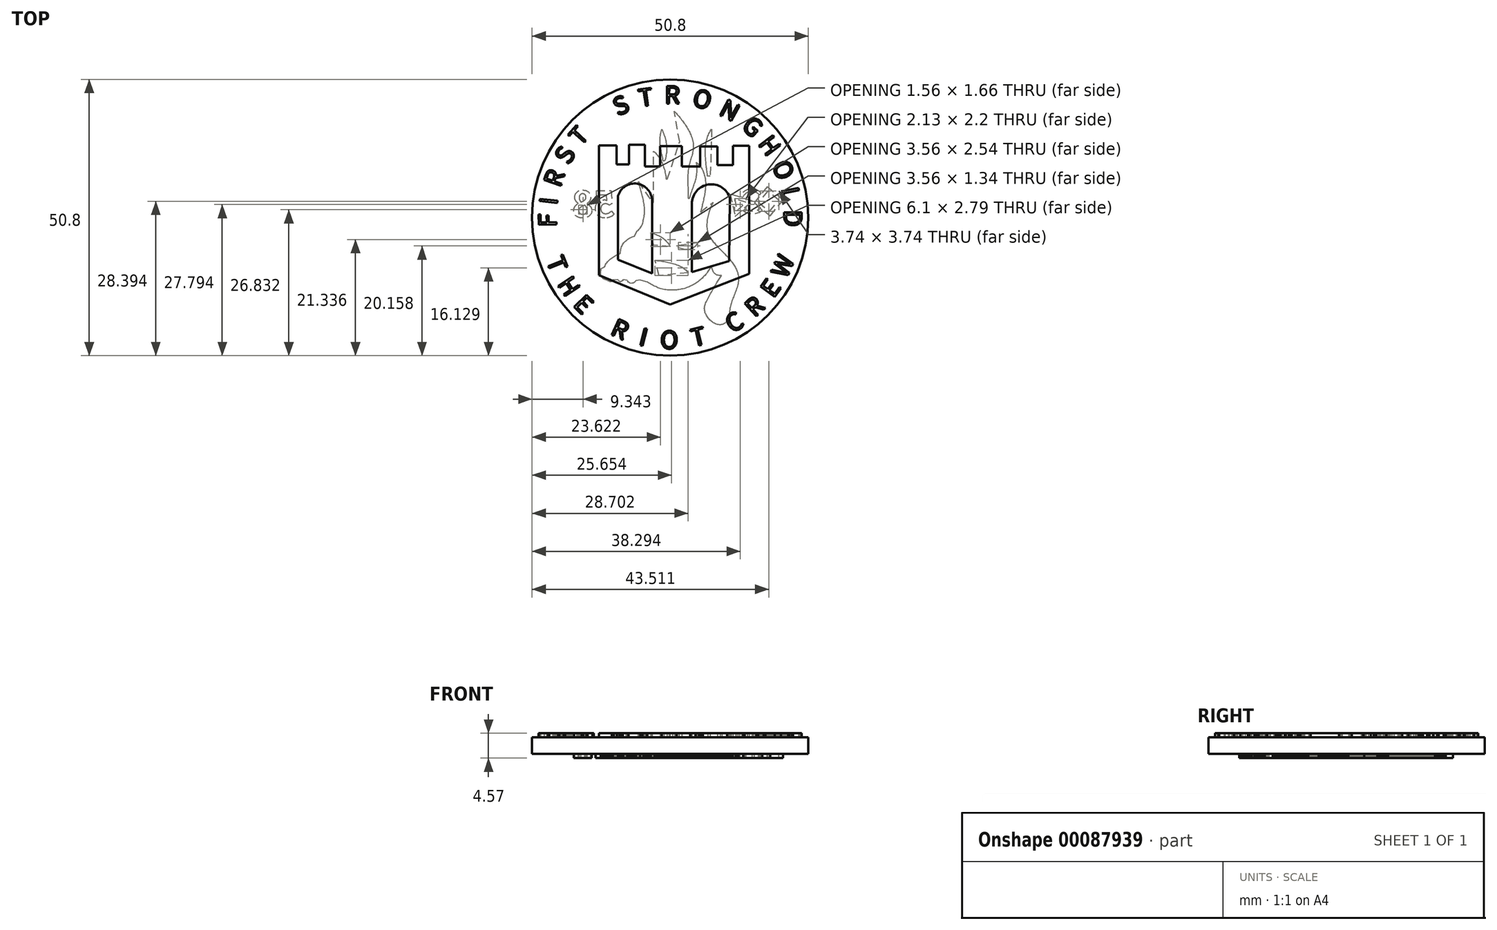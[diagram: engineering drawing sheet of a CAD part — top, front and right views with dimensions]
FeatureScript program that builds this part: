
annotation { "Feature Type Name" : "Feature", "Feature Type Description" : "" }
export const myFeature = defineFeature(function(context is Context, id is Id, definition is map)
    precondition{}
    {
        {
            var Q0;
            Q0=qCreatedBy(makeId("Top.planeOp"),FACE);
            var sketch = newSketch(context, id + "F0", { "sketchPlane" : qUnion([Q0])});
            skCircle(sketch, "E0", {"center": v(0, 0) * mm, "radius": 25.4 * mm});
            skSolve(sketch);
        }
        {
            var Q0;
            Q0 = qSketchRegion(id + "F0", true);
            extrude(context, id + "F1", {"entities" : qUnion([Q0]), "depth" : 3.05 * mm});
        }
        {
            var Q0;
            Q0=makeQuery(id+"F1.opExtrude","CAP_FACE",FACE,{"disambiguationData":[OSD([sQuery(id+"F0.wireOp",EDGE,"E0")])],"isStart":true});
            var sketch = newSketch(context, id + "F2", { "sketchPlane" : qUnion([Q0])});
            skSolve(sketch);
        }
        {
            var Q0;
            Q0=makeQuery(id+"F1.opExtrude","CAP_FACE",FACE,{"disambiguationData":[OSD([sQuery(id+"F0.wireOp",EDGE,"E0")])],"isStart":false});
            var sketch = newSketch(context, id + "F3", { "sketchPlane" : qUnion([Q0])});
            skText(sketch, "E1", { "text": "F", "fontName": "NotoSansCJKjp-Regular.otf"});
            skText(sketch, "E2", { "text": "I", "fontName": "NotoSansCJKjp-Regular.otf"});
            skText(sketch, "E3", { "text": "R", "fontName": "NotoSansCJKjp-Regular.otf"});
            skText(sketch, "E4", { "text": "S", "fontName": "NotoSansCJKjp-Regular.otf"});
            skText(sketch, "E5", { "text": "T", "fontName": "NotoSansCJKjp-Regular.otf"});
            skCircle(sketch, "E6", {"center": v(0, 0) * mm, "radius": 20.96 * mm, "construction": true});
            skText(sketch, "E7", { "text": "S", "fontName": "NotoSansCJKjp-Regular.otf"});
            skText(sketch, "E8", { "text": "T", "fontName": "NotoSansCJKjp-Regular.otf"});
            skText(sketch, "E9", { "text": "O", "fontName": "NotoSansCJKjp-Regular.otf"});
            skText(sketch, "E10", { "text": "R", "fontName": "NotoSansCJKjp-Regular.otf"});
            skText(sketch, "E11", { "text": "N", "fontName": "NotoSansCJKjp-Regular.otf"});
            skText(sketch, "E12", { "text": "G", "fontName": "NotoSansCJKjp-Regular.otf"});
            skText(sketch, "E13", { "text": "H", "fontName": "NotoSansCJKjp-Regular.otf"});
            skText(sketch, "E14", { "text": "L", "fontName": "NotoSansCJKjp-Regular.otf"});
            skText(sketch, "E15", { "text": "D", "fontName": "NotoSansCJKjp-Regular.otf"});
            skText(sketch, "E16", { "text": "O", "fontName": "NotoSansCJKjp-Regular.otf"});
            skText(sketch, "E17", { "text": "T", "fontName": "NotoSansCJKjp-Regular.otf"});
            skText(sketch, "E18", { "text": "H", "fontName": "NotoSansCJKjp-Regular.otf"});
            skText(sketch, "E19", { "text": "E", "fontName": "NotoSansCJKjp-Regular.otf"});
            skText(sketch, "E20", { "text": "R", "fontName": "NotoSansCJKjp-Regular.otf"});
            skText(sketch, "E21", { "text": "I", "fontName": "NotoSansCJKjp-Regular.otf"});
            skText(sketch, "E22", { "text": "O", "fontName": "NotoSansCJKjp-Regular.otf"});
            skText(sketch, "E23", { "text": "T", "fontName": "NotoSansCJKjp-Regular.otf"});
            skText(sketch, "E24", { "text": "C", "fontName": "NotoSansCJKjp-Regular.otf"});
            skText(sketch, "E25", { "text": "E", "fontName": "NotoSansCJKjp-Regular.otf"});
            skText(sketch, "E26", { "text": "R", "fontName": "NotoSansCJKjp-Regular.otf"});
            skText(sketch, "E27", { "text": "W", "fontName": "NotoSansCJKjp-Regular.otf"});
            skLineSegment(sketch, "E28", {"start": v(-13.1, 13.29) * mm, "end": v(-13.1, -10.62) * mm});
            skLineSegment(sketch, "E29", {"start": v(-13.1, -10.62) * mm, "end": v(0, -15.98) * mm});
            skLineSegment(sketch, "E30", {"start": v(0, -15.98) * mm, "end": v(14.5, -10.34) * mm});
            skLineSegment(sketch, "E31", {"start": v(14.5, -10.34) * mm, "end": v(14.5, 13.2) * mm});
            skLineSegment(sketch, "E32", {"start": v(-13.1, 13.29) * mm, "end": v(-9.9, 13.29) * mm});
            skLineSegment(sketch, "E33", {"start": v(-9.9, 13.29) * mm, "end": v(-9.9, 9.78) * mm});
            skLineSegment(sketch, "E34", {"start": v(-9.9, 9.78) * mm, "end": v(-7.61, 9.78) * mm});
            skLineSegment(sketch, "E35", {"start": v(-7.61, 9.78) * mm, "end": v(-7.61, 13.36) * mm});
            skLineSegment(sketch, "E36", {"start": v(-7.61, 13.36) * mm, "end": v(-4.64, 13.36) * mm});
            skLineSegment(sketch, "E37", {"start": v(-4.64, 13.36) * mm, "end": v(-4.64, 9.4) * mm});
            skLineSegment(sketch, "E38", {"start": v(-4.64, 9.4) * mm, "end": v(-1.9, 9.4) * mm});
            skLineSegment(sketch, "E39", {"start": v(-1.9, 9.4) * mm, "end": v(-1.9, 13.1) * mm});
            skLineSegment(sketch, "E40", {"start": v(-1.9, 13.1) * mm, "end": v(2.15, 13.1) * mm});
            skLineSegment(sketch, "E41", {"start": v(2.15, 13.1) * mm, "end": v(2.15, 9.4) * mm});
            skLineSegment(sketch, "E42", {"start": v(2.15, 9.4) * mm, "end": v(5.5, 9.4) * mm});
            skLineSegment(sketch, "E43", {"start": v(5.5, 9.4) * mm, "end": v(5.5, 13.05) * mm});
            skLineSegment(sketch, "E44", {"start": v(5.5, 13.05) * mm, "end": v(8.7, 13.05) * mm});
            skLineSegment(sketch, "E45", {"start": v(8.7, 13.05) * mm, "end": v(8.7, 9.63) * mm});
            skLineSegment(sketch, "E46", {"start": v(8.7, 9.63) * mm, "end": v(11.52, 9.63) * mm});
            skLineSegment(sketch, "E47", {"start": v(11.52, 9.63) * mm, "end": v(11.52, 13.2) * mm});
            skLineSegment(sketch, "E48", {"start": v(11.52, 13.2) * mm, "end": v(14.5, 13.2) * mm});
            skLineSegment(sketch, "E49", {"start": v(-9.6, 3.99) * mm, "end": v(-9.6, -7.77) * mm});
            skLineSegment(sketch, "E50", {"start": v(-9.6, -7.77) * mm, "end": v(-3.34, -10.31) * mm});
            skLineSegment(sketch, "E51", {"start": v(-3.34, -10.31) * mm, "end": v(-3.34, 3.07) * mm});
            skArc(sketch, "E52", {"start": v(-3.34, 3.07) * mm, "mid": v(-6.07, 6.23) * mm, "end": v(-9.6, 3.99) * mm});
            skLineSegment(sketch, "E53", {"start": v(3.97, 2.54) * mm, "end": v(3.97, -10.04) * mm});
            skLineSegment(sketch, "E54", {"start": v(3.97, -10.04) * mm, "end": v(10.83, -7.98) * mm});
            skLineSegment(sketch, "E55", {"start": v(10.83, -7.98) * mm, "end": v(10.99, 3.53) * mm});
            skArc(sketch, "E56", {"start": v(10.99, 3.53) * mm, "mid": v(7.05, 6.08) * mm, "end": v(3.97, 2.54) * mm});
            skCircle(sketch, "E57", {"center": v(0, 0) * mm, "radius": 24.13 * mm, "construction": true});
            const initialGuessF3  = {"E1": [-0.02089, -0.0017, -0.02572, 0.99967, 0.0032], "E2": [-0.02083, 0.00224, 0.1071, 0.99425, 0.00318], "E3": [-0.02024, 0.00542, 0.32053, 0.94724, 0.00322], "E4": [-0.01865, 0.00955, 0.50735, 0.86174, 0.00321], "E5": [-0.0165, 0.01298, 0.66413, 0.74762, 0.00317], "E7": [-0.00964, 0.01865, 0.91348, 0.40689, 0.00317], "E8": [-0.00558, 0.02032, 0.98899, 0.14799, 0.00318], "E9": [0.00392, 0.02064, 0.96647, -0.25677, 0.00317], "E10": [-0.00106, 0.02097, 0.99991, -0.01329, 0.00318], "E11": [0.0088, 0.01906, 0.87845, -0.47783, 0.00318], "E12": [0.01296, 0.01652, 0.74534, -0.66669, 0.00317], "E13": [0.01602, 0.01358, 0.59523, -0.80356, 0.00317], "E14": [0.02032, 0.00523, 0.19664, -0.98048, 0.00317], "E15": [0.02096, 0.00136, -0.00136, -1, 0.00317], "E16": [0.01867, 0.00964, 0.39392, -0.91914, 0.00318], "E17": [-0.02283, -0.00792, 0.3764, -0.92645, 0.00318], "E18": [-0.02086, -0.01221, 0.55387, -0.8326, 0.00317], "E19": [-0.01796, -0.01616, 0.70445, -0.70976, 0.00317], "E20": [-0.01115, -0.02144, 0.9114, -0.41154, 0.00318], "E21": [-0.00592, -0.02339, 0.96943, -0.24538, 0.00318], "E22": [-0.00184, -0.0241, 0.9999, -0.01387, 0.00318], "E23": [0.00424, -0.02379, 0.97409, 0.22617, 0.00317], "E24": [0.0114, -0.0213, 0.85453, 0.5194, 0.00317], "E25": [0.01898, -0.01495, 0.57975, 0.8148, 0.00317], "E26": [0.01556, -0.01849, 0.7281, 0.68548, 0.00318], "E27": [0.02138, -0.01135, 0.399, 0.91695, 0.00317]};
            skSetInitialGuess(sketch, initialGuessF3);
            skSolve(sketch);
        }
        {
            var Q0;
            Q0 = qSketchRegion(id + "F3", true);
            extrude(context, id + "F4", {"entities" : qUnion([Q0]), "operationType" : NewBodyOperationType.ADD, "depth" : 0.76 * mm});
        }
        {
            var Q0;
            Q0=makeQuery(id+"F2.imprint","IMPRINT",FACE,{"disambiguationData":[TD([[makeQuery(id+"F2.imprint","IMPRINT",EDGE,{"derivedFrom":makeQuery(id+"F1.opExtrude","CAP_EDGE",EDGE,{"disambiguationData":[OSD([sQuery(id+"F0.wireOp",EDGE,"E0")])],"isStart":true})}),-1.0]])]});
            var sketch = newSketch(context, id + "F5", { "sketchPlane" : qUnion([Q0])});
            skLineSegment(sketch, "E58", {"start": v(-0.76, 19.56) * mm, "end": v(-0.93, 19.36) * mm});
            skLineSegment(sketch, "E59", {"start": v(-0.93, 19.36) * mm, "end": v(-1.1, 19.17) * mm});
            skLineSegment(sketch, "E60", {"start": v(-1.1, 19.17) * mm, "end": v(-1.27, 18.97) * mm});
            skLineSegment(sketch, "E61", {"start": v(-1.27, 18.97) * mm, "end": v(-1.44, 18.78) * mm});
            skLineSegment(sketch, "E62", {"start": v(-1.44, 18.78) * mm, "end": v(-1.6, 18.58) * mm});
            skLineSegment(sketch, "E63", {"start": v(-1.6, 18.58) * mm, "end": v(-1.77, 18.39) * mm});
            skLineSegment(sketch, "E64", {"start": v(-1.77, 18.39) * mm, "end": v(-1.93, 18.2) * mm});
            skLineSegment(sketch, "E65", {"start": v(-1.93, 18.2) * mm, "end": v(-2.09, 18) * mm});
            skLineSegment(sketch, "E66", {"start": v(-2.09, 18) * mm, "end": v(-2.24, 17.8) * mm});
            skLineSegment(sketch, "E67", {"start": v(-2.24, 17.8) * mm, "end": v(-2.4, 17.59) * mm});
            skLineSegment(sketch, "E68", {"start": v(-2.4, 17.59) * mm, "end": v(-2.55, 17.39) * mm});
            skLineSegment(sketch, "E69", {"start": v(-2.55, 17.39) * mm, "end": v(-2.7, 17.18) * mm});
            skLineSegment(sketch, "E70", {"start": v(-2.7, 17.18) * mm, "end": v(-2.84, 16.97) * mm});
            skLineSegment(sketch, "E71", {"start": v(-2.84, 16.97) * mm, "end": v(-2.97, 16.76) * mm});
            skLineSegment(sketch, "E72", {"start": v(-2.97, 16.76) * mm, "end": v(-3.1, 16.55) * mm});
            skLineSegment(sketch, "E73", {"start": v(-3.1, 16.55) * mm, "end": v(-3.23, 16.33) * mm});
            skLineSegment(sketch, "E74", {"start": v(-3.23, 16.33) * mm, "end": v(-3.35, 16.12) * mm});
            skLineSegment(sketch, "E75", {"start": v(-3.35, 16.12) * mm, "end": v(-3.47, 15.9) * mm});
            skLineSegment(sketch, "E76", {"start": v(-3.47, 15.9) * mm, "end": v(-3.58, 15.67) * mm});
            skLineSegment(sketch, "E77", {"start": v(-3.58, 15.67) * mm, "end": v(-3.68, 15.44) * mm});
            skLineSegment(sketch, "E78", {"start": v(-3.68, 15.44) * mm, "end": v(-3.78, 15.2) * mm});
            skLineSegment(sketch, "E79", {"start": v(-3.78, 15.2) * mm, "end": v(-3.87, 14.97) * mm});
            skLineSegment(sketch, "E80", {"start": v(-3.87, 14.97) * mm, "end": v(-3.95, 14.73) * mm});
            skLineSegment(sketch, "E81", {"start": v(-3.95, 14.73) * mm, "end": v(-4.03, 14.48) * mm});
            skLineSegment(sketch, "E82", {"start": v(-4.03, 14.48) * mm, "end": v(-4.1, 14.23) * mm});
            skLineSegment(sketch, "E83", {"start": v(-4.1, 14.23) * mm, "end": v(-4.15, 13.98) * mm});
            skLineSegment(sketch, "E84", {"start": v(-4.15, 13.98) * mm, "end": v(-4.2, 13.72) * mm});
            skLineSegment(sketch, "E85", {"start": v(-4.2, 13.72) * mm, "end": v(-4.23, 13.47) * mm});
            skLineSegment(sketch, "E86", {"start": v(-4.23, 13.47) * mm, "end": v(-4.25, 13.22) * mm});
            skLineSegment(sketch, "E87", {"start": v(-4.25, 13.22) * mm, "end": v(-4.25, 12.97) * mm});
            skLineSegment(sketch, "E88", {"start": v(-4.25, 12.97) * mm, "end": v(-4.24, 12.73) * mm});
            skLineSegment(sketch, "E89", {"start": v(-4.24, 12.73) * mm, "end": v(-4.21, 12.49) * mm});
            skLineSegment(sketch, "E90", {"start": v(-4.21, 12.49) * mm, "end": v(-4.17, 12.25) * mm});
            skLineSegment(sketch, "E91", {"start": v(-4.17, 12.25) * mm, "end": v(-4.13, 12) * mm});
            skLineSegment(sketch, "E92", {"start": v(-4.13, 12) * mm, "end": v(-4.07, 11.77) * mm});
            skLineSegment(sketch, "E93", {"start": v(-4.07, 11.77) * mm, "end": v(-4.01, 11.53) * mm});
            skLineSegment(sketch, "E94", {"start": v(-4.01, 11.53) * mm, "end": v(-3.95, 11.3) * mm});
            skLineSegment(sketch, "E95", {"start": v(-3.95, 11.3) * mm, "end": v(-3.88, 11.06) * mm});
            skLineSegment(sketch, "E96", {"start": v(-3.88, 11.06) * mm, "end": v(-3.8, 10.82) * mm});
            skLineSegment(sketch, "E97", {"start": v(-3.8, 10.82) * mm, "end": v(-3.74, 10.58) * mm});
            skLineSegment(sketch, "E98", {"start": v(-3.74, 10.58) * mm, "end": v(-3.66, 10.34) * mm});
            skLineSegment(sketch, "E99", {"start": v(-3.66, 10.34) * mm, "end": v(-3.6, 10.1) * mm});
            skLineSegment(sketch, "E100", {"start": v(-3.6, 10.1) * mm, "end": v(-3.53, 9.87) * mm});
            skLineSegment(sketch, "E101", {"start": v(-3.53, 9.87) * mm, "end": v(-3.47, 9.63) * mm});
            skLineSegment(sketch, "E102", {"start": v(-3.47, 9.63) * mm, "end": v(-3.42, 9.39) * mm});
            skLineSegment(sketch, "E103", {"start": v(-3.42, 9.39) * mm, "end": v(-3.37, 9.14) * mm});
            skLineSegment(sketch, "E104", {"start": v(-3.37, 9.14) * mm, "end": v(-3.34, 8.9) * mm});
            skLineSegment(sketch, "E105", {"start": v(-3.34, 8.9) * mm, "end": v(-3.3, 8.64) * mm});
            skLineSegment(sketch, "E106", {"start": v(-3.3, 8.64) * mm, "end": v(-3.28, 8.4) * mm});
            skLineSegment(sketch, "E107", {"start": v(-3.28, 8.4) * mm, "end": v(-3.26, 8.14) * mm});
            skLineSegment(sketch, "E108", {"start": v(-3.26, 8.14) * mm, "end": v(-3.24, 7.89) * mm});
            skLineSegment(sketch, "E109", {"start": v(-3.24, 7.89) * mm, "end": v(-3.23, 7.63) * mm});
            skLineSegment(sketch, "E110", {"start": v(-3.23, 7.63) * mm, "end": v(-3.22, 7.38) * mm});
            skLineSegment(sketch, "E111", {"start": v(-3.22, 7.38) * mm, "end": v(-3.22, 7.12) * mm});
            skLineSegment(sketch, "E112", {"start": v(-3.22, 7.12) * mm, "end": v(-3.22, 6.87) * mm});
            skLineSegment(sketch, "E113", {"start": v(-3.22, 6.87) * mm, "end": v(-3.22, 6.61) * mm});
            skLineSegment(sketch, "E114", {"start": v(-3.22, 6.61) * mm, "end": v(-3.23, 6.36) * mm});
            skLineSegment(sketch, "E115", {"start": v(-3.23, 6.36) * mm, "end": v(-3.23, 6.1) * mm});
            skLineSegment(sketch, "E116", {"start": v(-3.23, 6.1) * mm, "end": v(-3.24, 5.85) * mm});
            skLineSegment(sketch, "E117", {"start": v(-3.24, 5.85) * mm, "end": v(-3.25, 5.59) * mm});
            skLineSegment(sketch, "E118", {"start": v(-3.25, 5.59) * mm, "end": v(-3.26, 5.33) * mm});
            skLineSegment(sketch, "E119", {"start": v(-3.26, 5.33) * mm, "end": v(-3.27, 5.08) * mm});
            skLineSegment(sketch, "E120", {"start": v(-3.27, 5.08) * mm, "end": v(-3.28, 4.82) * mm});
            skLineSegment(sketch, "E121", {"start": v(-3.28, 4.82) * mm, "end": v(-3.28, 4.57) * mm});
            skLineSegment(sketch, "E122", {"start": v(-3.28, 4.57) * mm, "end": v(-3.3, 4.31) * mm});
            skLineSegment(sketch, "E123", {"start": v(-3.3, 4.31) * mm, "end": v(-3.3, 4.06) * mm});
            skLineSegment(sketch, "E124", {"start": v(-3.3, 4.06) * mm, "end": v(-3.3, 3.8) * mm});
            skLineSegment(sketch, "E125", {"start": v(-3.3, 3.8) * mm, "end": v(-3.3, 3.56) * mm});
            skLineSegment(sketch, "E126", {"start": v(-3.3, 3.56) * mm, "end": v(-3.56, 3.56) * mm});
            skLineSegment(sketch, "E127", {"start": v(-3.56, 3.56) * mm, "end": v(-3.63, 3.82) * mm});
            skLineSegment(sketch, "E128", {"start": v(-3.63, 3.82) * mm, "end": v(-3.71, 4.07) * mm});
            skLineSegment(sketch, "E129", {"start": v(-3.71, 4.07) * mm, "end": v(-3.8, 4.32) * mm});
            skLineSegment(sketch, "E130", {"start": v(-3.8, 4.32) * mm, "end": v(-3.88, 4.57) * mm});
            skLineSegment(sketch, "E131", {"start": v(-3.88, 4.57) * mm, "end": v(-3.96, 4.81) * mm});
            skLineSegment(sketch, "E132", {"start": v(-3.96, 4.81) * mm, "end": v(-4.05, 5.05) * mm});
            skLineSegment(sketch, "E133", {"start": v(-4.05, 5.05) * mm, "end": v(-4.13, 5.29) * mm});
            skLineSegment(sketch, "E134", {"start": v(-4.13, 5.29) * mm, "end": v(-4.21, 5.52) * mm});
            skLineSegment(sketch, "E135", {"start": v(-4.21, 5.52) * mm, "end": v(-4.3, 5.75) * mm});
            skLineSegment(sketch, "E136", {"start": v(-4.3, 5.75) * mm, "end": v(-4.37, 5.98) * mm});
            skLineSegment(sketch, "E137", {"start": v(-4.37, 5.98) * mm, "end": v(-4.45, 6.21) * mm});
            skLineSegment(sketch, "E138", {"start": v(-4.45, 6.21) * mm, "end": v(-4.52, 6.44) * mm});
            skLineSegment(sketch, "E139", {"start": v(-4.52, 6.44) * mm, "end": v(-4.6, 6.67) * mm});
            skLineSegment(sketch, "E140", {"start": v(-4.6, 6.67) * mm, "end": v(-4.66, 6.9) * mm});
            skLineSegment(sketch, "E141", {"start": v(-4.66, 6.9) * mm, "end": v(-4.72, 7.13) * mm});
            skLineSegment(sketch, "E142", {"start": v(-4.72, 7.13) * mm, "end": v(-4.77, 7.37) * mm});
            skLineSegment(sketch, "E143", {"start": v(-4.77, 7.37) * mm, "end": v(-4.82, 7.6) * mm});
            skLineSegment(sketch, "E144", {"start": v(-4.82, 7.6) * mm, "end": v(-4.86, 7.84) * mm});
            skLineSegment(sketch, "E145", {"start": v(-4.86, 7.84) * mm, "end": v(-4.9, 8.08) * mm});
            skLineSegment(sketch, "E146", {"start": v(-4.9, 8.08) * mm, "end": v(-4.92, 8.32) * mm});
            skLineSegment(sketch, "E147", {"start": v(-4.92, 8.32) * mm, "end": v(-4.94, 8.57) * mm});
            skLineSegment(sketch, "E148", {"start": v(-4.94, 8.57) * mm, "end": v(-4.94, 8.82) * mm});
            skLineSegment(sketch, "E149", {"start": v(-4.94, 8.82) * mm, "end": v(-4.94, 9.07) * mm});
            skLineSegment(sketch, "E150", {"start": v(-4.94, 9.07) * mm, "end": v(-4.93, 9.34) * mm});
            skLineSegment(sketch, "E151", {"start": v(-4.93, 9.34) * mm, "end": v(-4.9, 9.6) * mm});
            skLineSegment(sketch, "E152", {"start": v(-4.9, 9.6) * mm, "end": v(-4.87, 9.88) * mm});
            skLineSegment(sketch, "E153", {"start": v(-4.87, 9.88) * mm, "end": v(-4.83, 10.16) * mm});
            skLineSegment(sketch, "E154", {"start": v(-4.83, 10.16) * mm, "end": v(-5.01, 9.99) * mm});
            skLineSegment(sketch, "E155", {"start": v(-5.01, 9.99) * mm, "end": v(-5.19, 9.8) * mm});
            skLineSegment(sketch, "E156", {"start": v(-5.19, 9.8) * mm, "end": v(-5.35, 9.63) * mm});
            skLineSegment(sketch, "E157", {"start": v(-5.35, 9.63) * mm, "end": v(-5.5, 9.44) * mm});
            skLineSegment(sketch, "E158", {"start": v(-5.5, 9.44) * mm, "end": v(-5.64, 9.25) * mm});
            skLineSegment(sketch, "E159", {"start": v(-5.64, 9.25) * mm, "end": v(-5.77, 9.06) * mm});
            skLineSegment(sketch, "E160", {"start": v(-5.77, 9.06) * mm, "end": v(-5.88, 8.86) * mm});
            skLineSegment(sketch, "E161", {"start": v(-5.88, 8.86) * mm, "end": v(-5.98, 8.66) * mm});
            skLineSegment(sketch, "E162", {"start": v(-5.98, 8.66) * mm, "end": v(-6.08, 8.45) * mm});
            skLineSegment(sketch, "E163", {"start": v(-6.08, 8.45) * mm, "end": v(-6.16, 8.24) * mm});
            skLineSegment(sketch, "E164", {"start": v(-6.16, 8.24) * mm, "end": v(-6.23, 8.03) * mm});
            skLineSegment(sketch, "E165", {"start": v(-6.23, 8.03) * mm, "end": v(-6.3, 7.82) * mm});
            skLineSegment(sketch, "E166", {"start": v(-6.3, 7.82) * mm, "end": v(-6.35, 7.6) * mm});
            skLineSegment(sketch, "E167", {"start": v(-6.35, 7.6) * mm, "end": v(-6.4, 7.38) * mm});
            skLineSegment(sketch, "E168", {"start": v(-6.4, 7.38) * mm, "end": v(-6.43, 7.16) * mm});
            skLineSegment(sketch, "E169", {"start": v(-6.43, 7.16) * mm, "end": v(-6.46, 6.94) * mm});
            skLineSegment(sketch, "E170", {"start": v(-6.46, 6.94) * mm, "end": v(-6.48, 6.71) * mm});
            skLineSegment(sketch, "E171", {"start": v(-6.48, 6.71) * mm, "end": v(-6.49, 6.49) * mm});
            skLineSegment(sketch, "E172", {"start": v(-6.49, 6.49) * mm, "end": v(-6.5, 6.26) * mm});
            skLineSegment(sketch, "E173", {"start": v(-6.5, 6.26) * mm, "end": v(-6.5, 6.03) * mm});
            skLineSegment(sketch, "E174", {"start": v(-6.5, 6.03) * mm, "end": v(-6.49, 5.8) * mm});
            skLineSegment(sketch, "E175", {"start": v(-6.49, 5.8) * mm, "end": v(-6.48, 5.57) * mm});
            skLineSegment(sketch, "E176", {"start": v(-6.48, 5.57) * mm, "end": v(-6.46, 5.34) * mm});
            skLineSegment(sketch, "E177", {"start": v(-6.46, 5.34) * mm, "end": v(-6.44, 5.1) * mm});
            skLineSegment(sketch, "E178", {"start": v(-6.44, 5.1) * mm, "end": v(-6.4, 4.87) * mm});
            skLineSegment(sketch, "E179", {"start": v(-6.4, 4.87) * mm, "end": v(-6.38, 4.64) * mm});
            skLineSegment(sketch, "E180", {"start": v(-6.38, 4.64) * mm, "end": v(-6.34, 4.4) * mm});
            skLineSegment(sketch, "E181", {"start": v(-6.34, 4.4) * mm, "end": v(-6.3, 4.17) * mm});
            skLineSegment(sketch, "E182", {"start": v(-6.3, 4.17) * mm, "end": v(-6.26, 3.94) * mm});
            skLineSegment(sketch, "E183", {"start": v(-6.26, 3.94) * mm, "end": v(-6.21, 3.7) * mm});
            skLineSegment(sketch, "E184", {"start": v(-6.21, 3.7) * mm, "end": v(-6.17, 3.47) * mm});
            skLineSegment(sketch, "E185", {"start": v(-6.17, 3.47) * mm, "end": v(-6.12, 3.24) * mm});
            skLineSegment(sketch, "E186", {"start": v(-6.12, 3.24) * mm, "end": v(-6.07, 3) * mm});
            skLineSegment(sketch, "E187", {"start": v(-6.07, 3) * mm, "end": v(-6.01, 2.78) * mm});
            skLineSegment(sketch, "E188", {"start": v(-6.01, 2.78) * mm, "end": v(-5.96, 2.55) * mm});
            skLineSegment(sketch, "E189", {"start": v(-5.96, 2.55) * mm, "end": v(-5.9, 2.33) * mm});
            skLineSegment(sketch, "E190", {"start": v(-5.9, 2.33) * mm, "end": v(-5.85, 2.1) * mm});
            skLineSegment(sketch, "E191", {"start": v(-5.85, 2.1) * mm, "end": v(-5.8, 1.88) * mm});
            skLineSegment(sketch, "E192", {"start": v(-5.8, 1.88) * mm, "end": v(-5.74, 1.66) * mm});
            skLineSegment(sketch, "E193", {"start": v(-5.74, 1.66) * mm, "end": v(-5.69, 1.44) * mm});
            skLineSegment(sketch, "E194", {"start": v(-5.69, 1.44) * mm, "end": v(-5.64, 1.23) * mm});
            skLineSegment(sketch, "E195", {"start": v(-5.64, 1.23) * mm, "end": v(-5.59, 1.02) * mm});
            skLineSegment(sketch, "E196", {"start": v(-5.59, 1.02) * mm, "end": v(-7.87, 2.8) * mm});
            skLineSegment(sketch, "E197", {"start": v(-7.87, 2.8) * mm, "end": v(-7.78, 2.6) * mm});
            skLineSegment(sketch, "E198", {"start": v(-7.78, 2.6) * mm, "end": v(-7.68, 2.4) * mm});
            skLineSegment(sketch, "E199", {"start": v(-7.68, 2.4) * mm, "end": v(-7.59, 2.19) * mm});
            skLineSegment(sketch, "E200", {"start": v(-7.59, 2.19) * mm, "end": v(-7.5, 1.97) * mm});
            skLineSegment(sketch, "E201", {"start": v(-7.5, 1.97) * mm, "end": v(-7.4, 1.75) * mm});
            skLineSegment(sketch, "E202", {"start": v(-7.4, 1.75) * mm, "end": v(-7.32, 1.52) * mm});
            skLineSegment(sketch, "E203", {"start": v(-7.32, 1.52) * mm, "end": v(-7.24, 1.28) * mm});
            skLineSegment(sketch, "E204", {"start": v(-7.24, 1.28) * mm, "end": v(-7.16, 1.04) * mm});
            skLineSegment(sketch, "E205", {"start": v(-7.16, 1.04) * mm, "end": v(-7.08, 0.8) * mm});
            skLineSegment(sketch, "E206", {"start": v(-7.08, 0.8) * mm, "end": v(-7.01, 0.55) * mm});
            skLineSegment(sketch, "E207", {"start": v(-7.01, 0.55) * mm, "end": v(-6.95, 0.3) * mm});
            skLineSegment(sketch, "E208", {"start": v(-6.95, 0.3) * mm, "end": v(-6.9, 0.06) * mm});
            skLineSegment(sketch, "E209", {"start": v(-6.9, 0.06) * mm, "end": v(-6.84, -0.2) * mm});
            skLineSegment(sketch, "E210", {"start": v(-6.84, -0.2) * mm, "end": v(-6.8, -0.45) * mm});
            skLineSegment(sketch, "E211", {"start": v(-6.8, -0.45) * mm, "end": v(-6.77, -0.7) * mm});
            skLineSegment(sketch, "E212", {"start": v(-6.77, -0.7) * mm, "end": v(-6.74, -0.95) * mm});
            skLineSegment(sketch, "E213", {"start": v(-6.74, -0.95) * mm, "end": v(-6.73, -1.2) * mm});
            skLineSegment(sketch, "E214", {"start": v(-6.73, -1.2) * mm, "end": v(-6.72, -1.45) * mm});
            skLineSegment(sketch, "E215", {"start": v(-6.72, -1.45) * mm, "end": v(-6.73, -1.7) * mm});
            skLineSegment(sketch, "E216", {"start": v(-6.73, -1.7) * mm, "end": v(-6.75, -1.94) * mm});
            skLineSegment(sketch, "E217", {"start": v(-6.75, -1.94) * mm, "end": v(-6.78, -2.18) * mm});
            skLineSegment(sketch, "E218", {"start": v(-6.78, -2.18) * mm, "end": v(-6.82, -2.42) * mm});
            skLineSegment(sketch, "E219", {"start": v(-6.82, -2.42) * mm, "end": v(-6.87, -2.65) * mm});
            skLineSegment(sketch, "E220", {"start": v(-6.87, -2.65) * mm, "end": v(-6.94, -2.87) * mm});
            skLineSegment(sketch, "E221", {"start": v(-6.94, -2.87) * mm, "end": v(-7.02, -3.1) * mm});
            skLineSegment(sketch, "E222", {"start": v(-7.02, -3.1) * mm, "end": v(-7.12, -3.3) * mm});
            skLineSegment(sketch, "E223", {"start": v(-7.12, -3.3) * mm, "end": v(-7.21, -3.47) * mm});
            skLineSegment(sketch, "E224", {"start": v(-7.21, -3.47) * mm, "end": v(-7.31, -3.65) * mm});
            skLineSegment(sketch, "E225", {"start": v(-7.31, -3.65) * mm, "end": v(-7.42, -3.82) * mm});
            skLineSegment(sketch, "E226", {"start": v(-7.42, -3.82) * mm, "end": v(-7.54, -4) * mm});
            skLineSegment(sketch, "E227", {"start": v(-7.54, -4) * mm, "end": v(-7.67, -4.16) * mm});
            skLineSegment(sketch, "E228", {"start": v(-7.67, -4.16) * mm, "end": v(-7.8, -4.33) * mm});
            skLineSegment(sketch, "E229", {"start": v(-7.8, -4.33) * mm, "end": v(-7.93, -4.5) * mm});
            skLineSegment(sketch, "E230", {"start": v(-7.93, -4.5) * mm, "end": v(-8.08, -4.67) * mm});
            skLineSegment(sketch, "E231", {"start": v(-8.08, -4.67) * mm, "end": v(-8.23, -4.84) * mm});
            skLineSegment(sketch, "E232", {"start": v(-8.23, -4.84) * mm, "end": v(-8.38, -5.01) * mm});
            skLineSegment(sketch, "E233", {"start": v(-8.38, -5.01) * mm, "end": v(-8.54, -5.18) * mm});
            skLineSegment(sketch, "E234", {"start": v(-8.54, -5.18) * mm, "end": v(-8.7, -5.35) * mm});
            skLineSegment(sketch, "E235", {"start": v(-8.7, -5.35) * mm, "end": v(-8.86, -5.52) * mm});
            skLineSegment(sketch, "E236", {"start": v(-8.86, -5.52) * mm, "end": v(-9.03, -5.7) * mm});
            skLineSegment(sketch, "E237", {"start": v(-9.03, -5.7) * mm, "end": v(-9.2, -5.86) * mm});
            skLineSegment(sketch, "E238", {"start": v(-9.2, -5.86) * mm, "end": v(-9.37, -6.03) * mm});
            skLineSegment(sketch, "E239", {"start": v(-9.37, -6.03) * mm, "end": v(-9.54, -6.2) * mm});
            skLineSegment(sketch, "E240", {"start": v(-9.54, -6.2) * mm, "end": v(-9.7, -6.38) * mm});
            skLineSegment(sketch, "E241", {"start": v(-9.7, -6.38) * mm, "end": v(-9.88, -6.55) * mm});
            skLineSegment(sketch, "E242", {"start": v(-9.88, -6.55) * mm, "end": v(-10.05, -6.73) * mm});
            skLineSegment(sketch, "E243", {"start": v(-10.05, -6.73) * mm, "end": v(-10.22, -6.9) * mm});
            skLineSegment(sketch, "E244", {"start": v(-10.22, -6.9) * mm, "end": v(-10.39, -7.08) * mm});
            skLineSegment(sketch, "E245", {"start": v(-10.39, -7.08) * mm, "end": v(-10.55, -7.26) * mm});
            skLineSegment(sketch, "E246", {"start": v(-10.55, -7.26) * mm, "end": v(-10.71, -7.44) * mm});
            skLineSegment(sketch, "E247", {"start": v(-10.71, -7.44) * mm, "end": v(-10.87, -7.62) * mm});
            skLineSegment(sketch, "E248", {"start": v(-10.87, -7.62) * mm, "end": v(-11.03, -7.8) * mm});
            skLineSegment(sketch, "E249", {"start": v(-11.03, -7.8) * mm, "end": v(-11.18, -7.99) * mm});
            skLineSegment(sketch, "E250", {"start": v(-11.18, -7.99) * mm, "end": v(-11.32, -8.17) * mm});
            skLineSegment(sketch, "E251", {"start": v(-11.32, -8.17) * mm, "end": v(-11.46, -8.36) * mm});
            skLineSegment(sketch, "E252", {"start": v(-11.46, -8.36) * mm, "end": v(-11.6, -8.55) * mm});
            skLineSegment(sketch, "E253", {"start": v(-11.6, -8.55) * mm, "end": v(-11.73, -8.74) * mm});
            skLineSegment(sketch, "E254", {"start": v(-11.73, -8.74) * mm, "end": v(-11.85, -8.93) * mm});
            skLineSegment(sketch, "E255", {"start": v(-11.85, -8.93) * mm, "end": v(-11.96, -9.13) * mm});
            skLineSegment(sketch, "E256", {"start": v(-11.96, -9.13) * mm, "end": v(-12.06, -9.33) * mm});
            skLineSegment(sketch, "E257", {"start": v(-12.06, -9.33) * mm, "end": v(-12.16, -9.53) * mm});
            skLineSegment(sketch, "E258", {"start": v(-12.16, -9.53) * mm, "end": v(-12.25, -9.73) * mm});
            skLineSegment(sketch, "E259", {"start": v(-12.25, -9.73) * mm, "end": v(-12.33, -9.94) * mm});
            skLineSegment(sketch, "E260", {"start": v(-12.33, -9.94) * mm, "end": v(-12.4, -10.15) * mm});
            skLineSegment(sketch, "E261", {"start": v(-12.4, -10.15) * mm, "end": v(-12.45, -10.36) * mm});
            skLineSegment(sketch, "E262", {"start": v(-12.45, -10.36) * mm, "end": v(-12.5, -10.57) * mm});
            skLineSegment(sketch, "E263", {"start": v(-12.5, -10.57) * mm, "end": v(-12.53, -10.79) * mm});
            skLineSegment(sketch, "E264", {"start": v(-12.53, -10.79) * mm, "end": v(-12.55, -11) * mm});
            skLineSegment(sketch, "E265", {"start": v(-12.55, -11) * mm, "end": v(-12.56, -11.23) * mm});
            skLineSegment(sketch, "E266", {"start": v(-12.56, -11.23) * mm, "end": v(-12.55, -11.45) * mm});
            skLineSegment(sketch, "E267", {"start": v(-12.55, -11.45) * mm, "end": v(-12.53, -11.68) * mm});
            skLineSegment(sketch, "E268", {"start": v(-12.53, -11.68) * mm, "end": v(-12.5, -11.93) * mm});
            skLineSegment(sketch, "E269", {"start": v(-12.5, -11.93) * mm, "end": v(-12.46, -12.17) * mm});
            skLineSegment(sketch, "E270", {"start": v(-12.46, -12.17) * mm, "end": v(-12.4, -12.42) * mm});
            skLineSegment(sketch, "E271", {"start": v(-12.4, -12.42) * mm, "end": v(-12.34, -12.66) * mm});
            skLineSegment(sketch, "E272", {"start": v(-12.34, -12.66) * mm, "end": v(-12.27, -12.9) * mm});
            skLineSegment(sketch, "E273", {"start": v(-12.27, -12.9) * mm, "end": v(-12.19, -13.14) * mm});
            skLineSegment(sketch, "E274", {"start": v(-12.19, -13.14) * mm, "end": v(-12.1, -13.39) * mm});
            skLineSegment(sketch, "E275", {"start": v(-12.1, -13.39) * mm, "end": v(-12.02, -13.63) * mm});
            skLineSegment(sketch, "E276", {"start": v(-12.02, -13.63) * mm, "end": v(-11.93, -13.87) * mm});
            skLineSegment(sketch, "E277", {"start": v(-11.93, -13.87) * mm, "end": v(-11.83, -14.1) * mm});
            skLineSegment(sketch, "E278", {"start": v(-11.83, -14.1) * mm, "end": v(-11.74, -14.35) * mm});
            skLineSegment(sketch, "E279", {"start": v(-11.74, -14.35) * mm, "end": v(-11.64, -14.59) * mm});
            skLineSegment(sketch, "E280", {"start": v(-11.64, -14.59) * mm, "end": v(-11.55, -14.83) * mm});
            skLineSegment(sketch, "E281", {"start": v(-11.55, -14.83) * mm, "end": v(-11.46, -15.06) * mm});
            skLineSegment(sketch, "E282", {"start": v(-11.46, -15.06) * mm, "end": v(-11.37, -15.3) * mm});
            skLineSegment(sketch, "E283", {"start": v(-11.37, -15.3) * mm, "end": v(-11.29, -15.54) * mm});
            skLineSegment(sketch, "E284", {"start": v(-11.29, -15.54) * mm, "end": v(-11.2, -15.79) * mm});
            skLineSegment(sketch, "E285", {"start": v(-11.2, -15.79) * mm, "end": v(-11.14, -16.03) * mm});
            skLineSegment(sketch, "E286", {"start": v(-11.14, -16.03) * mm, "end": v(-11.07, -16.27) * mm});
            skLineSegment(sketch, "E287", {"start": v(-11.07, -16.27) * mm, "end": v(-11.02, -16.51) * mm});
            skLineSegment(sketch, "E288", {"start": v(-11.02, -16.51) * mm, "end": v(-10.98, -16.73) * mm});
            skLineSegment(sketch, "E289", {"start": v(-10.98, -16.73) * mm, "end": v(-10.95, -16.97) * mm});
            skLineSegment(sketch, "E290", {"start": v(-10.95, -16.97) * mm, "end": v(-10.93, -17.22) * mm});
            skLineSegment(sketch, "E291", {"start": v(-10.93, -17.22) * mm, "end": v(-10.9, -17.48) * mm});
            skLineSegment(sketch, "E292", {"start": v(-10.9, -17.48) * mm, "end": v(-10.88, -17.73) * mm});
            skLineSegment(sketch, "E293", {"start": v(-10.88, -17.73) * mm, "end": v(-10.85, -17.99) * mm});
            skLineSegment(sketch, "E294", {"start": v(-10.85, -17.99) * mm, "end": v(-10.8, -18.24) * mm});
            skLineSegment(sketch, "E295", {"start": v(-10.8, -18.24) * mm, "end": v(-10.75, -18.48) * mm});
            skLineSegment(sketch, "E296", {"start": v(-10.75, -18.48) * mm, "end": v(-10.67, -18.7) * mm});
            skLineSegment(sketch, "E297", {"start": v(-10.67, -18.7) * mm, "end": v(-10.56, -18.92) * mm});
            skLineSegment(sketch, "E298", {"start": v(-10.56, -18.92) * mm, "end": v(-10.42, -19.1) * mm});
            skLineSegment(sketch, "E299", {"start": v(-10.42, -19.1) * mm, "end": v(-10.26, -19.27) * mm});
            skLineSegment(sketch, "E300", {"start": v(-10.26, -19.27) * mm, "end": v(-10.1, -19.4) * mm});
            skLineSegment(sketch, "E301", {"start": v(-10.1, -19.4) * mm, "end": v(-9.93, -19.52) * mm});
            skLineSegment(sketch, "E302", {"start": v(-9.93, -19.52) * mm, "end": v(-9.76, -19.6) * mm});
            skLineSegment(sketch, "E303", {"start": v(-9.76, -19.6) * mm, "end": v(-9.58, -19.67) * mm});
            skLineSegment(sketch, "E304", {"start": v(-9.58, -19.67) * mm, "end": v(-9.4, -19.71) * mm});
            skLineSegment(sketch, "E305", {"start": v(-9.4, -19.71) * mm, "end": v(-9.22, -19.73) * mm});
            skLineSegment(sketch, "E306", {"start": v(-9.22, -19.73) * mm, "end": v(-9.03, -19.73) * mm});
            skLineSegment(sketch, "E307", {"start": v(-9.03, -19.73) * mm, "end": v(-8.85, -19.71) * mm});
            skLineSegment(sketch, "E308", {"start": v(-8.85, -19.71) * mm, "end": v(-8.66, -19.67) * mm});
            skLineSegment(sketch, "E309", {"start": v(-8.66, -19.67) * mm, "end": v(-8.48, -19.62) * mm});
            skLineSegment(sketch, "E310", {"start": v(-8.48, -19.62) * mm, "end": v(-8.3, -19.55) * mm});
            skLineSegment(sketch, "E311", {"start": v(-8.3, -19.55) * mm, "end": v(-8.12, -19.46) * mm});
            skLineSegment(sketch, "E312", {"start": v(-8.12, -19.46) * mm, "end": v(-7.94, -19.36) * mm});
            skLineSegment(sketch, "E313", {"start": v(-7.94, -19.36) * mm, "end": v(-7.77, -19.25) * mm});
            skLineSegment(sketch, "E314", {"start": v(-7.77, -19.25) * mm, "end": v(-7.6, -19.12) * mm});
            skLineSegment(sketch, "E315", {"start": v(-7.6, -19.12) * mm, "end": v(-7.44, -18.99) * mm});
            skLineSegment(sketch, "E316", {"start": v(-7.44, -18.99) * mm, "end": v(-7.3, -18.84) * mm});
            skLineSegment(sketch, "E317", {"start": v(-7.3, -18.84) * mm, "end": v(-7.14, -18.69) * mm});
            skLineSegment(sketch, "E318", {"start": v(-7.14, -18.69) * mm, "end": v(-7, -18.52) * mm});
            skLineSegment(sketch, "E319", {"start": v(-7, -18.52) * mm, "end": v(-6.88, -18.35) * mm});
            skLineSegment(sketch, "E320", {"start": v(-6.88, -18.35) * mm, "end": v(-6.76, -18.18) * mm});
            skLineSegment(sketch, "E321", {"start": v(-6.76, -18.18) * mm, "end": v(-6.66, -18) * mm});
            skLineSegment(sketch, "E322", {"start": v(-6.66, -18) * mm, "end": v(-6.56, -17.81) * mm});
            skLineSegment(sketch, "E323", {"start": v(-6.56, -17.81) * mm, "end": v(-6.48, -17.63) * mm});
            skLineSegment(sketch, "E324", {"start": v(-6.48, -17.63) * mm, "end": v(-6.41, -17.44) * mm});
            skLineSegment(sketch, "E325", {"start": v(-6.41, -17.44) * mm, "end": v(-6.36, -17.25) * mm});
            skLineSegment(sketch, "E326", {"start": v(-6.36, -17.25) * mm, "end": v(-6.32, -17.06) * mm});
            skLineSegment(sketch, "E327", {"start": v(-6.32, -17.06) * mm, "end": v(-6.3, -16.88) * mm});
            skLineSegment(sketch, "E328", {"start": v(-6.3, -16.88) * mm, "end": v(-6.3, -16.7) * mm});
            skLineSegment(sketch, "E329", {"start": v(-6.3, -16.7) * mm, "end": v(-6.3, -16.51) * mm});
            skLineSegment(sketch, "E330", {"start": v(-6.3, -16.51) * mm, "end": v(-6.34, -16.33) * mm});
            skLineSegment(sketch, "E331", {"start": v(-6.34, -16.33) * mm, "end": v(-6.39, -16.13) * mm});
            skLineSegment(sketch, "E332", {"start": v(-6.39, -16.13) * mm, "end": v(-6.46, -15.92) * mm});
            skLineSegment(sketch, "E333", {"start": v(-6.46, -15.92) * mm, "end": v(-6.54, -15.7) * mm});
            skLineSegment(sketch, "E334", {"start": v(-6.54, -15.7) * mm, "end": v(-6.64, -15.47) * mm});
            skLineSegment(sketch, "E335", {"start": v(-6.64, -15.47) * mm, "end": v(-6.75, -15.24) * mm});
            skLineSegment(sketch, "E336", {"start": v(-6.75, -15.24) * mm, "end": v(-6.87, -15) * mm});
            skLineSegment(sketch, "E337", {"start": v(-6.87, -15) * mm, "end": v(-7, -14.75) * mm});
            skLineSegment(sketch, "E338", {"start": v(-7, -14.75) * mm, "end": v(-7.13, -14.5) * mm});
            skLineSegment(sketch, "E339", {"start": v(-7.13, -14.5) * mm, "end": v(-7.28, -14.24) * mm});
            skLineSegment(sketch, "E340", {"start": v(-7.28, -14.24) * mm, "end": v(-7.42, -13.99) * mm});
            skLineSegment(sketch, "E341", {"start": v(-7.42, -13.99) * mm, "end": v(-7.57, -13.73) * mm});
            skLineSegment(sketch, "E342", {"start": v(-7.57, -13.73) * mm, "end": v(-7.72, -13.48) * mm});
            skLineSegment(sketch, "E343", {"start": v(-7.72, -13.48) * mm, "end": v(-7.88, -13.23) * mm});
            skLineSegment(sketch, "E344", {"start": v(-7.88, -13.23) * mm, "end": v(-8.03, -12.98) * mm});
            skLineSegment(sketch, "E345", {"start": v(-8.03, -12.98) * mm, "end": v(-8.17, -12.73) * mm});
            skLineSegment(sketch, "E346", {"start": v(-8.17, -12.73) * mm, "end": v(-8.31, -12.5) * mm});
            skLineSegment(sketch, "E347", {"start": v(-8.31, -12.5) * mm, "end": v(-8.45, -12.26) * mm});
            skLineSegment(sketch, "E348", {"start": v(-8.45, -12.26) * mm, "end": v(-8.57, -12.04) * mm});
            skLineSegment(sketch, "E349", {"start": v(-8.57, -12.04) * mm, "end": v(-8.7, -11.82) * mm});
            skLineSegment(sketch, "E350", {"start": v(-8.7, -11.82) * mm, "end": v(-8.8, -11.62) * mm});
            skLineSegment(sketch, "E351", {"start": v(-8.8, -11.62) * mm, "end": v(-9.41, -10.7) * mm});
            skLineSegment(sketch, "E352", {"start": v(-7.57, -8.91) * mm, "end": v(-6.97, -9.86) * mm});
            skLineSegment(sketch, "E353", {"start": v(-6.97, -9.86) * mm, "end": v(-6.83, -10.07) * mm});
            skLineSegment(sketch, "E354", {"start": v(-6.83, -10.07) * mm, "end": v(-6.68, -10.26) * mm});
            skLineSegment(sketch, "E355", {"start": v(-6.68, -10.26) * mm, "end": v(-6.53, -10.46) * mm});
            skLineSegment(sketch, "E356", {"start": v(-6.53, -10.46) * mm, "end": v(-6.37, -10.65) * mm});
            skLineSegment(sketch, "E357", {"start": v(-6.37, -10.65) * mm, "end": v(-6.2, -10.83) * mm});
            skLineSegment(sketch, "E358", {"start": v(-6.2, -10.83) * mm, "end": v(-6.03, -11) * mm});
            skLineSegment(sketch, "E359", {"start": v(-6.03, -11) * mm, "end": v(-5.86, -11.17) * mm});
            skLineSegment(sketch, "E360", {"start": v(-5.86, -11.17) * mm, "end": v(-5.68, -11.34) * mm});
            skLineSegment(sketch, "E361", {"start": v(-5.68, -11.34) * mm, "end": v(-5.5, -11.5) * mm});
            skLineSegment(sketch, "E362", {"start": v(-5.5, -11.5) * mm, "end": v(-5.31, -11.65) * mm});
            skLineSegment(sketch, "E363", {"start": v(-5.31, -11.65) * mm, "end": v(-5.12, -11.8) * mm});
            skLineSegment(sketch, "E364", {"start": v(-5.12, -11.8) * mm, "end": v(-4.93, -11.94) * mm});
            skLineSegment(sketch, "E365", {"start": v(-4.93, -11.94) * mm, "end": v(-4.73, -12.07) * mm});
            skLineSegment(sketch, "E366", {"start": v(-4.73, -12.07) * mm, "end": v(-4.52, -12.2) * mm});
            skLineSegment(sketch, "E367", {"start": v(-4.52, -12.2) * mm, "end": v(-4.32, -12.32) * mm});
            skLineSegment(sketch, "E368", {"start": v(-4.32, -12.32) * mm, "end": v(-4.1, -12.44) * mm});
            skLineSegment(sketch, "E369", {"start": v(-4.1, -12.44) * mm, "end": v(-3.9, -12.55) * mm});
            skLineSegment(sketch, "E370", {"start": v(-3.9, -12.55) * mm, "end": v(-3.68, -12.65) * mm});
            skLineSegment(sketch, "E371", {"start": v(-3.68, -12.65) * mm, "end": v(-3.46, -12.75) * mm});
            skLineSegment(sketch, "E372", {"start": v(-3.46, -12.75) * mm, "end": v(-3.24, -12.83) * mm});
            skLineSegment(sketch, "E373", {"start": v(-3.24, -12.83) * mm, "end": v(-3.02, -12.92) * mm});
            skLineSegment(sketch, "E374", {"start": v(-3.02, -12.92) * mm, "end": v(-2.8, -13) * mm});
            skLineSegment(sketch, "E375", {"start": v(-2.8, -13) * mm, "end": v(-2.56, -13.06) * mm});
            skLineSegment(sketch, "E376", {"start": v(-2.56, -13.06) * mm, "end": v(-2.33, -13.13) * mm});
            skLineSegment(sketch, "E377", {"start": v(-2.33, -13.13) * mm, "end": v(-2.1, -13.18) * mm});
            skLineSegment(sketch, "E378", {"start": v(-2.1, -13.18) * mm, "end": v(-1.87, -13.23) * mm});
            skLineSegment(sketch, "E379", {"start": v(-1.87, -13.23) * mm, "end": v(-1.63, -13.27) * mm});
            skLineSegment(sketch, "E380", {"start": v(-1.63, -13.27) * mm, "end": v(-1.4, -13.3) * mm});
            skLineSegment(sketch, "E381", {"start": v(-1.4, -13.3) * mm, "end": v(-1.15, -13.33) * mm});
            skLineSegment(sketch, "E382", {"start": v(-1.15, -13.33) * mm, "end": v(-0.91, -13.35) * mm});
            skLineSegment(sketch, "E383", {"start": v(-0.91, -13.35) * mm, "end": v(-0.67, -13.37) * mm});
            skLineSegment(sketch, "E384", {"start": v(-0.67, -13.37) * mm, "end": v(-0.43, -13.37) * mm});
            skLineSegment(sketch, "E385", {"start": v(-0.43, -13.37) * mm, "end": v(-0.18, -13.37) * mm});
            skLineSegment(sketch, "E386", {"start": v(-0.18, -13.37) * mm, "end": v(0.06, -13.36) * mm});
            skLineSegment(sketch, "E387", {"start": v(0.06, -13.36) * mm, "end": v(0.3, -13.34) * mm});
            skLineSegment(sketch, "E388", {"start": v(0.3, -13.34) * mm, "end": v(0.55, -13.32) * mm});
            skLineSegment(sketch, "E389", {"start": v(0.55, -13.32) * mm, "end": v(0.8, -13.29) * mm});
            skLineSegment(sketch, "E390", {"start": v(0.8, -13.29) * mm, "end": v(1.04, -13.25) * mm});
            skLineSegment(sketch, "E391", {"start": v(1.04, -13.25) * mm, "end": v(1.29, -13.2) * mm});
            skLineSegment(sketch, "E392", {"start": v(1.29, -13.2) * mm, "end": v(1.53, -13.15) * mm});
            skLineSegment(sketch, "E393", {"start": v(1.53, -13.15) * mm, "end": v(1.78, -13.08) * mm});
            skLineSegment(sketch, "E394", {"start": v(1.78, -13.08) * mm, "end": v(2, -13.02) * mm});
            skLineSegment(sketch, "E395", {"start": v(2, -13.02) * mm, "end": v(2.22, -12.93) * mm});
            skLineSegment(sketch, "E396", {"start": v(2.22, -12.93) * mm, "end": v(2.44, -12.83) * mm});
            skLineSegment(sketch, "E397", {"start": v(2.44, -12.83) * mm, "end": v(2.66, -12.73) * mm});
            skLineSegment(sketch, "E398", {"start": v(2.66, -12.73) * mm, "end": v(2.88, -12.61) * mm});
            skLineSegment(sketch, "E399", {"start": v(2.88, -12.61) * mm, "end": v(3.1, -12.49) * mm});
            skLineSegment(sketch, "E400", {"start": v(3.1, -12.49) * mm, "end": v(3.33, -12.37) * mm});
            skLineSegment(sketch, "E401", {"start": v(3.33, -12.37) * mm, "end": v(3.55, -12.24) * mm});
            skLineSegment(sketch, "E402", {"start": v(3.55, -12.24) * mm, "end": v(3.78, -12.12) * mm});
            skLineSegment(sketch, "E403", {"start": v(3.78, -12.12) * mm, "end": v(4, -12.01) * mm});
            skLineSegment(sketch, "E404", {"start": v(4, -12.01) * mm, "end": v(4.23, -11.9) * mm});
            skLineSegment(sketch, "E405", {"start": v(4.23, -11.9) * mm, "end": v(4.46, -11.81) * mm});
            skLineSegment(sketch, "E406", {"start": v(4.46, -11.81) * mm, "end": v(4.68, -11.73) * mm});
            skLineSegment(sketch, "E407", {"start": v(4.68, -11.73) * mm, "end": v(4.9, -11.67) * mm});
            skLineSegment(sketch, "E408", {"start": v(4.9, -11.67) * mm, "end": v(5.53, -11.5) * mm});
            skLineSegment(sketch, "E409", {"start": v(12.27, -11.3) * mm, "end": v(12.4, -11.18) * mm});
            skLineSegment(sketch, "E410", {"start": v(12.4, -11.18) * mm, "end": v(12.52, -11.05) * mm});
            skLineSegment(sketch, "E411", {"start": v(12.52, -11.05) * mm, "end": v(12.62, -10.91) * mm});
            skLineSegment(sketch, "E412", {"start": v(12.62, -10.91) * mm, "end": v(12.7, -10.76) * mm});
            skLineSegment(sketch, "E413", {"start": v(12.7, -10.76) * mm, "end": v(12.75, -10.6) * mm});
            skLineSegment(sketch, "E414", {"start": v(12.75, -10.6) * mm, "end": v(12.79, -10.4) * mm});
            skLineSegment(sketch, "E415", {"start": v(12.79, -10.4) * mm, "end": v(12.8, -10.22) * mm});
            skLineSegment(sketch, "E416", {"start": v(12.8, -10.22) * mm, "end": v(12.8, -10.03) * mm});
            skLineSegment(sketch, "E417", {"start": v(12.8, -10.03) * mm, "end": v(12.78, -9.83) * mm});
            skLineSegment(sketch, "E418", {"start": v(12.78, -9.83) * mm, "end": v(12.75, -9.63) * mm});
            skLineSegment(sketch, "E419", {"start": v(12.75, -9.63) * mm, "end": v(12.7, -9.42) * mm});
            skLineSegment(sketch, "E420", {"start": v(12.7, -9.42) * mm, "end": v(12.64, -9.21) * mm});
            skLineSegment(sketch, "E421", {"start": v(6.57, -3.42) * mm, "end": v(6.1, -2.5) * mm});
            skLineSegment(sketch, "E422", {"start": v(6.1, -2.5) * mm, "end": v(5.9, -2.34) * mm});
            skLineSegment(sketch, "E423", {"start": v(5.9, -2.34) * mm, "end": v(5.71, -2.17) * mm});
            skLineSegment(sketch, "E424", {"start": v(5.71, -2.17) * mm, "end": v(5.55, -1.97) * mm});
            skLineSegment(sketch, "E425", {"start": v(5.55, -1.97) * mm, "end": v(5.42, -1.78) * mm});
            skLineSegment(sketch, "E426", {"start": v(5.42, -1.78) * mm, "end": v(5.3, -1.57) * mm});
            skLineSegment(sketch, "E427", {"start": v(5.3, -1.57) * mm, "end": v(5.18, -1.37) * mm});
            skLineSegment(sketch, "E428", {"start": v(5.18, -1.37) * mm, "end": v(5.09, -1.15) * mm});
            skLineSegment(sketch, "E429", {"start": v(5.09, -1.15) * mm, "end": v(5, -0.94) * mm});
            skLineSegment(sketch, "E430", {"start": v(5, -0.94) * mm, "end": v(4.93, -0.72) * mm});
            skLineSegment(sketch, "E431", {"start": v(4.93, -0.72) * mm, "end": v(4.86, -0.49) * mm});
            skLineSegment(sketch, "E432", {"start": v(4.86, -0.49) * mm, "end": v(4.81, -0.26) * mm});
            skLineSegment(sketch, "E433", {"start": v(4.81, -0.26) * mm, "end": v(4.77, -0.03) * mm});
            skLineSegment(sketch, "E434", {"start": v(4.77, -0.03) * mm, "end": v(4.74, 0.2) * mm});
            skLineSegment(sketch, "E435", {"start": v(4.74, 0.2) * mm, "end": v(4.71, 0.44) * mm});
            skLineSegment(sketch, "E436", {"start": v(4.71, 0.44) * mm, "end": v(4.7, 0.68) * mm});
            skLineSegment(sketch, "E437", {"start": v(4.7, 0.68) * mm, "end": v(4.7, 0.93) * mm});
            skLineSegment(sketch, "E438", {"start": v(4.7, 0.93) * mm, "end": v(4.7, 1.17) * mm});
            skLineSegment(sketch, "E439", {"start": v(4.7, 1.17) * mm, "end": v(4.7, 1.42) * mm});
            skLineSegment(sketch, "E440", {"start": v(4.7, 1.42) * mm, "end": v(4.72, 1.66) * mm});
            skLineSegment(sketch, "E441", {"start": v(4.72, 1.66) * mm, "end": v(4.74, 1.91) * mm});
            skLineSegment(sketch, "E442", {"start": v(4.74, 1.91) * mm, "end": v(4.77, 2.16) * mm});
            skLineSegment(sketch, "E443", {"start": v(4.77, 2.16) * mm, "end": v(4.8, 2.4) * mm});
            skLineSegment(sketch, "E444", {"start": v(4.8, 2.4) * mm, "end": v(4.84, 2.66) * mm});
            skLineSegment(sketch, "E445", {"start": v(4.84, 2.66) * mm, "end": v(4.88, 2.9) * mm});
            skLineSegment(sketch, "E446", {"start": v(4.88, 2.9) * mm, "end": v(4.93, 3.15) * mm});
            skLineSegment(sketch, "E447", {"start": v(4.93, 3.15) * mm, "end": v(4.98, 3.4) * mm});
            skLineSegment(sketch, "E448", {"start": v(4.98, 3.4) * mm, "end": v(5.04, 3.65) * mm});
            skLineSegment(sketch, "E449", {"start": v(5.04, 3.65) * mm, "end": v(5.1, 3.9) * mm});
            skLineSegment(sketch, "E450", {"start": v(5.1, 3.9) * mm, "end": v(5.15, 4.13) * mm});
            skLineSegment(sketch, "E451", {"start": v(5.15, 4.13) * mm, "end": v(5.22, 4.37) * mm});
            skLineSegment(sketch, "E452", {"start": v(5.22, 4.37) * mm, "end": v(5.28, 4.61) * mm});
            skLineSegment(sketch, "E453", {"start": v(5.28, 4.61) * mm, "end": v(5.34, 4.85) * mm});
            skLineSegment(sketch, "E454", {"start": v(5.34, 4.85) * mm, "end": v(5.4, 5.08) * mm});
            skLineSegment(sketch, "E455", {"start": v(5.4, 5.08) * mm, "end": v(5.47, 5.31) * mm});
            skLineSegment(sketch, "E456", {"start": v(5.47, 5.31) * mm, "end": v(5.54, 5.54) * mm});
            skLineSegment(sketch, "E457", {"start": v(5.54, 5.54) * mm, "end": v(5.6, 5.76) * mm});
            skLineSegment(sketch, "E458", {"start": v(5.6, 5.76) * mm, "end": v(5.67, 5.98) * mm});
            skLineSegment(sketch, "E459", {"start": v(5.67, 5.98) * mm, "end": v(5.73, 6.2) * mm});
            skLineSegment(sketch, "E460", {"start": v(5.73, 6.2) * mm, "end": v(5.79, 6.4) * mm});
            skLineSegment(sketch, "E461", {"start": v(5.79, 6.4) * mm, "end": v(5.84, 6.6) * mm});
            skLineSegment(sketch, "E462", {"start": v(5.84, 6.6) * mm, "end": v(3.3, 2.8) * mm});
            skLineSegment(sketch, "E463", {"start": v(3.3, 2.8) * mm, "end": v(3.05, 2.8) * mm});
            skLineSegment(sketch, "E464", {"start": v(3.05, 2.8) * mm, "end": v(3.05, 12.2) * mm});
            skLineSegment(sketch, "E465", {"start": v(3.05, 12.2) * mm, "end": v(2.87, 12.03) * mm});
            skLineSegment(sketch, "E466", {"start": v(2.87, 12.03) * mm, "end": v(2.7, 11.86) * mm});
            skLineSegment(sketch, "E467", {"start": v(2.7, 11.86) * mm, "end": v(2.53, 11.68) * mm});
            skLineSegment(sketch, "E468", {"start": v(2.53, 11.68) * mm, "end": v(2.38, 11.5) * mm});
            skLineSegment(sketch, "E469", {"start": v(2.38, 11.5) * mm, "end": v(2.23, 11.3) * mm});
            skLineSegment(sketch, "E470", {"start": v(2.23, 11.3) * mm, "end": v(2.09, 11.1) * mm});
            skLineSegment(sketch, "E471", {"start": v(2.09, 11.1) * mm, "end": v(1.95, 10.89) * mm});
            skLineSegment(sketch, "E472", {"start": v(1.95, 10.89) * mm, "end": v(1.82, 10.67) * mm});
            skLineSegment(sketch, "E473", {"start": v(1.82, 10.67) * mm, "end": v(1.7, 10.45) * mm});
            skLineSegment(sketch, "E474", {"start": v(1.7, 10.45) * mm, "end": v(1.6, 10.23) * mm});
            skLineSegment(sketch, "E475", {"start": v(1.6, 10.23) * mm, "end": v(1.49, 10) * mm});
            skLineSegment(sketch, "E476", {"start": v(1.49, 10) * mm, "end": v(1.39, 9.76) * mm});
            skLineSegment(sketch, "E477", {"start": v(1.39, 9.76) * mm, "end": v(1.3, 9.53) * mm});
            skLineSegment(sketch, "E478", {"start": v(1.3, 9.53) * mm, "end": v(1.21, 9.3) * mm});
            skLineSegment(sketch, "E479", {"start": v(1.21, 9.3) * mm, "end": v(1.14, 9.05) * mm});
            skLineSegment(sketch, "E480", {"start": v(1.14, 9.05) * mm, "end": v(1.07, 8.8) * mm});
            skLineSegment(sketch, "E481", {"start": v(1.07, 8.8) * mm, "end": v(1, 8.56) * mm});
            skLineSegment(sketch, "E482", {"start": v(1, 8.56) * mm, "end": v(0.95, 8.32) * mm});
            skLineSegment(sketch, "E483", {"start": v(0.95, 8.32) * mm, "end": v(0.9, 8.08) * mm});
            skLineSegment(sketch, "E484", {"start": v(0.9, 8.08) * mm, "end": v(0.85, 7.83) * mm});
            skLineSegment(sketch, "E485", {"start": v(0.85, 7.83) * mm, "end": v(0.82, 7.6) * mm});
            skLineSegment(sketch, "E486", {"start": v(0.82, 7.6) * mm, "end": v(0.79, 7.35) * mm});
            skLineSegment(sketch, "E487", {"start": v(0.79, 7.35) * mm, "end": v(0.76, 7.11) * mm});
            skLineSegment(sketch, "E488", {"start": v(0.76, 7.11) * mm, "end": v(0.5, 7.11) * mm});
            skLineSegment(sketch, "E489", {"start": v(0.5, 7.11) * mm, "end": v(-1.72, 13.97) * mm});
            skLineSegment(sketch, "E490", {"start": v(-1.72, 13.97) * mm, "end": v(-0.76, 19.56) * mm});
            skLineSegment(sketch, "E491", {"start": v(-2.03, 17.27) * mm, "end": v(-2.2, 17.02) * mm});
            skLineSegment(sketch, "E492", {"start": v(-2.2, 17.02) * mm, "end": v(-2.37, 16.78) * mm});
            skLineSegment(sketch, "E493", {"start": v(-2.37, 16.78) * mm, "end": v(-2.52, 16.53) * mm});
            skLineSegment(sketch, "E494", {"start": v(-2.52, 16.53) * mm, "end": v(-2.65, 16.3) * mm});
            skLineSegment(sketch, "E495", {"start": v(-2.65, 16.3) * mm, "end": v(-2.78, 16.06) * mm});
            skLineSegment(sketch, "E496", {"start": v(-2.78, 16.06) * mm, "end": v(-2.89, 15.83) * mm});
            skLineSegment(sketch, "E497", {"start": v(-2.89, 15.83) * mm, "end": v(-2.99, 15.6) * mm});
            skLineSegment(sketch, "E498", {"start": v(-2.99, 15.6) * mm, "end": v(-3.07, 15.39) * mm});
            skLineSegment(sketch, "E499", {"start": v(-3.07, 15.39) * mm, "end": v(-3.15, 15.16) * mm});
            skLineSegment(sketch, "E500", {"start": v(-3.15, 15.16) * mm, "end": v(-3.22, 14.95) * mm});
            skLineSegment(sketch, "E501", {"start": v(-3.22, 14.95) * mm, "end": v(-3.27, 14.73) * mm});
            skLineSegment(sketch, "E502", {"start": v(-3.27, 14.73) * mm, "end": v(-3.32, 14.52) * mm});
            skLineSegment(sketch, "E503", {"start": v(-3.32, 14.52) * mm, "end": v(-3.36, 14.3) * mm});
            skLineSegment(sketch, "E504", {"start": v(-3.36, 14.3) * mm, "end": v(-3.39, 14.1) * mm});
            skLineSegment(sketch, "E505", {"start": v(-3.39, 14.1) * mm, "end": v(-3.41, 13.88) * mm});
            skLineSegment(sketch, "E506", {"start": v(-3.41, 13.88) * mm, "end": v(-3.43, 13.67) * mm});
            skLineSegment(sketch, "E507", {"start": v(-3.43, 13.67) * mm, "end": v(-3.43, 13.46) * mm});
            skLineSegment(sketch, "E508", {"start": v(-3.43, 13.46) * mm, "end": v(-3.43, 13.25) * mm});
            skLineSegment(sketch, "E509", {"start": v(-3.43, 13.25) * mm, "end": v(-3.43, 13.04) * mm});
            skLineSegment(sketch, "E510", {"start": v(-3.43, 13.04) * mm, "end": v(-3.42, 12.83) * mm});
            skLineSegment(sketch, "E511", {"start": v(-3.42, 12.83) * mm, "end": v(-3.4, 12.62) * mm});
            skLineSegment(sketch, "E512", {"start": v(-3.4, 12.62) * mm, "end": v(-3.38, 12.41) * mm});
            skLineSegment(sketch, "E513", {"start": v(-3.38, 12.41) * mm, "end": v(-3.36, 12.2) * mm});
            skLineSegment(sketch, "E514", {"start": v(-3.36, 12.2) * mm, "end": v(-3.33, 11.99) * mm});
            skLineSegment(sketch, "E515", {"start": v(-3.33, 11.99) * mm, "end": v(-3.3, 11.77) * mm});
            skLineSegment(sketch, "E516", {"start": v(-3.3, 11.77) * mm, "end": v(-3.26, 11.55) * mm});
            skLineSegment(sketch, "E517", {"start": v(-3.26, 11.55) * mm, "end": v(-3.23, 11.33) * mm});
            skLineSegment(sketch, "E518", {"start": v(-3.23, 11.33) * mm, "end": v(-3.19, 11.1) * mm});
            skLineSegment(sketch, "E519", {"start": v(-3.19, 11.1) * mm, "end": v(-3.15, 10.88) * mm});
            skLineSegment(sketch, "E520", {"start": v(-3.15, 10.88) * mm, "end": v(-3.1, 10.65) * mm});
            skLineSegment(sketch, "E521", {"start": v(-3.1, 10.65) * mm, "end": v(-3.06, 10.42) * mm});
            skLineSegment(sketch, "E522", {"start": v(-3.06, 10.42) * mm, "end": v(-3.02, 10.18) * mm});
            skLineSegment(sketch, "E523", {"start": v(-3.02, 10.18) * mm, "end": v(-2.98, 9.94) * mm});
            skLineSegment(sketch, "E524", {"start": v(-2.98, 9.94) * mm, "end": v(-2.94, 9.7) * mm});
            skLineSegment(sketch, "E525", {"start": v(-2.94, 9.7) * mm, "end": v(-2.9, 9.44) * mm});
            skLineSegment(sketch, "E526", {"start": v(-2.9, 9.44) * mm, "end": v(-2.87, 9.18) * mm});
            skLineSegment(sketch, "E527", {"start": v(-2.87, 9.18) * mm, "end": v(-2.83, 8.92) * mm});
            skLineSegment(sketch, "E528", {"start": v(-2.83, 8.92) * mm, "end": v(-2.8, 8.65) * mm});
            skLineSegment(sketch, "E529", {"start": v(-2.8, 8.65) * mm, "end": v(-2.77, 8.38) * mm});
            skLineSegment(sketch, "E530", {"start": v(-2.77, 8.38) * mm, "end": v(-2.75, 8.11) * mm});
            skLineSegment(sketch, "E531", {"start": v(-2.75, 8.11) * mm, "end": v(-2.73, 7.85) * mm});
            skLineSegment(sketch, "E532", {"start": v(-2.73, 7.85) * mm, "end": v(-2.7, 7.59) * mm});
            skLineSegment(sketch, "E533", {"start": v(-2.7, 7.59) * mm, "end": v(-2.7, 7.33) * mm});
            skLineSegment(sketch, "E534", {"start": v(-2.7, 7.33) * mm, "end": v(-2.68, 7.07) * mm});
            skLineSegment(sketch, "E535", {"start": v(-2.68, 7.07) * mm, "end": v(-2.66, 6.81) * mm});
            skLineSegment(sketch, "E536", {"start": v(-2.66, 6.81) * mm, "end": v(-2.65, 6.56) * mm});
            skLineSegment(sketch, "E537", {"start": v(-2.65, 6.56) * mm, "end": v(-2.64, 6.3) * mm});
            skLineSegment(sketch, "E538", {"start": v(-2.64, 6.3) * mm, "end": v(-2.63, 6.05) * mm});
            skLineSegment(sketch, "E539", {"start": v(-2.63, 6.05) * mm, "end": v(-2.62, 5.8) * mm});
            skLineSegment(sketch, "E540", {"start": v(-2.62, 5.8) * mm, "end": v(-2.62, 5.55) * mm});
            skLineSegment(sketch, "E541", {"start": v(-2.62, 5.55) * mm, "end": v(-2.6, 5.3) * mm});
            skLineSegment(sketch, "E542", {"start": v(-2.6, 5.3) * mm, "end": v(-2.6, 5.05) * mm});
            skLineSegment(sketch, "E543", {"start": v(-2.6, 5.05) * mm, "end": v(-2.59, 4.8) * mm});
            skLineSegment(sketch, "E544", {"start": v(-2.59, 4.8) * mm, "end": v(-2.58, 4.56) * mm});
            skLineSegment(sketch, "E545", {"start": v(-2.58, 4.56) * mm, "end": v(-2.56, 4.31) * mm});
            skLineSegment(sketch, "E546", {"start": v(-2.56, 4.31) * mm, "end": v(-2.55, 4.06) * mm});
            skLineSegment(sketch, "E547", {"start": v(-2.55, 4.06) * mm, "end": v(-2.53, 3.82) * mm});
            skLineSegment(sketch, "E548", {"start": v(-2.53, 3.82) * mm, "end": v(-2.51, 3.57) * mm});
            skLineSegment(sketch, "E549", {"start": v(-2.51, 3.57) * mm, "end": v(-2.49, 3.32) * mm});
            skLineSegment(sketch, "E550", {"start": v(-2.49, 3.32) * mm, "end": v(-2.46, 3.07) * mm});
            skLineSegment(sketch, "E551", {"start": v(-2.46, 3.07) * mm, "end": v(-2.43, 2.82) * mm});
            skLineSegment(sketch, "E552", {"start": v(-2.43, 2.82) * mm, "end": v(-2.4, 2.57) * mm});
            skLineSegment(sketch, "E553", {"start": v(-2.4, 2.57) * mm, "end": v(-2.36, 2.32) * mm});
            skLineSegment(sketch, "E554", {"start": v(-2.36, 2.32) * mm, "end": v(-2.32, 2.06) * mm});
            skLineSegment(sketch, "E555", {"start": v(-2.32, 2.06) * mm, "end": v(-2.27, 1.8) * mm});
            skLineSegment(sketch, "E556", {"start": v(-2.27, 1.8) * mm, "end": v(-2.22, 1.55) * mm});
            skLineSegment(sketch, "E557", {"start": v(-2.22, 1.55) * mm, "end": v(-2.16, 1.29) * mm});
            skLineSegment(sketch, "E558", {"start": v(-2.16, 1.29) * mm, "end": v(-2.1, 1.03) * mm});
            skLineSegment(sketch, "E559", {"start": v(-2.1, 1.03) * mm, "end": v(-2.03, 0.76) * mm});
            skLineSegment(sketch, "E560", {"start": v(-2.03, 0.76) * mm, "end": v(-2.2, 0.94) * mm});
            skLineSegment(sketch, "E561", {"start": v(-2.2, 0.94) * mm, "end": v(-2.36, 1.12) * mm});
            skLineSegment(sketch, "E562", {"start": v(-2.36, 1.12) * mm, "end": v(-2.52, 1.3) * mm});
            skLineSegment(sketch, "E563", {"start": v(-2.52, 1.3) * mm, "end": v(-2.68, 1.5) * mm});
            skLineSegment(sketch, "E564", {"start": v(-2.68, 1.5) * mm, "end": v(-2.82, 1.69) * mm});
            skLineSegment(sketch, "E565", {"start": v(-2.82, 1.69) * mm, "end": v(-2.97, 1.9) * mm});
            skLineSegment(sketch, "E566", {"start": v(-2.97, 1.9) * mm, "end": v(-3.1, 2.1) * mm});
            skLineSegment(sketch, "E567", {"start": v(-3.1, 2.1) * mm, "end": v(-3.24, 2.3) * mm});
            skLineSegment(sketch, "E568", {"start": v(-3.24, 2.3) * mm, "end": v(-3.37, 2.52) * mm});
            skLineSegment(sketch, "E569", {"start": v(-3.37, 2.52) * mm, "end": v(-3.5, 2.74) * mm});
            skLineSegment(sketch, "E570", {"start": v(-3.5, 2.74) * mm, "end": v(-3.62, 2.96) * mm});
            skLineSegment(sketch, "E571", {"start": v(-3.62, 2.96) * mm, "end": v(-3.74, 3.18) * mm});
            skLineSegment(sketch, "E572", {"start": v(-3.74, 3.18) * mm, "end": v(-3.86, 3.41) * mm});
            skLineSegment(sketch, "E573", {"start": v(-3.86, 3.41) * mm, "end": v(-3.97, 3.64) * mm});
            skLineSegment(sketch, "E574", {"start": v(-3.97, 3.64) * mm, "end": v(-4.08, 3.87) * mm});
            skLineSegment(sketch, "E575", {"start": v(-4.08, 3.87) * mm, "end": v(-4.19, 4.1) * mm});
            skLineSegment(sketch, "E576", {"start": v(-4.19, 4.1) * mm, "end": v(-4.3, 4.34) * mm});
            skLineSegment(sketch, "E577", {"start": v(-4.3, 4.34) * mm, "end": v(-4.4, 4.58) * mm});
            skLineSegment(sketch, "E578", {"start": v(-4.4, 4.58) * mm, "end": v(-4.5, 4.82) * mm});
            skLineSegment(sketch, "E579", {"start": v(-4.5, 4.82) * mm, "end": v(-4.59, 5.06) * mm});
            skLineSegment(sketch, "E580", {"start": v(-4.59, 5.06) * mm, "end": v(-4.68, 5.3) * mm});
            skLineSegment(sketch, "E581", {"start": v(-4.68, 5.3) * mm, "end": v(-4.77, 5.53) * mm});
            skLineSegment(sketch, "E582", {"start": v(-4.77, 5.53) * mm, "end": v(-4.86, 5.77) * mm});
            skLineSegment(sketch, "E583", {"start": v(-4.86, 5.77) * mm, "end": v(-4.95, 6.01) * mm});
            skLineSegment(sketch, "E584", {"start": v(-4.95, 6.01) * mm, "end": v(-5.03, 6.25) * mm});
            skLineSegment(sketch, "E585", {"start": v(-5.03, 6.25) * mm, "end": v(-5.11, 6.49) * mm});
            skLineSegment(sketch, "E586", {"start": v(-5.11, 6.49) * mm, "end": v(-5.2, 6.72) * mm});
            skLineSegment(sketch, "E587", {"start": v(-5.2, 6.72) * mm, "end": v(-5.28, 6.96) * mm});
            skLineSegment(sketch, "E588", {"start": v(-5.28, 6.96) * mm, "end": v(-5.36, 7.2) * mm});
            skLineSegment(sketch, "E589", {"start": v(-5.36, 7.2) * mm, "end": v(-5.43, 7.42) * mm});
            skLineSegment(sketch, "E590", {"start": v(-5.43, 7.42) * mm, "end": v(-5.51, 7.65) * mm});
            skLineSegment(sketch, "E591", {"start": v(-5.51, 7.65) * mm, "end": v(-5.59, 7.87) * mm});
            skLineSegment(sketch, "E592", {"start": v(-5.59, 7.87) * mm, "end": v(-5.84, 7.87) * mm});
            skLineSegment(sketch, "E593", {"start": v(-6.6, 1.27) * mm, "end": v(-6.56, 1.02) * mm});
            skLineSegment(sketch, "E594", {"start": v(-6.56, 1.02) * mm, "end": v(-6.53, 0.77) * mm});
            skLineSegment(sketch, "E595", {"start": v(-6.53, 0.77) * mm, "end": v(-6.5, 0.52) * mm});
            skLineSegment(sketch, "E596", {"start": v(-6.5, 0.52) * mm, "end": v(-6.49, 0.27) * mm});
            skLineSegment(sketch, "E597", {"start": v(-6.49, 0.27) * mm, "end": v(-6.48, 0.02) * mm});
            skLineSegment(sketch, "E598", {"start": v(-6.48, 0.02) * mm, "end": v(-6.48, -0.22) * mm});
            skLineSegment(sketch, "E599", {"start": v(-6.48, -0.22) * mm, "end": v(-6.48, -0.47) * mm});
            skLineSegment(sketch, "E600", {"start": v(-6.48, -0.47) * mm, "end": v(-6.5, -0.71) * mm});
            skLineSegment(sketch, "E601", {"start": v(-6.5, -0.71) * mm, "end": v(-6.51, -0.96) * mm});
            skLineSegment(sketch, "E602", {"start": v(-6.51, -0.96) * mm, "end": v(-6.53, -1.2) * mm});
            skLineSegment(sketch, "E603", {"start": v(-6.53, -1.2) * mm, "end": v(-6.56, -1.44) * mm});
            skLineSegment(sketch, "E604", {"start": v(-6.56, -1.44) * mm, "end": v(-6.59, -1.68) * mm});
            skLineSegment(sketch, "E605", {"start": v(-6.59, -1.68) * mm, "end": v(-6.62, -1.92) * mm});
            skLineSegment(sketch, "E606", {"start": v(-6.62, -1.92) * mm, "end": v(-6.66, -2.16) * mm});
            skLineSegment(sketch, "E607", {"start": v(-6.66, -2.16) * mm, "end": v(-6.7, -2.4) * mm});
            skLineSegment(sketch, "E608", {"start": v(-6.7, -2.4) * mm, "end": v(-6.74, -2.64) * mm});
            skLineSegment(sketch, "E609", {"start": v(-6.74, -2.64) * mm, "end": v(-6.78, -2.88) * mm});
            skLineSegment(sketch, "E610", {"start": v(-6.78, -2.88) * mm, "end": v(-6.82, -3.12) * mm});
            skLineSegment(sketch, "E611", {"start": v(-6.82, -3.12) * mm, "end": v(-6.87, -3.36) * mm});
            skLineSegment(sketch, "E612", {"start": v(-6.87, -3.36) * mm, "end": v(-6.91, -3.6) * mm});
            skLineSegment(sketch, "E613", {"start": v(-6.91, -3.6) * mm, "end": v(-6.95, -3.83) * mm});
            skLineSegment(sketch, "E614", {"start": v(-6.95, -3.83) * mm, "end": v(-7, -4.07) * mm});
            skLineSegment(sketch, "E615", {"start": v(-7, -4.07) * mm, "end": v(-7.04, -4.3) * mm});
            skLineSegment(sketch, "E616", {"start": v(-7.04, -4.3) * mm, "end": v(-7.08, -4.54) * mm});
            skLineSegment(sketch, "E617", {"start": v(-7.08, -4.54) * mm, "end": v(-7.11, -4.78) * mm});
            skLineSegment(sketch, "E618", {"start": v(-6.85, -8.76) * mm, "end": v(-6.77, -8.97) * mm});
            skLineSegment(sketch, "E619", {"start": v(-6.77, -8.97) * mm, "end": v(-6.68, -9.18) * mm});
            skLineSegment(sketch, "E620", {"start": v(-6.68, -9.18) * mm, "end": v(-6.59, -9.38) * mm});
            skLineSegment(sketch, "E621", {"start": v(-6.59, -9.38) * mm, "end": v(-6.49, -9.57) * mm});
            skLineSegment(sketch, "E622", {"start": v(-6.49, -9.57) * mm, "end": v(-6.38, -9.76) * mm});
            skLineSegment(sketch, "E623", {"start": v(-6.38, -9.76) * mm, "end": v(-6.27, -9.94) * mm});
            skLineSegment(sketch, "E624", {"start": v(-6.27, -9.94) * mm, "end": v(-6.15, -10.12) * mm});
            skLineSegment(sketch, "E625", {"start": v(-6.15, -10.12) * mm, "end": v(-6.03, -10.29) * mm});
            skLineSegment(sketch, "E626", {"start": v(-6.03, -10.29) * mm, "end": v(-5.9, -10.45) * mm});
            skLineSegment(sketch, "E627", {"start": v(-5.9, -10.45) * mm, "end": v(-5.77, -10.61) * mm});
            skLineSegment(sketch, "E628", {"start": v(-5.77, -10.61) * mm, "end": v(-5.63, -10.76) * mm});
            skLineSegment(sketch, "E629", {"start": v(-5.63, -10.76) * mm, "end": v(-5.48, -10.91) * mm});
            skLineSegment(sketch, "E630", {"start": v(-5.48, -10.91) * mm, "end": v(-5.33, -11.05) * mm});
            skLineSegment(sketch, "E631", {"start": v(-5.33, -11.05) * mm, "end": v(-5.18, -11.2) * mm});
            skLineSegment(sketch, "E632", {"start": v(-5.18, -11.2) * mm, "end": v(-5.02, -11.32) * mm});
            skLineSegment(sketch, "E633", {"start": v(-5.02, -11.32) * mm, "end": v(-4.86, -11.45) * mm});
            skLineSegment(sketch, "E634", {"start": v(-4.86, -11.45) * mm, "end": v(-4.69, -11.57) * mm});
            skLineSegment(sketch, "E635", {"start": v(-4.69, -11.57) * mm, "end": v(-4.52, -11.68) * mm});
            skLineSegment(sketch, "E636", {"start": v(-4.52, -11.68) * mm, "end": v(-4.34, -11.79) * mm});
            skLineSegment(sketch, "E637", {"start": v(-4.34, -11.79) * mm, "end": v(-4.17, -11.9) * mm});
            skLineSegment(sketch, "E638", {"start": v(-4.17, -11.9) * mm, "end": v(-3.98, -11.99) * mm});
            skLineSegment(sketch, "E639", {"start": v(-3.98, -11.99) * mm, "end": v(-3.8, -12.08) * mm});
            skLineSegment(sketch, "E640", {"start": v(-3.8, -12.08) * mm, "end": v(-3.61, -12.17) * mm});
            skLineSegment(sketch, "E641", {"start": v(-3.61, -12.17) * mm, "end": v(-3.42, -12.25) * mm});
            skLineSegment(sketch, "E642", {"start": v(-3.42, -12.25) * mm, "end": v(-3.23, -12.32) * mm});
            skLineSegment(sketch, "E643", {"start": v(-3.23, -12.32) * mm, "end": v(-3.03, -12.4) * mm});
            skLineSegment(sketch, "E644", {"start": v(-3.03, -12.4) * mm, "end": v(-2.83, -12.45) * mm});
            skLineSegment(sketch, "E645", {"start": v(-2.83, -12.45) * mm, "end": v(-2.63, -12.51) * mm});
            skLineSegment(sketch, "E646", {"start": v(-2.63, -12.51) * mm, "end": v(-2.43, -12.57) * mm});
            skLineSegment(sketch, "E647", {"start": v(-2.43, -12.57) * mm, "end": v(-2.22, -12.61) * mm});
            skLineSegment(sketch, "E648", {"start": v(-2.22, -12.61) * mm, "end": v(-2.01, -12.65) * mm});
            skLineSegment(sketch, "E649", {"start": v(-2.01, -12.65) * mm, "end": v(-1.8, -12.7) * mm});
            skLineSegment(sketch, "E650", {"start": v(-1.8, -12.7) * mm, "end": v(-1.6, -12.72) * mm});
            skLineSegment(sketch, "E651", {"start": v(-1.6, -12.72) * mm, "end": v(-1.38, -12.75) * mm});
            skLineSegment(sketch, "E652", {"start": v(-1.38, -12.75) * mm, "end": v(-1.17, -12.77) * mm});
            skLineSegment(sketch, "E653", {"start": v(-1.17, -12.77) * mm, "end": v(-0.96, -12.78) * mm});
            skLineSegment(sketch, "E654", {"start": v(-0.96, -12.78) * mm, "end": v(-0.74, -12.8) * mm});
            skLineSegment(sketch, "E655", {"start": v(-0.74, -12.8) * mm, "end": v(-0.53, -12.8) * mm});
            skLineSegment(sketch, "E656", {"start": v(-0.53, -12.8) * mm, "end": v(-0.31, -12.8) * mm});
            skLineSegment(sketch, "E657", {"start": v(-0.31, -12.8) * mm, "end": v(-0.1, -12.79) * mm});
            skLineSegment(sketch, "E658", {"start": v(-0.1, -12.79) * mm, "end": v(0.12, -12.77) * mm});
            skLineSegment(sketch, "E659", {"start": v(0.12, -12.77) * mm, "end": v(0.33, -12.75) * mm});
            skLineSegment(sketch, "E660", {"start": v(0.33, -12.75) * mm, "end": v(0.55, -12.73) * mm});
            skLineSegment(sketch, "E661", {"start": v(0.55, -12.73) * mm, "end": v(0.76, -12.7) * mm});
            skLineSegment(sketch, "E662", {"start": v(0.76, -12.7) * mm, "end": v(0.98, -12.67) * mm});
            skLineSegment(sketch, "E663", {"start": v(0.98, -12.67) * mm, "end": v(1.19, -12.63) * mm});
            skLineSegment(sketch, "E664", {"start": v(1.19, -12.63) * mm, "end": v(1.4, -12.58) * mm});
            skLineSegment(sketch, "E665", {"start": v(1.4, -12.58) * mm, "end": v(1.61, -12.53) * mm});
            skLineSegment(sketch, "E666", {"start": v(1.61, -12.53) * mm, "end": v(1.82, -12.48) * mm});
            skLineSegment(sketch, "E667", {"start": v(1.82, -12.48) * mm, "end": v(2.03, -12.42) * mm});
            skLineSegment(sketch, "E668", {"start": v(2.03, -12.42) * mm, "end": v(2.24, -12.35) * mm});
            skLineSegment(sketch, "E669", {"start": v(2.24, -12.35) * mm, "end": v(2.44, -12.28) * mm});
            skLineSegment(sketch, "E670", {"start": v(2.44, -12.28) * mm, "end": v(2.65, -12.2) * mm});
            skLineSegment(sketch, "E671", {"start": v(2.65, -12.2) * mm, "end": v(2.85, -12.12) * mm});
            skLineSegment(sketch, "E672", {"start": v(2.85, -12.12) * mm, "end": v(3.05, -12.04) * mm});
            skLineSegment(sketch, "E673", {"start": v(3.05, -12.04) * mm, "end": v(3.24, -11.94) * mm});
            skLineSegment(sketch, "E674", {"start": v(3.24, -11.94) * mm, "end": v(3.44, -11.85) * mm});
            skLineSegment(sketch, "E675", {"start": v(3.44, -11.85) * mm, "end": v(3.63, -11.74) * mm});
            skLineSegment(sketch, "E676", {"start": v(3.63, -11.74) * mm, "end": v(3.82, -11.63) * mm});
            skLineSegment(sketch, "E677", {"start": v(3.82, -11.63) * mm, "end": v(4, -11.52) * mm});
            skLineSegment(sketch, "E678", {"start": v(4, -11.52) * mm, "end": v(4.19, -11.4) * mm});
            skLineSegment(sketch, "E679", {"start": v(4.19, -11.4) * mm, "end": v(4.36, -11.28) * mm});
            skLineSegment(sketch, "E680", {"start": v(4.36, -11.28) * mm, "end": v(4.54, -11.15) * mm});
            skLineSegment(sketch, "E681", {"start": v(4.54, -11.15) * mm, "end": v(4.73, -11) * mm});
            skLineSegment(sketch, "E682", {"start": v(4.73, -11) * mm, "end": v(4.9, -10.82) * mm});
            skLineSegment(sketch, "E683", {"start": v(4.9, -10.82) * mm, "end": v(5.04, -10.65) * mm});
            skLineSegment(sketch, "E684", {"start": v(5.04, -10.65) * mm, "end": v(5.16, -10.47) * mm});
            skLineSegment(sketch, "E685", {"start": v(5.16, -10.47) * mm, "end": v(5.26, -10.3) * mm});
            skLineSegment(sketch, "E686", {"start": v(5.26, -10.3) * mm, "end": v(5.34, -10.1) * mm});
            skLineSegment(sketch, "E687", {"start": v(6.1, -4.78) * mm, "end": v(6.03, -4.53) * mm});
            skLineSegment(sketch, "E688", {"start": v(6.03, -4.53) * mm, "end": v(5.97, -4.29) * mm});
            skLineSegment(sketch, "E689", {"start": v(5.97, -4.29) * mm, "end": v(5.9, -4.05) * mm});
            skLineSegment(sketch, "E690", {"start": v(5.9, -4.05) * mm, "end": v(5.83, -3.8) * mm});
            skLineSegment(sketch, "E691", {"start": v(5.83, -3.8) * mm, "end": v(5.76, -3.57) * mm});
            skLineSegment(sketch, "E692", {"start": v(5.76, -3.57) * mm, "end": v(5.7, -3.33) * mm});
            skLineSegment(sketch, "E693", {"start": v(5.7, -3.33) * mm, "end": v(5.62, -3.1) * mm});
            skLineSegment(sketch, "E694", {"start": v(5.62, -3.1) * mm, "end": v(5.56, -2.86) * mm});
            skLineSegment(sketch, "E695", {"start": v(5.56, -2.86) * mm, "end": v(5.5, -2.63) * mm});
            skLineSegment(sketch, "E696", {"start": v(5.5, -2.63) * mm, "end": v(5.42, -2.4) * mm});
            skLineSegment(sketch, "E697", {"start": v(5.42, -2.4) * mm, "end": v(5.36, -2.16) * mm});
            skLineSegment(sketch, "E698", {"start": v(5.36, -2.16) * mm, "end": v(5.3, -1.93) * mm});
            skLineSegment(sketch, "E699", {"start": v(5.3, -1.93) * mm, "end": v(5.23, -1.7) * mm});
            skLineSegment(sketch, "E700", {"start": v(5.23, -1.7) * mm, "end": v(5.17, -1.46) * mm});
            skLineSegment(sketch, "E701", {"start": v(5.17, -1.46) * mm, "end": v(5.11, -1.23) * mm});
            skLineSegment(sketch, "E702", {"start": v(5.11, -1.23) * mm, "end": v(5.06, -1) * mm});
            skLineSegment(sketch, "E703", {"start": v(5.06, -1) * mm, "end": v(5, -0.77) * mm});
            skLineSegment(sketch, "E704", {"start": v(5, -0.77) * mm, "end": v(4.95, -0.53) * mm});
            skLineSegment(sketch, "E705", {"start": v(4.95, -0.53) * mm, "end": v(4.9, -0.3) * mm});
            skLineSegment(sketch, "E706", {"start": v(4.9, -0.3) * mm, "end": v(4.85, -0.06) * mm});
            skLineSegment(sketch, "E707", {"start": v(4.85, -0.06) * mm, "end": v(4.8, 0.18) * mm});
            skLineSegment(sketch, "E708", {"start": v(4.8, 0.18) * mm, "end": v(4.76, 0.41) * mm});
            skLineSegment(sketch, "E709", {"start": v(4.76, 0.41) * mm, "end": v(4.72, 0.65) * mm});
            skLineSegment(sketch, "E710", {"start": v(4.72, 0.65) * mm, "end": v(4.68, 0.9) * mm});
            skLineSegment(sketch, "E711", {"start": v(4.68, 0.9) * mm, "end": v(4.65, 1.14) * mm});
            skLineSegment(sketch, "E712", {"start": v(4.65, 1.14) * mm, "end": v(4.62, 1.39) * mm});
            skLineSegment(sketch, "E713", {"start": v(4.62, 1.39) * mm, "end": v(4.6, 1.64) * mm});
            skLineSegment(sketch, "E714", {"start": v(4.6, 1.64) * mm, "end": v(4.57, 1.9) * mm});
            skLineSegment(sketch, "E715", {"start": v(4.57, 1.9) * mm, "end": v(4.55, 2.15) * mm});
            skLineSegment(sketch, "E716", {"start": v(4.55, 2.15) * mm, "end": v(4.54, 2.4) * mm});
            skLineSegment(sketch, "E717", {"start": v(4.54, 2.4) * mm, "end": v(4.53, 2.67) * mm});
            skLineSegment(sketch, "E718", {"start": v(4.53, 2.67) * mm, "end": v(4.52, 2.93) * mm});
            skLineSegment(sketch, "E719", {"start": v(4.52, 2.93) * mm, "end": v(4.52, 3.2) * mm});
            skLineSegment(sketch, "E720", {"start": v(4.52, 3.2) * mm, "end": v(4.53, 3.47) * mm});
            skLineSegment(sketch, "E721", {"start": v(4.53, 3.47) * mm, "end": v(4.54, 3.75) * mm});
            skLineSegment(sketch, "E722", {"start": v(4.54, 3.75) * mm, "end": v(4.55, 4.03) * mm});
            skLineSegment(sketch, "E723", {"start": v(4.55, 4.03) * mm, "end": v(4.57, 4.32) * mm});
            skLineSegment(sketch, "E724", {"start": v(4.57, 4.32) * mm, "end": v(4.32, 4.32) * mm});
            skLineSegment(sketch, "E725", {"start": v(2.03, 9.65) * mm, "end": v(1.78, 9.65) * mm});
            skLineSegment(sketch, "E726", {"start": v(1.78, 9.65) * mm, "end": v(0.25, 1.52) * mm});
            skLineSegment(sketch, "E727", {"start": v(0.25, 1.52) * mm, "end": v(0, 1.52) * mm});
            skLineSegment(sketch, "E728", {"start": v(0, 1.52) * mm, "end": v(0.2, 7.11) * mm});
            skLineSegment(sketch, "E729", {"start": v(0.2, 7.11) * mm, "end": v(-2.13, 13.2) * mm});
            skLineSegment(sketch, "E730", {"start": v(-2.13, 13.2) * mm, "end": v(-2.03, 17.27) * mm});
            skLineSegment(sketch, "E731", {"start": v(-7.62, 16.26) * mm, "end": v(-7.37, 7.62) * mm});
            skLineSegment(sketch, "E732", {"start": v(-7.37, 7.62) * mm, "end": v(-6.86, 7.62) * mm});
            skLineSegment(sketch, "E733", {"start": v(-6.86, 7.62) * mm, "end": v(-6.83, 7.84) * mm});
            skLineSegment(sketch, "E734", {"start": v(-6.83, 7.84) * mm, "end": v(-6.8, 8.06) * mm});
            skLineSegment(sketch, "E735", {"start": v(-6.8, 8.06) * mm, "end": v(-6.78, 8.29) * mm});
            skLineSegment(sketch, "E736", {"start": v(-6.78, 8.29) * mm, "end": v(-6.75, 8.52) * mm});
            skLineSegment(sketch, "E737", {"start": v(-6.75, 8.52) * mm, "end": v(-6.73, 8.75) * mm});
            skLineSegment(sketch, "E738", {"start": v(-6.73, 8.75) * mm, "end": v(-6.7, 9) * mm});
            skLineSegment(sketch, "E739", {"start": v(-6.7, 9) * mm, "end": v(-6.67, 9.23) * mm});
            skLineSegment(sketch, "E740", {"start": v(-6.67, 9.23) * mm, "end": v(-6.64, 9.48) * mm});
            skLineSegment(sketch, "E741", {"start": v(-6.64, 9.48) * mm, "end": v(-6.61, 9.73) * mm});
            skLineSegment(sketch, "E742", {"start": v(-6.61, 9.73) * mm, "end": v(-6.58, 9.97) * mm});
            skLineSegment(sketch, "E743", {"start": v(-6.58, 9.97) * mm, "end": v(-6.56, 10.23) * mm});
            skLineSegment(sketch, "E744", {"start": v(-6.56, 10.23) * mm, "end": v(-6.54, 10.48) * mm});
            skLineSegment(sketch, "E745", {"start": v(-6.54, 10.48) * mm, "end": v(-6.52, 10.73) * mm});
            skLineSegment(sketch, "E746", {"start": v(-6.52, 10.73) * mm, "end": v(-6.5, 10.99) * mm});
            skLineSegment(sketch, "E747", {"start": v(-6.5, 10.99) * mm, "end": v(-6.48, 11.24) * mm});
            skLineSegment(sketch, "E748", {"start": v(-6.48, 11.24) * mm, "end": v(-6.47, 11.5) * mm});
            skLineSegment(sketch, "E749", {"start": v(-6.47, 11.5) * mm, "end": v(-6.46, 11.76) * mm});
            skLineSegment(sketch, "E750", {"start": v(-6.46, 11.76) * mm, "end": v(-6.46, 12.01) * mm});
            skLineSegment(sketch, "E751", {"start": v(-6.46, 12.01) * mm, "end": v(-6.46, 12.27) * mm});
            skLineSegment(sketch, "E752", {"start": v(-6.46, 12.27) * mm, "end": v(-6.47, 12.53) * mm});
            skLineSegment(sketch, "E753", {"start": v(-6.47, 12.53) * mm, "end": v(-6.48, 12.78) * mm});
            skLineSegment(sketch, "E754", {"start": v(-6.48, 12.78) * mm, "end": v(-6.5, 13.03) * mm});
            skLineSegment(sketch, "E755", {"start": v(-6.5, 13.03) * mm, "end": v(-6.53, 13.28) * mm});
            skLineSegment(sketch, "E756", {"start": v(-6.53, 13.28) * mm, "end": v(-6.56, 13.53) * mm});
            skLineSegment(sketch, "E757", {"start": v(-6.56, 13.53) * mm, "end": v(-6.6, 13.78) * mm});
            skLineSegment(sketch, "E758", {"start": v(-6.6, 13.78) * mm, "end": v(-6.65, 14.02) * mm});
            skLineSegment(sketch, "E759", {"start": v(-6.65, 14.02) * mm, "end": v(-6.7, 14.27) * mm});
            skLineSegment(sketch, "E760", {"start": v(-6.7, 14.27) * mm, "end": v(-6.76, 14.5) * mm});
            skLineSegment(sketch, "E761", {"start": v(-6.76, 14.5) * mm, "end": v(-6.84, 14.74) * mm});
            skLineSegment(sketch, "E762", {"start": v(-6.84, 14.74) * mm, "end": v(-6.92, 14.97) * mm});
            skLineSegment(sketch, "E763", {"start": v(-6.92, 14.97) * mm, "end": v(-7, 15.2) * mm});
            skLineSegment(sketch, "E764", {"start": v(-7, 15.2) * mm, "end": v(-7.1, 15.42) * mm});
            skLineSegment(sketch, "E765", {"start": v(-7.1, 15.42) * mm, "end": v(-7.22, 15.64) * mm});
            skLineSegment(sketch, "E766", {"start": v(-7.22, 15.64) * mm, "end": v(-7.34, 15.85) * mm});
            skLineSegment(sketch, "E767", {"start": v(-7.34, 15.85) * mm, "end": v(-7.48, 16.05) * mm});
            skLineSegment(sketch, "E768", {"start": v(-7.48, 16.05) * mm, "end": v(-7.62, 16.26) * mm});
            skLineSegment(sketch, "E769", {"start": v(1.52, 16.26) * mm, "end": v(1.42, 16) * mm});
            skLineSegment(sketch, "E770", {"start": v(1.42, 16) * mm, "end": v(1.33, 15.74) * mm});
            skLineSegment(sketch, "E771", {"start": v(1.33, 15.74) * mm, "end": v(1.24, 15.5) * mm});
            skLineSegment(sketch, "E772", {"start": v(1.24, 15.5) * mm, "end": v(1.15, 15.25) * mm});
            skLineSegment(sketch, "E773", {"start": v(1.15, 15.25) * mm, "end": v(1.07, 15) * mm});
            skLineSegment(sketch, "E774", {"start": v(1.07, 15) * mm, "end": v(1, 14.77) * mm});
            skLineSegment(sketch, "E775", {"start": v(1, 14.77) * mm, "end": v(0.93, 14.53) * mm});
            skLineSegment(sketch, "E776", {"start": v(0.93, 14.53) * mm, "end": v(0.87, 14.3) * mm});
            skLineSegment(sketch, "E777", {"start": v(0.87, 14.3) * mm, "end": v(0.82, 14.06) * mm});
            skLineSegment(sketch, "E778", {"start": v(0.82, 14.06) * mm, "end": v(0.77, 13.83) * mm});
            skLineSegment(sketch, "E779", {"start": v(0.77, 13.83) * mm, "end": v(0.73, 13.6) * mm});
            skLineSegment(sketch, "E780", {"start": v(0.73, 13.6) * mm, "end": v(0.7, 13.37) * mm});
            skLineSegment(sketch, "E781", {"start": v(0.7, 13.37) * mm, "end": v(0.68, 13.14) * mm});
            skLineSegment(sketch, "E782", {"start": v(0.68, 13.14) * mm, "end": v(0.66, 12.9) * mm});
            skLineSegment(sketch, "E783", {"start": v(0.66, 12.9) * mm, "end": v(0.65, 12.67) * mm});
            skLineSegment(sketch, "E784", {"start": v(0.65, 12.67) * mm, "end": v(0.65, 12.44) * mm});
            skLineSegment(sketch, "E785", {"start": v(0.65, 12.44) * mm, "end": v(0.67, 12.2) * mm});
            skLineSegment(sketch, "E786", {"start": v(0.67, 12.2) * mm, "end": v(0.69, 11.96) * mm});
            skLineSegment(sketch, "E787", {"start": v(0.69, 11.96) * mm, "end": v(0.72, 11.71) * mm});
            skLineSegment(sketch, "E788", {"start": v(0.72, 11.71) * mm, "end": v(0.76, 11.46) * mm});
            skLineSegment(sketch, "E789", {"start": v(0.76, 11.46) * mm, "end": v(0.8, 11.2) * mm});
            skLineSegment(sketch, "E790", {"start": v(0.8, 11.2) * mm, "end": v(0.86, 10.95) * mm});
            skLineSegment(sketch, "E791", {"start": v(0.86, 10.95) * mm, "end": v(0.93, 10.68) * mm});
            skLineSegment(sketch, "E792", {"start": v(0.93, 10.68) * mm, "end": v(1.02, 10.41) * mm});
            skLineSegment(sketch, "E793", {"start": v(1.02, 10.41) * mm, "end": v(1.27, 10.41) * mm});
            skLineSegment(sketch, "E794", {"start": v(1.27, 10.41) * mm, "end": v(1.33, 10.66) * mm});
            skLineSegment(sketch, "E795", {"start": v(1.33, 10.66) * mm, "end": v(1.38, 10.9) * mm});
            skLineSegment(sketch, "E796", {"start": v(1.38, 10.9) * mm, "end": v(1.44, 11.15) * mm});
            skLineSegment(sketch, "E797", {"start": v(1.44, 11.15) * mm, "end": v(1.5, 11.4) * mm});
            skLineSegment(sketch, "E798", {"start": v(1.5, 11.4) * mm, "end": v(1.55, 11.64) * mm});
            skLineSegment(sketch, "E799", {"start": v(1.55, 11.64) * mm, "end": v(1.6, 11.88) * mm});
            skLineSegment(sketch, "E800", {"start": v(1.6, 11.88) * mm, "end": v(1.66, 12.12) * mm});
            skLineSegment(sketch, "E801", {"start": v(1.66, 12.12) * mm, "end": v(1.7, 12.36) * mm});
            skLineSegment(sketch, "E802", {"start": v(1.7, 12.36) * mm, "end": v(1.75, 12.6) * mm});
            skLineSegment(sketch, "E803", {"start": v(1.75, 12.6) * mm, "end": v(1.78, 12.85) * mm});
            skLineSegment(sketch, "E804", {"start": v(1.78, 12.85) * mm, "end": v(1.82, 13.09) * mm});
            skLineSegment(sketch, "E805", {"start": v(1.82, 13.09) * mm, "end": v(1.84, 13.33) * mm});
            skLineSegment(sketch, "E806", {"start": v(1.84, 13.33) * mm, "end": v(1.87, 13.57) * mm});
            skLineSegment(sketch, "E807", {"start": v(1.87, 13.57) * mm, "end": v(1.88, 13.81) * mm});
            skLineSegment(sketch, "E808", {"start": v(1.88, 13.81) * mm, "end": v(1.89, 14.05) * mm});
            skLineSegment(sketch, "E809", {"start": v(1.89, 14.05) * mm, "end": v(1.89, 14.3) * mm});
            skLineSegment(sketch, "E810", {"start": v(1.89, 14.3) * mm, "end": v(1.88, 14.54) * mm});
            skLineSegment(sketch, "E811", {"start": v(1.88, 14.54) * mm, "end": v(1.86, 14.78) * mm});
            skLineSegment(sketch, "E812", {"start": v(1.86, 14.78) * mm, "end": v(1.83, 15.03) * mm});
            skLineSegment(sketch, "E813", {"start": v(1.83, 15.03) * mm, "end": v(1.8, 15.27) * mm});
            skLineSegment(sketch, "E814", {"start": v(1.8, 15.27) * mm, "end": v(1.74, 15.52) * mm});
            skLineSegment(sketch, "E815", {"start": v(1.74, 15.52) * mm, "end": v(1.68, 15.76) * mm});
            skLineSegment(sketch, "E816", {"start": v(1.68, 15.76) * mm, "end": v(1.6, 16) * mm});
            skLineSegment(sketch, "E817", {"start": v(1.6, 16) * mm, "end": v(1.52, 16.26) * mm});
            skLineSegment(sketch, "E818", {"start": v(0, -5.33) * mm, "end": v(3.05, -5.08) * mm});
            skLineSegment(sketch, "E819", {"start": v(3.05, -5.08) * mm, "end": v(3.56, -2.8) * mm});
            skLineSegment(sketch, "E820", {"start": v(3.56, -2.8) * mm, "end": v(3.3, -2.87) * mm});
            skLineSegment(sketch, "E821", {"start": v(3.3, -2.87) * mm, "end": v(3.05, -2.95) * mm});
            skLineSegment(sketch, "E822", {"start": v(3.05, -2.95) * mm, "end": v(2.81, -3.03) * mm});
            skLineSegment(sketch, "E823", {"start": v(2.81, -3.03) * mm, "end": v(2.58, -3.12) * mm});
            skLineSegment(sketch, "E824", {"start": v(2.58, -3.12) * mm, "end": v(2.35, -3.22) * mm});
            skLineSegment(sketch, "E825", {"start": v(2.35, -3.22) * mm, "end": v(2.12, -3.32) * mm});
            skLineSegment(sketch, "E826", {"start": v(2.12, -3.32) * mm, "end": v(1.9, -3.44) * mm});
            skLineSegment(sketch, "E827", {"start": v(1.9, -3.44) * mm, "end": v(1.7, -3.56) * mm});
            skLineSegment(sketch, "E828", {"start": v(1.7, -3.56) * mm, "end": v(1.5, -3.69) * mm});
            skLineSegment(sketch, "E829", {"start": v(1.5, -3.69) * mm, "end": v(1.3, -3.83) * mm});
            skLineSegment(sketch, "E830", {"start": v(1.3, -3.83) * mm, "end": v(1.11, -3.98) * mm});
            skLineSegment(sketch, "E831", {"start": v(1.11, -3.98) * mm, "end": v(0.93, -4.13) * mm});
            skLineSegment(sketch, "E832", {"start": v(0.93, -4.13) * mm, "end": v(0.75, -4.3) * mm});
            skLineSegment(sketch, "E833", {"start": v(0.75, -4.3) * mm, "end": v(0.59, -4.49) * mm});
            skLineSegment(sketch, "E834", {"start": v(0.59, -4.49) * mm, "end": v(0.43, -4.68) * mm});
            skLineSegment(sketch, "E835", {"start": v(0.43, -4.68) * mm, "end": v(0.28, -4.88) * mm});
            skLineSegment(sketch, "E836", {"start": v(0.28, -4.88) * mm, "end": v(0.14, -5.1) * mm});
            skLineSegment(sketch, "E837", {"start": v(0.14, -5.1) * mm, "end": v(0, -5.33) * mm});
            skLineSegment(sketch, "E838", {"start": v(7.9, -11.55) * mm, "end": v(8.63, -11.42) * mm});
            skLineSegment(sketch, "E839", {"start": v(8.63, -11.42) * mm, "end": v(8.8, -11.62) * mm});
            skLineSegment(sketch, "E840", {"start": v(8.8, -11.62) * mm, "end": v(8.94, -11.74) * mm});
            skLineSegment(sketch, "E841", {"start": v(8.94, -11.74) * mm, "end": v(9.08, -11.8) * mm});
            skLineSegment(sketch, "E842", {"start": v(9.08, -11.8) * mm, "end": v(9.2, -11.82) * mm});
            skLineSegment(sketch, "E843", {"start": v(9.2, -11.82) * mm, "end": v(9.32, -11.78) * mm});
            skLineSegment(sketch, "E844", {"start": v(9.32, -11.78) * mm, "end": v(9.43, -11.7) * mm});
            skLineSegment(sketch, "E845", {"start": v(9.43, -11.7) * mm, "end": v(9.52, -11.58) * mm});
            skLineSegment(sketch, "E846", {"start": v(9.52, -11.58) * mm, "end": v(9.62, -11.44) * mm});
            skLineSegment(sketch, "E847", {"start": v(9.62, -11.44) * mm, "end": v(9.62, -11.44) * mm});
            skLineSegment(sketch, "E848", {"start": v(9.62, -11.44) * mm, "end": v(10.59, -11.52) * mm});
            skLineSegment(sketch, "E849", {"start": v(10.59, -11.52) * mm, "end": v(10.63, -11.53) * mm});
            skLineSegment(sketch, "E850", {"start": v(10.63, -11.53) * mm, "end": v(10.72, -11.65) * mm});
            skLineSegment(sketch, "E851", {"start": v(10.72, -11.65) * mm, "end": v(10.8, -11.74) * mm});
            skLineSegment(sketch, "E852", {"start": v(10.8, -11.74) * mm, "end": v(10.9, -11.8) * mm});
            skLineSegment(sketch, "E853", {"start": v(10.9, -11.8) * mm, "end": v(11, -11.82) * mm});
            skLineSegment(sketch, "E854", {"start": v(11, -11.82) * mm, "end": v(11.1, -11.82) * mm});
            skLineSegment(sketch, "E855", {"start": v(11.1, -11.82) * mm, "end": v(11.2, -11.78) * mm});
            skLineSegment(sketch, "E856", {"start": v(11.2, -11.78) * mm, "end": v(11.29, -11.7) * mm});
            skLineSegment(sketch, "E857", {"start": v(11.29, -11.7) * mm, "end": v(11.38, -11.6) * mm});
            skLineSegment(sketch, "E858", {"start": v(11.6, -11.56) * mm, "end": v(11.96, -11.4) * mm});
            skLineSegment(sketch, "E859", {"start": v(11.6, -11.56) * mm, "end": v(11.38, -11.6) * mm});
            skLineSegment(sketch, "E860", {"start": v(11.96, -11.4) * mm, "end": v(12.27, -11.3) * mm});
            skLineSegment(sketch, "E861", {"start": v(12.08, -9.07) * mm, "end": v(11.99, -8.87) * mm});
            skLineSegment(sketch, "E862", {"start": v(11.99, -8.87) * mm, "end": v(11.89, -8.67) * mm});
            skLineSegment(sketch, "E863", {"start": v(11.89, -8.67) * mm, "end": v(11.77, -8.48) * mm});
            skLineSegment(sketch, "E864", {"start": v(11.77, -8.48) * mm, "end": v(11.64, -8.3) * mm});
            skLineSegment(sketch, "E865", {"start": v(11.64, -8.3) * mm, "end": v(11.5, -8.12) * mm});
            skLineSegment(sketch, "E866", {"start": v(11.5, -8.12) * mm, "end": v(11.35, -7.95) * mm});
            skLineSegment(sketch, "E867", {"start": v(11.35, -7.95) * mm, "end": v(11.2, -7.78) * mm});
            skLineSegment(sketch, "E868", {"start": v(11.2, -7.78) * mm, "end": v(11.02, -7.63) * mm});
            skLineSegment(sketch, "E869", {"start": v(11.02, -7.63) * mm, "end": v(10.84, -7.48) * mm});
            skLineSegment(sketch, "E870", {"start": v(10.84, -7.48) * mm, "end": v(10.66, -7.34) * mm});
            skLineSegment(sketch, "E871", {"start": v(10.66, -7.34) * mm, "end": v(10.46, -7.21) * mm});
            skLineSegment(sketch, "E872", {"start": v(10.46, -7.21) * mm, "end": v(10.26, -7.09) * mm});
            skLineSegment(sketch, "E873", {"start": v(10.26, -7.09) * mm, "end": v(10.05, -6.98) * mm});
            skLineSegment(sketch, "E874", {"start": v(10.05, -6.98) * mm, "end": v(9.83, -6.87) * mm});
            skLineSegment(sketch, "E875", {"start": v(9.83, -6.87) * mm, "end": v(9.6, -6.77) * mm});
            skLineSegment(sketch, "E876", {"start": v(9.6, -6.77) * mm, "end": v(9.38, -6.68) * mm});
            skLineSegment(sketch, "E877", {"start": v(9.38, -6.68) * mm, "end": v(9.14, -6.6) * mm});
            skLineSegment(sketch, "E878", {"start": v(9.14, -6.6) * mm, "end": v(9.15, -6.35) * mm});
            skLineSegment(sketch, "E879", {"start": v(9.15, -6.35) * mm, "end": v(9.13, -6.1) * mm});
            skLineSegment(sketch, "E880", {"start": v(9.13, -6.1) * mm, "end": v(9.09, -5.87) * mm});
            skLineSegment(sketch, "E881", {"start": v(9.09, -5.87) * mm, "end": v(9.03, -5.64) * mm});
            skLineSegment(sketch, "E882", {"start": v(9.03, -5.64) * mm, "end": v(8.96, -5.42) * mm});
            skLineSegment(sketch, "E883", {"start": v(8.96, -5.42) * mm, "end": v(8.87, -5.21) * mm});
            skLineSegment(sketch, "E884", {"start": v(8.87, -5.21) * mm, "end": v(8.76, -5.02) * mm});
            skLineSegment(sketch, "E885", {"start": v(8.76, -5.02) * mm, "end": v(8.64, -4.83) * mm});
            skLineSegment(sketch, "E886", {"start": v(8.64, -4.83) * mm, "end": v(8.5, -4.65) * mm});
            skLineSegment(sketch, "E887", {"start": v(8.5, -4.65) * mm, "end": v(8.36, -4.48) * mm});
            skLineSegment(sketch, "E888", {"start": v(8.36, -4.48) * mm, "end": v(8.2, -4.32) * mm});
            skLineSegment(sketch, "E889", {"start": v(8.2, -4.32) * mm, "end": v(8.03, -4.17) * mm});
            skLineSegment(sketch, "E890", {"start": v(8.03, -4.17) * mm, "end": v(7.84, -4.03) * mm});
            skLineSegment(sketch, "E891", {"start": v(7.84, -4.03) * mm, "end": v(7.65, -3.9) * mm});
            skLineSegment(sketch, "E892", {"start": v(7.65, -3.9) * mm, "end": v(7.45, -3.78) * mm});
            skLineSegment(sketch, "E893", {"start": v(7.45, -3.78) * mm, "end": v(7.24, -3.67) * mm});
            skLineSegment(sketch, "E894", {"start": v(7.24, -3.67) * mm, "end": v(7.02, -3.58) * mm});
            skLineSegment(sketch, "E895", {"start": v(7.02, -3.58) * mm, "end": v(6.8, -3.5) * mm});
            skLineSegment(sketch, "E896", {"start": v(6.8, -3.5) * mm, "end": v(6.57, -3.42) * mm});
            skLineSegment(sketch, "E897", {"start": v(6.57, -3.42) * mm, "end": v(6.33, -3.35) * mm});
            skLineSegment(sketch, "E898", {"start": v(0.76, -4.57) * mm, "end": v(0.76, -4.83) * mm});
            skLineSegment(sketch, "E899", {"start": v(-5.08, -4.57) * mm, "end": v(-4.94, -4.83) * mm});
            skLineSegment(sketch, "E900", {"start": v(-4.94, -4.83) * mm, "end": v(-4.8, -5.05) * mm});
            skLineSegment(sketch, "E901", {"start": v(-4.8, -5.05) * mm, "end": v(-4.64, -5.24) * mm});
            skLineSegment(sketch, "E902", {"start": v(-4.64, -5.24) * mm, "end": v(-4.48, -5.41) * mm});
            skLineSegment(sketch, "E903", {"start": v(-4.48, -5.41) * mm, "end": v(-4.32, -5.55) * mm});
            skLineSegment(sketch, "E904", {"start": v(-4.32, -5.55) * mm, "end": v(-4.15, -5.67) * mm});
            skLineSegment(sketch, "E905", {"start": v(-4.15, -5.67) * mm, "end": v(-3.97, -5.76) * mm});
            skLineSegment(sketch, "E906", {"start": v(-3.97, -5.76) * mm, "end": v(-3.79, -5.83) * mm});
            skLineSegment(sketch, "E907", {"start": v(-3.79, -5.83) * mm, "end": v(-3.6, -5.87) * mm});
            skLineSegment(sketch, "E908", {"start": v(-3.6, -5.87) * mm, "end": v(-3.4, -5.9) * mm});
            skLineSegment(sketch, "E909", {"start": v(-3.4, -5.9) * mm, "end": v(-3.2, -5.91) * mm});
            skLineSegment(sketch, "E910", {"start": v(-3.2, -5.91) * mm, "end": v(-2.99, -5.9) * mm});
            skLineSegment(sketch, "E911", {"start": v(-2.99, -5.9) * mm, "end": v(-2.76, -5.88) * mm});
            skLineSegment(sketch, "E912", {"start": v(-2.76, -5.88) * mm, "end": v(-2.53, -5.85) * mm});
            skLineSegment(sketch, "E913", {"start": v(-2.53, -5.85) * mm, "end": v(-2.3, -5.8) * mm});
            skLineSegment(sketch, "E914", {"start": v(-2.3, -5.8) * mm, "end": v(-2.05, -5.74) * mm});
            skLineSegment(sketch, "E915", {"start": v(-2.05, -5.74) * mm, "end": v(-1.8, -5.67) * mm});
            skLineSegment(sketch, "E916", {"start": v(-1.8, -5.67) * mm, "end": v(-1.52, -5.59) * mm});
            skLineSegment(sketch, "E917", {"start": v(-1.52, -5.59) * mm, "end": v(-1.52, -5.08) * mm});
            skLineSegment(sketch, "E918", {"start": v(-1.52, -5.08) * mm, "end": v(-5.08, -4.57) * mm});
            skLineSegment(sketch, "E919", {"start": v(-10.16, -19.05) * mm, "end": v(-9.88, -19.03) * mm});
            skLineSegment(sketch, "E920", {"start": v(-9.65, -10.67) * mm, "end": v(-9.41, -10.7) * mm});
            skLineSegment(sketch, "E921", {"start": v(-9.41, -10.7) * mm, "end": v(-9.19, -10.7) * mm});
            skLineSegment(sketch, "E922", {"start": v(-9.19, -10.7) * mm, "end": v(-8.99, -10.68) * mm});
            skLineSegment(sketch, "E923", {"start": v(-8.99, -10.68) * mm, "end": v(-8.8, -10.64) * mm});
            skLineSegment(sketch, "E924", {"start": v(-8.8, -10.64) * mm, "end": v(-8.63, -10.59) * mm});
            skLineSegment(sketch, "E925", {"start": v(-8.63, -10.59) * mm, "end": v(-8.47, -10.52) * mm});
            skLineSegment(sketch, "E926", {"start": v(-8.47, -10.52) * mm, "end": v(-8.33, -10.43) * mm});
            skLineSegment(sketch, "E927", {"start": v(-8.33, -10.43) * mm, "end": v(-8.2, -10.33) * mm});
            skLineSegment(sketch, "E928", {"start": v(-8.2, -10.33) * mm, "end": v(-8.1, -10.22) * mm});
            skLineSegment(sketch, "E929", {"start": v(-8.1, -10.22) * mm, "end": v(-7.99, -10.1) * mm});
            skLineSegment(sketch, "E930", {"start": v(-7.99, -10.1) * mm, "end": v(-7.9, -9.96) * mm});
            skLineSegment(sketch, "E931", {"start": v(-7.9, -9.96) * mm, "end": v(-7.82, -9.8) * mm});
            skLineSegment(sketch, "E932", {"start": v(-7.82, -9.8) * mm, "end": v(-7.76, -9.64) * mm});
            skLineSegment(sketch, "E933", {"start": v(-7.76, -9.64) * mm, "end": v(-7.7, -9.47) * mm});
            skLineSegment(sketch, "E934", {"start": v(-7.7, -9.47) * mm, "end": v(-7.65, -9.3) * mm});
            skLineSegment(sketch, "E935", {"start": v(-7.65, -9.3) * mm, "end": v(-7.6, -9.1) * mm});
            skLineSegment(sketch, "E936", {"start": v(-7.6, -9.1) * mm, "end": v(-7.57, -8.91) * mm});
            skLineSegment(sketch, "E937", {"start": v(-4.32, -4.83) * mm, "end": v(-4.14, -5.07) * mm});
            skLineSegment(sketch, "E938", {"start": v(-4.14, -5.07) * mm, "end": v(-3.95, -5.25) * mm});
            skLineSegment(sketch, "E939", {"start": v(-3.95, -5.25) * mm, "end": v(-3.75, -5.38) * mm});
            skLineSegment(sketch, "E940", {"start": v(-3.75, -5.38) * mm, "end": v(-3.55, -5.46) * mm});
            skLineSegment(sketch, "E941", {"start": v(-3.55, -5.46) * mm, "end": v(-3.33, -5.5) * mm});
            skLineSegment(sketch, "E942", {"start": v(-3.33, -5.5) * mm, "end": v(-3.1, -5.5) * mm});
            skLineSegment(sketch, "E943", {"start": v(-3.1, -5.5) * mm, "end": v(-2.84, -5.47) * mm});
            skLineSegment(sketch, "E944", {"start": v(-2.84, -5.47) * mm, "end": v(-2.57, -5.41) * mm});
            skLineSegment(sketch, "E945", {"start": v(-2.57, -5.41) * mm, "end": v(-2.29, -5.33) * mm});
            skLineSegment(sketch, "E946", {"start": v(-3.3, -10.16) * mm, "end": v(2.03, -10.67) * mm});
            skLineSegment(sketch, "E947", {"start": v(2.03, -10.67) * mm, "end": v(2.8, -7.87) * mm});
            skLineSegment(sketch, "E948", {"start": v(2.8, -7.87) * mm, "end": v(2.6, -7.9) * mm});
            skLineSegment(sketch, "E949", {"start": v(2.6, -7.9) * mm, "end": v(2.38, -7.91) * mm});
            skLineSegment(sketch, "E950", {"start": v(2.38, -7.91) * mm, "end": v(2.15, -7.94) * mm});
            skLineSegment(sketch, "E951", {"start": v(2.15, -7.94) * mm, "end": v(1.92, -7.97) * mm});
            skLineSegment(sketch, "E952", {"start": v(1.92, -7.97) * mm, "end": v(1.67, -8) * mm});
            skLineSegment(sketch, "E953", {"start": v(1.67, -8) * mm, "end": v(1.42, -8.04) * mm});
            skLineSegment(sketch, "E954", {"start": v(1.42, -8.04) * mm, "end": v(1.17, -8.08) * mm});
            skLineSegment(sketch, "E955", {"start": v(1.17, -8.08) * mm, "end": v(0.9, -8.13) * mm});
            skLineSegment(sketch, "E956", {"start": v(0.9, -8.13) * mm, "end": v(0.64, -8.18) * mm});
            skLineSegment(sketch, "E957", {"start": v(0.64, -8.18) * mm, "end": v(0.38, -8.23) * mm});
            skLineSegment(sketch, "E958", {"start": v(0.38, -8.23) * mm, "end": v(0.1, -8.3) * mm});
            skLineSegment(sketch, "E959", {"start": v(0.1, -8.3) * mm, "end": v(-0.16, -8.36) * mm});
            skLineSegment(sketch, "E960", {"start": v(-0.16, -8.36) * mm, "end": v(-0.42, -8.43) * mm});
            skLineSegment(sketch, "E961", {"start": v(-0.42, -8.43) * mm, "end": v(-0.68, -8.51) * mm});
            skLineSegment(sketch, "E962", {"start": v(-0.68, -8.51) * mm, "end": v(-0.94, -8.6) * mm});
            skLineSegment(sketch, "E963", {"start": v(-0.94, -8.6) * mm, "end": v(-1.2, -8.69) * mm});
            skLineSegment(sketch, "E964", {"start": v(-1.2, -8.69) * mm, "end": v(-1.44, -8.78) * mm});
            skLineSegment(sketch, "E965", {"start": v(-1.44, -8.78) * mm, "end": v(-1.68, -8.89) * mm});
            skLineSegment(sketch, "E966", {"start": v(-1.68, -8.89) * mm, "end": v(-1.91, -9) * mm});
            skLineSegment(sketch, "E967", {"start": v(-1.91, -9) * mm, "end": v(-2.13, -9.11) * mm});
            skLineSegment(sketch, "E968", {"start": v(-2.13, -9.11) * mm, "end": v(-2.34, -9.24) * mm});
            skLineSegment(sketch, "E969", {"start": v(-2.34, -9.24) * mm, "end": v(-2.54, -9.37) * mm});
            skLineSegment(sketch, "E970", {"start": v(-2.54, -9.37) * mm, "end": v(-2.73, -9.51) * mm});
            skLineSegment(sketch, "E971", {"start": v(-2.73, -9.51) * mm, "end": v(-2.9, -9.66) * mm});
            skLineSegment(sketch, "E972", {"start": v(-2.9, -9.66) * mm, "end": v(-3.05, -9.82) * mm});
            skLineSegment(sketch, "E973", {"start": v(-3.05, -9.82) * mm, "end": v(-3.18, -9.99) * mm});
            skLineSegment(sketch, "E974", {"start": v(-3.18, -9.99) * mm, "end": v(-3.3, -10.16) * mm});
            skLineSegment(sketch, "E975", {"start": v(1.52, -8.38) * mm, "end": v(0.1, -8.64) * mm});
            skLineSegment(sketch, "E976", {"start": v(0.1, -8.8) * mm, "end": v(1.02, -8.64) * mm});
            skLineSegment(sketch, "E977", {"start": v(1.02, -8.64) * mm, "end": v(0, -8.9) * mm});
            skLineSegment(sketch, "E978", {"start": v(2.03, -8.38) * mm, "end": v(1.52, -8.38) * mm});
            skLineSegment(sketch, "E979", {"start": v(-2.29, -9.65) * mm, "end": v(-2.29, -9.9) * mm});
            skLineSegment(sketch, "E980", {"start": v(-2.29, -9.9) * mm, "end": v(-2.04, -9.91) * mm});
            skLineSegment(sketch, "E981", {"start": v(-2.04, -9.91) * mm, "end": v(-1.8, -9.92) * mm});
            skLineSegment(sketch, "E982", {"start": v(-1.8, -9.92) * mm, "end": v(-1.56, -9.93) * mm});
            skLineSegment(sketch, "E983", {"start": v(-1.56, -9.93) * mm, "end": v(-1.34, -9.93) * mm});
            skLineSegment(sketch, "E984", {"start": v(-1.34, -9.93) * mm, "end": v(-1.12, -9.92) * mm});
            skLineSegment(sketch, "E985", {"start": v(-1.12, -9.92) * mm, "end": v(-0.92, -9.88) * mm});
            skLineSegment(sketch, "E986", {"start": v(-0.92, -9.88) * mm, "end": v(-0.74, -9.82) * mm});
            skLineSegment(sketch, "E987", {"start": v(-0.25, -9.14) * mm, "end": v(-2.29, -9.65) * mm});
            skLineSegment(sketch, "E988", {"start": v(5.53, -11.5) * mm, "end": v(6.33, -11.63) * mm});
            skLineSegment(sketch, "E989", {"start": v(6.33, -11.63) * mm, "end": v(6.41, -11.76) * mm});
            skLineSegment(sketch, "E990", {"start": v(6.41, -11.76) * mm, "end": v(6.53, -11.88) * mm});
            skLineSegment(sketch, "E991", {"start": v(6.53, -11.88) * mm, "end": v(6.67, -11.98) * mm});
            skLineSegment(sketch, "E992", {"start": v(6.67, -11.98) * mm, "end": v(6.83, -12.05) * mm});
            skLineSegment(sketch, "E993", {"start": v(6.83, -12.05) * mm, "end": v(7, -12.1) * mm});
            skLineSegment(sketch, "E994", {"start": v(7, -12.1) * mm, "end": v(7.2, -12.11) * mm});
            skLineSegment(sketch, "E995", {"start": v(7.2, -12.11) * mm, "end": v(7.37, -12.08) * mm});
            skLineSegment(sketch, "E996", {"start": v(7.37, -12.08) * mm, "end": v(7.54, -12.01) * mm});
            skLineSegment(sketch, "E997", {"start": v(7.54, -12.01) * mm, "end": v(7.7, -11.9) * mm});
            skLineSegment(sketch, "E998", {"start": v(7.7, -11.9) * mm, "end": v(7.83, -11.71) * mm});
            skLineSegment(sketch, "E999", {"start": v(12.7, -9.42) * mm, "end": v(12.08, -9.07) * mm});
            skLineSegment(sketch, "E1000", {"start": v(7.9, -11.55) * mm, "end": v(7.83, -11.71) * mm});
            skCircle(sketch, "E1001.cCircle", {"center": v(-12.69, 2.52) * mm, "radius": 1.22 * mm, "construction": true});
            skLineSegment(sketch, "E1001.0", {"start": v(-11.94, 0.2) * mm, "end": v(-15.08, 3.04) * mm});
            skLineSegment(sketch, "E1001.1", {"start": v(-15.08, 3.04) * mm, "end": v(-11.04, 4.33) * mm});
            skLineSegment(sketch, "E1001.2", {"start": v(-11.04, 4.33) * mm, "end": v(-11.94, 0.2) * mm});
            skPoint(sketch, "E1001.0.midPoint", {"position": v(-13.5, 1.62) * mm});
            skCircle(sketch, "E1002.cCircle", {"center": v(-18.11, 3) * mm, "radius": 1.9 * mm, "construction": true});
            skLineSegment(sketch, "E1002.0", {"start": v(-20.77, 3.26) * mm, "end": v(-17.85, 5.65) * mm});
            skLineSegment(sketch, "E1002.1", {"start": v(-17.85, 5.65) * mm, "end": v(-15.45, 2.73) * mm});
            skLineSegment(sketch, "E1002.2", {"start": v(-15.45, 2.73) * mm, "end": v(-18.37, 0.33) * mm});
            skLineSegment(sketch, "E1002.3", {"start": v(-18.37, 0.33) * mm, "end": v(-20.77, 3.26) * mm});
            skPoint(sketch, "E1002.0.midPoint", {"position": v(-19.3, 4.46) * mm});
            skCircle(sketch, "E1003.cCircle", {"center": v(-12.69, 2.52) * mm, "radius": 0.65 * mm, "construction": true});
            skLineSegment(sketch, "E1003.0", {"start": v(-12.27, 1.3) * mm, "end": v(-13.96, 2.78) * mm});
            skLineSegment(sketch, "E1003.1", {"start": v(-13.96, 2.78) * mm, "end": v(-11.83, 3.5) * mm});
            skLineSegment(sketch, "E1003.2", {"start": v(-11.83, 3.5) * mm, "end": v(-12.27, 1.3) * mm});
            skPoint(sketch, "E1003.0.midPoint", {"position": v(-13.11, 2.04) * mm});
            skCircle(sketch, "E1004.cCircle", {"center": v(-18.11, 3) * mm, "radius": 1.33 * mm, "construction": true});
            skLineSegment(sketch, "E1004.0", {"start": v(-18.29, 1.12) * mm, "end": v(-19.98, 3.17) * mm});
            skLineSegment(sketch, "E1004.1", {"start": v(-19.98, 3.17) * mm, "end": v(-17.93, 4.87) * mm});
            skLineSegment(sketch, "E1004.2", {"start": v(-17.93, 4.87) * mm, "end": v(-16.24, 2.82) * mm});
            skLineSegment(sketch, "E1004.3", {"start": v(-16.24, 2.82) * mm, "end": v(-18.29, 1.12) * mm});
            skPoint(sketch, "E1004.0.midPoint", {"position": v(-19.14, 2.15) * mm});
            skLineSegment(sketch, "E1005", {"start": v(-13.41, 1.24) * mm, "end": v(-13.75, 1.56) * mm});
            skLineSegment(sketch, "E1006", {"start": v(-16.52, 1.7) * mm, "end": v(-16.96, 1.36) * mm});
            skArc(sketch, "E1007", {"start": v(-16.52, 1.7) * mm, "mid": v(-15.16, 1.18) * mm, "end": v(-13.75, 1.56) * mm});
            skArc(sketch, "E1008", {"start": v(-16.96, 1.36) * mm, "mid": v(-15.2, 0.7) * mm, "end": v(-13.41, 1.24) * mm});
            skLineSegment(sketch, "E1009", {"start": v(-12.9, 3.85) * mm, "end": v(-13.32, 3.71) * mm});
            skLineSegment(sketch, "E1010", {"start": v(-16.43, 4.1) * mm, "end": v(-16.73, 4.47) * mm});
            skArc(sketch, "E1011", {"start": v(-13.32, 3.71) * mm, "mid": v(-14.77, 4.76) * mm, "end": v(-16.43, 4.1) * mm});
            skArc(sketch, "E1012", {"start": v(-12.9, 3.85) * mm, "mid": v(-14.64, 5.26) * mm, "end": v(-16.73, 4.47) * mm});
            skText(sketch, "E1013", { "text": "58", "fontName": "NotoSansCJKsc-Bold.otf"});
            const initialGuessF5  = {"E1013": [0.01016, 0, 1, 0, 0.00483]};
            skSetInitialGuess(sketch, initialGuessF5);
            skSolve(sketch);
        }
        {
            var Q0;
            Q0 = qSketchRegion(id + "F5", true);
            extrude(context, id + "F6", {"entities" : qUnion([Q0]), "depth" : 0.76 * mm});
        }
        {
            var Q0;
            Q0=makeQuery(id+"F6.opExtrude","SWEPT_BODY",BODY,{"disambiguationData":[OSD([sQuery(id+"F5.wireOp",EDGE,"E58"),sQuery(id+"F5.wireOp",EDGE,"E59"),sQuery(id+"F5.wireOp",EDGE,"E60"),sQuery(id+"F5.wireOp",EDGE,"E61"),sQuery(id+"F5.wireOp",EDGE,"E62"),sQuery(id+"F5.wireOp",EDGE,"E63"),sQuery(id+"F5.wireOp",EDGE,"E64"),sQuery(id+"F5.wireOp",EDGE,"E65"),sQuery(id+"F5.wireOp",EDGE,"E66"),sQuery(id+"F5.wireOp",EDGE,"E67"),sQuery(id+"F5.wireOp",EDGE,"E68"),sQuery(id+"F5.wireOp",EDGE,"E69"),sQuery(id+"F5.wireOp",EDGE,"E70"),sQuery(id+"F5.wireOp",EDGE,"E71"),sQuery(id+"F5.wireOp",EDGE,"E72"),sQuery(id+"F5.wireOp",EDGE,"E73"),sQuery(id+"F5.wireOp",EDGE,"E74"),sQuery(id+"F5.wireOp",EDGE,"E75"),sQuery(id+"F5.wireOp",EDGE,"E76"),sQuery(id+"F5.wireOp",EDGE,"E77"),sQuery(id+"F5.wireOp",EDGE,"E78"),sQuery(id+"F5.wireOp",EDGE,"E79"),sQuery(id+"F5.wireOp",EDGE,"E80"),sQuery(id+"F5.wireOp",EDGE,"E81"),sQuery(id+"F5.wireOp",EDGE,"E82"),sQuery(id+"F5.wireOp",EDGE,"E83"),sQuery(id+"F5.wireOp",EDGE,"E84"),sQuery(id+"F5.wireOp",EDGE,"E85"),sQuery(id+"F5.wireOp",EDGE,"E86"),sQuery(id+"F5.wireOp",EDGE,"E87"),sQuery(id+"F5.wireOp",EDGE,"E88"),sQuery(id+"F5.wireOp",EDGE,"E89"),sQuery(id+"F5.wireOp",EDGE,"E90"),sQuery(id+"F5.wireOp",EDGE,"E91"),sQuery(id+"F5.wireOp",EDGE,"E92"),sQuery(id+"F5.wireOp",EDGE,"E93"),sQuery(id+"F5.wireOp",EDGE,"E94"),sQuery(id+"F5.wireOp",EDGE,"E95"),sQuery(id+"F5.wireOp",EDGE,"E96"),sQuery(id+"F5.wireOp",EDGE,"E97"),sQuery(id+"F5.wireOp",EDGE,"E98"),sQuery(id+"F5.wireOp",EDGE,"E99"),sQuery(id+"F5.wireOp",EDGE,"E100"),sQuery(id+"F5.wireOp",EDGE,"E101"),sQuery(id+"F5.wireOp",EDGE,"E102"),sQuery(id+"F5.wireOp",EDGE,"E103"),sQuery(id+"F5.wireOp",EDGE,"E104"),sQuery(id+"F5.wireOp",EDGE,"E105"),sQuery(id+"F5.wireOp",EDGE,"E106"),sQuery(id+"F5.wireOp",EDGE,"E107"),sQuery(id+"F5.wireOp",EDGE,"E108"),sQuery(id+"F5.wireOp",EDGE,"E109"),sQuery(id+"F5.wireOp",EDGE,"E110"),sQuery(id+"F5.wireOp",EDGE,"E111"),sQuery(id+"F5.wireOp",EDGE,"E112"),sQuery(id+"F5.wireOp",EDGE,"E113"),sQuery(id+"F5.wireOp",EDGE,"E114"),sQuery(id+"F5.wireOp",EDGE,"E115"),sQuery(id+"F5.wireOp",EDGE,"E116"),sQuery(id+"F5.wireOp",EDGE,"E117"),sQuery(id+"F5.wireOp",EDGE,"E118"),sQuery(id+"F5.wireOp",EDGE,"E119"),sQuery(id+"F5.wireOp",EDGE,"E120"),sQuery(id+"F5.wireOp",EDGE,"E121"),sQuery(id+"F5.wireOp",EDGE,"E122"),sQuery(id+"F5.wireOp",EDGE,"E123"),sQuery(id+"F5.wireOp",EDGE,"E124"),sQuery(id+"F5.wireOp",EDGE,"E125"),sQuery(id+"F5.wireOp",EDGE,"E126"),sQuery(id+"F5.wireOp",EDGE,"E127"),sQuery(id+"F5.wireOp",EDGE,"E128"),sQuery(id+"F5.wireOp",EDGE,"E129"),sQuery(id+"F5.wireOp",EDGE,"E130"),sQuery(id+"F5.wireOp",EDGE,"E131"),sQuery(id+"F5.wireOp",EDGE,"E132"),sQuery(id+"F5.wireOp",EDGE,"E133"),sQuery(id+"F5.wireOp",EDGE,"E134"),sQuery(id+"F5.wireOp",EDGE,"E135"),sQuery(id+"F5.wireOp",EDGE,"E136"),sQuery(id+"F5.wireOp",EDGE,"E137"),sQuery(id+"F5.wireOp",EDGE,"E138"),sQuery(id+"F5.wireOp",EDGE,"E139"),sQuery(id+"F5.wireOp",EDGE,"E140"),sQuery(id+"F5.wireOp",EDGE,"E141"),sQuery(id+"F5.wireOp",EDGE,"E142"),sQuery(id+"F5.wireOp",EDGE,"E143"),sQuery(id+"F5.wireOp",EDGE,"E144"),sQuery(id+"F5.wireOp",EDGE,"E145"),sQuery(id+"F5.wireOp",EDGE,"E146"),sQuery(id+"F5.wireOp",EDGE,"E147"),sQuery(id+"F5.wireOp",EDGE,"E148"),sQuery(id+"F5.wireOp",EDGE,"E149"),sQuery(id+"F5.wireOp",EDGE,"E150"),sQuery(id+"F5.wireOp",EDGE,"E151"),sQuery(id+"F5.wireOp",EDGE,"E152"),sQuery(id+"F5.wireOp",EDGE,"E153"),sQuery(id+"F5.wireOp",EDGE,"E154"),sQuery(id+"F5.wireOp",EDGE,"E155"),sQuery(id+"F5.wireOp",EDGE,"E156"),sQuery(id+"F5.wireOp",EDGE,"E157"),sQuery(id+"F5.wireOp",EDGE,"E158"),sQuery(id+"F5.wireOp",EDGE,"E159"),sQuery(id+"F5.wireOp",EDGE,"E160"),sQuery(id+"F5.wireOp",EDGE,"E161"),sQuery(id+"F5.wireOp",EDGE,"E162"),sQuery(id+"F5.wireOp",EDGE,"E163"),sQuery(id+"F5.wireOp",EDGE,"E164"),sQuery(id+"F5.wireOp",EDGE,"E165"),sQuery(id+"F5.wireOp",EDGE,"E166"),sQuery(id+"F5.wireOp",EDGE,"E167"),sQuery(id+"F5.wireOp",EDGE,"E168"),sQuery(id+"F5.wireOp",EDGE,"E169"),sQuery(id+"F5.wireOp",EDGE,"E170"),sQuery(id+"F5.wireOp",EDGE,"E171"),sQuery(id+"F5.wireOp",EDGE,"E172"),sQuery(id+"F5.wireOp",EDGE,"E173"),sQuery(id+"F5.wireOp",EDGE,"E174"),sQuery(id+"F5.wireOp",EDGE,"E175"),sQuery(id+"F5.wireOp",EDGE,"E176"),sQuery(id+"F5.wireOp",EDGE,"E177"),sQuery(id+"F5.wireOp",EDGE,"E178"),sQuery(id+"F5.wireOp",EDGE,"E179"),sQuery(id+"F5.wireOp",EDGE,"E180"),sQuery(id+"F5.wireOp",EDGE,"E181"),sQuery(id+"F5.wireOp",EDGE,"E182"),sQuery(id+"F5.wireOp",EDGE,"E183"),sQuery(id+"F5.wireOp",EDGE,"E184"),sQuery(id+"F5.wireOp",EDGE,"E185"),sQuery(id+"F5.wireOp",EDGE,"E186"),sQuery(id+"F5.wireOp",EDGE,"E187"),sQuery(id+"F5.wireOp",EDGE,"E188"),sQuery(id+"F5.wireOp",EDGE,"E189"),sQuery(id+"F5.wireOp",EDGE,"E190"),sQuery(id+"F5.wireOp",EDGE,"E191"),sQuery(id+"F5.wireOp",EDGE,"E192"),sQuery(id+"F5.wireOp",EDGE,"E193"),sQuery(id+"F5.wireOp",EDGE,"E194"),sQuery(id+"F5.wireOp",EDGE,"E195"),sQuery(id+"F5.wireOp",EDGE,"E196"),sQuery(id+"F5.wireOp",EDGE,"E197"),sQuery(id+"F5.wireOp",EDGE,"E198"),sQuery(id+"F5.wireOp",EDGE,"E199"),sQuery(id+"F5.wireOp",EDGE,"E200"),sQuery(id+"F5.wireOp",EDGE,"E201"),sQuery(id+"F5.wireOp",EDGE,"E202"),sQuery(id+"F5.wireOp",EDGE,"E203"),sQuery(id+"F5.wireOp",EDGE,"E204"),sQuery(id+"F5.wireOp",EDGE,"E205"),sQuery(id+"F5.wireOp",EDGE,"E206"),sQuery(id+"F5.wireOp",EDGE,"E207"),sQuery(id+"F5.wireOp",EDGE,"E208"),sQuery(id+"F5.wireOp",EDGE,"E209"),sQuery(id+"F5.wireOp",EDGE,"E210"),sQuery(id+"F5.wireOp",EDGE,"E211"),sQuery(id+"F5.wireOp",EDGE,"E212"),sQuery(id+"F5.wireOp",EDGE,"E213"),sQuery(id+"F5.wireOp",EDGE,"E214"),sQuery(id+"F5.wireOp",EDGE,"E215"),sQuery(id+"F5.wireOp",EDGE,"E216"),sQuery(id+"F5.wireOp",EDGE,"E217"),sQuery(id+"F5.wireOp",EDGE,"E218"),sQuery(id+"F5.wireOp",EDGE,"E219"),sQuery(id+"F5.wireOp",EDGE,"E220"),sQuery(id+"F5.wireOp",EDGE,"E221"),sQuery(id+"F5.wireOp",EDGE,"E222"),sQuery(id+"F5.wireOp",EDGE,"E223"),sQuery(id+"F5.wireOp",EDGE,"E224"),sQuery(id+"F5.wireOp",EDGE,"E225"),sQuery(id+"F5.wireOp",EDGE,"E226"),sQuery(id+"F5.wireOp",EDGE,"E227"),sQuery(id+"F5.wireOp",EDGE,"E228"),sQuery(id+"F5.wireOp",EDGE,"E229"),sQuery(id+"F5.wireOp",EDGE,"E230"),sQuery(id+"F5.wireOp",EDGE,"E231"),sQuery(id+"F5.wireOp",EDGE,"E232"),sQuery(id+"F5.wireOp",EDGE,"E233"),sQuery(id+"F5.wireOp",EDGE,"E234"),sQuery(id+"F5.wireOp",EDGE,"E235"),sQuery(id+"F5.wireOp",EDGE,"E236"),sQuery(id+"F5.wireOp",EDGE,"E237"),sQuery(id+"F5.wireOp",EDGE,"E238"),sQuery(id+"F5.wireOp",EDGE,"E239"),sQuery(id+"F5.wireOp",EDGE,"E240"),sQuery(id+"F5.wireOp",EDGE,"E241"),sQuery(id+"F5.wireOp",EDGE,"E242"),sQuery(id+"F5.wireOp",EDGE,"E243"),sQuery(id+"F5.wireOp",EDGE,"E244"),sQuery(id+"F5.wireOp",EDGE,"E245"),sQuery(id+"F5.wireOp",EDGE,"E246"),sQuery(id+"F5.wireOp",EDGE,"E247"),sQuery(id+"F5.wireOp",EDGE,"E248"),sQuery(id+"F5.wireOp",EDGE,"E249"),sQuery(id+"F5.wireOp",EDGE,"E250"),sQuery(id+"F5.wireOp",EDGE,"E251"),sQuery(id+"F5.wireOp",EDGE,"E252"),sQuery(id+"F5.wireOp",EDGE,"E253"),sQuery(id+"F5.wireOp",EDGE,"E254"),sQuery(id+"F5.wireOp",EDGE,"E255"),sQuery(id+"F5.wireOp",EDGE,"E256"),sQuery(id+"F5.wireOp",EDGE,"E257"),sQuery(id+"F5.wireOp",EDGE,"E258"),sQuery(id+"F5.wireOp",EDGE,"E259"),sQuery(id+"F5.wireOp",EDGE,"E260"),sQuery(id+"F5.wireOp",EDGE,"E261"),sQuery(id+"F5.wireOp",EDGE,"E262"),sQuery(id+"F5.wireOp",EDGE,"E263"),sQuery(id+"F5.wireOp",EDGE,"E264"),sQuery(id+"F5.wireOp",EDGE,"E265"),sQuery(id+"F5.wireOp",EDGE,"E266"),sQuery(id+"F5.wireOp",EDGE,"E267"),sQuery(id+"F5.wireOp",EDGE,"E268"),sQuery(id+"F5.wireOp",EDGE,"E269"),sQuery(id+"F5.wireOp",EDGE,"E270"),sQuery(id+"F5.wireOp",EDGE,"E271"),sQuery(id+"F5.wireOp",EDGE,"E272"),sQuery(id+"F5.wireOp",EDGE,"E273"),sQuery(id+"F5.wireOp",EDGE,"E274"),sQuery(id+"F5.wireOp",EDGE,"E275"),sQuery(id+"F5.wireOp",EDGE,"E276"),sQuery(id+"F5.wireOp",EDGE,"E277"),sQuery(id+"F5.wireOp",EDGE,"E278"),sQuery(id+"F5.wireOp",EDGE,"E279"),sQuery(id+"F5.wireOp",EDGE,"E280"),sQuery(id+"F5.wireOp",EDGE,"E281"),sQuery(id+"F5.wireOp",EDGE,"E282"),sQuery(id+"F5.wireOp",EDGE,"E283"),sQuery(id+"F5.wireOp",EDGE,"E284"),sQuery(id+"F5.wireOp",EDGE,"E285"),sQuery(id+"F5.wireOp",EDGE,"E286"),sQuery(id+"F5.wireOp",EDGE,"E287"),sQuery(id+"F5.wireOp",EDGE,"E288"),sQuery(id+"F5.wireOp",EDGE,"E289"),sQuery(id+"F5.wireOp",EDGE,"E290"),sQuery(id+"F5.wireOp",EDGE,"E291"),sQuery(id+"F5.wireOp",EDGE,"E292"),sQuery(id+"F5.wireOp",EDGE,"E293"),sQuery(id+"F5.wireOp",EDGE,"E294"),sQuery(id+"F5.wireOp",EDGE,"E295"),sQuery(id+"F5.wireOp",EDGE,"E296"),sQuery(id+"F5.wireOp",EDGE,"E297"),sQuery(id+"F5.wireOp",EDGE,"E298"),sQuery(id+"F5.wireOp",EDGE,"E299"),sQuery(id+"F5.wireOp",EDGE,"E300"),sQuery(id+"F5.wireOp",EDGE,"E301"),sQuery(id+"F5.wireOp",EDGE,"E302"),sQuery(id+"F5.wireOp",EDGE,"E303"),sQuery(id+"F5.wireOp",EDGE,"E304"),sQuery(id+"F5.wireOp",EDGE,"E305"),sQuery(id+"F5.wireOp",EDGE,"E306"),sQuery(id+"F5.wireOp",EDGE,"E307"),sQuery(id+"F5.wireOp",EDGE,"E308"),sQuery(id+"F5.wireOp",EDGE,"E309"),sQuery(id+"F5.wireOp",EDGE,"E310"),sQuery(id+"F5.wireOp",EDGE,"E311"),sQuery(id+"F5.wireOp",EDGE,"E312"),sQuery(id+"F5.wireOp",EDGE,"E313"),sQuery(id+"F5.wireOp",EDGE,"E314"),sQuery(id+"F5.wireOp",EDGE,"E315"),sQuery(id+"F5.wireOp",EDGE,"E316"),sQuery(id+"F5.wireOp",EDGE,"E317"),sQuery(id+"F5.wireOp",EDGE,"E318"),sQuery(id+"F5.wireOp",EDGE,"E319"),sQuery(id+"F5.wireOp",EDGE,"E320"),sQuery(id+"F5.wireOp",EDGE,"E321"),sQuery(id+"F5.wireOp",EDGE,"E322"),sQuery(id+"F5.wireOp",EDGE,"E323"),sQuery(id+"F5.wireOp",EDGE,"E324"),sQuery(id+"F5.wireOp",EDGE,"E325"),sQuery(id+"F5.wireOp",EDGE,"E326"),sQuery(id+"F5.wireOp",EDGE,"E327"),sQuery(id+"F5.wireOp",EDGE,"E328"),sQuery(id+"F5.wireOp",EDGE,"E329"),sQuery(id+"F5.wireOp",EDGE,"E330"),sQuery(id+"F5.wireOp",EDGE,"E331"),sQuery(id+"F5.wireOp",EDGE,"E332"),sQuery(id+"F5.wireOp",EDGE,"E333"),sQuery(id+"F5.wireOp",EDGE,"E334"),sQuery(id+"F5.wireOp",EDGE,"E335"),sQuery(id+"F5.wireOp",EDGE,"E336"),sQuery(id+"F5.wireOp",EDGE,"E337"),sQuery(id+"F5.wireOp",EDGE,"E338"),sQuery(id+"F5.wireOp",EDGE,"E339"),sQuery(id+"F5.wireOp",EDGE,"E340"),sQuery(id+"F5.wireOp",EDGE,"E341"),sQuery(id+"F5.wireOp",EDGE,"E342"),sQuery(id+"F5.wireOp",EDGE,"E343"),sQuery(id+"F5.wireOp",EDGE,"E344"),sQuery(id+"F5.wireOp",EDGE,"E345"),sQuery(id+"F5.wireOp",EDGE,"E346"),sQuery(id+"F5.wireOp",EDGE,"E347"),sQuery(id+"F5.wireOp",EDGE,"E348"),sQuery(id+"F5.wireOp",EDGE,"E349"),sQuery(id+"F5.wireOp",EDGE,"E350"),sQuery(id+"F5.wireOp",EDGE,"E351"),sQuery(id+"F5.wireOp",EDGE,"f8da9cec-7b2f-4bc9-a1d4-2b5411403650"),sQuery(id+"F5.wireOp",EDGE,"E352"),sQuery(id+"F5.wireOp",EDGE,"E353"),sQuery(id+"F5.wireOp",EDGE,"E354"),sQuery(id+"F5.wireOp",EDGE,"E355"),sQuery(id+"F5.wireOp",EDGE,"E356"),sQuery(id+"F5.wireOp",EDGE,"E357"),sQuery(id+"F5.wireOp",EDGE,"E358"),sQuery(id+"F5.wireOp",EDGE,"E359"),sQuery(id+"F5.wireOp",EDGE,"E360"),sQuery(id+"F5.wireOp",EDGE,"E361"),sQuery(id+"F5.wireOp",EDGE,"E362"),sQuery(id+"F5.wireOp",EDGE,"E363"),sQuery(id+"F5.wireOp",EDGE,"E364"),sQuery(id+"F5.wireOp",EDGE,"E365"),sQuery(id+"F5.wireOp",EDGE,"E366"),sQuery(id+"F5.wireOp",EDGE,"E367"),sQuery(id+"F5.wireOp",EDGE,"E368"),sQuery(id+"F5.wireOp",EDGE,"E369"),sQuery(id+"F5.wireOp",EDGE,"E370"),sQuery(id+"F5.wireOp",EDGE,"E371"),sQuery(id+"F5.wireOp",EDGE,"E372"),sQuery(id+"F5.wireOp",EDGE,"E373"),sQuery(id+"F5.wireOp",EDGE,"E374"),sQuery(id+"F5.wireOp",EDGE,"E375"),sQuery(id+"F5.wireOp",EDGE,"E376"),sQuery(id+"F5.wireOp",EDGE,"E377"),sQuery(id+"F5.wireOp",EDGE,"E378"),sQuery(id+"F5.wireOp",EDGE,"E379"),sQuery(id+"F5.wireOp",EDGE,"E380"),sQuery(id+"F5.wireOp",EDGE,"E381"),sQuery(id+"F5.wireOp",EDGE,"E382"),sQuery(id+"F5.wireOp",EDGE,"E383"),sQuery(id+"F5.wireOp",EDGE,"E384"),sQuery(id+"F5.wireOp",EDGE,"E385"),sQuery(id+"F5.wireOp",EDGE,"E386"),sQuery(id+"F5.wireOp",EDGE,"E387"),sQuery(id+"F5.wireOp",EDGE,"E388"),sQuery(id+"F5.wireOp",EDGE,"E389"),sQuery(id+"F5.wireOp",EDGE,"E390"),sQuery(id+"F5.wireOp",EDGE,"E391"),sQuery(id+"F5.wireOp",EDGE,"E392"),sQuery(id+"F5.wireOp",EDGE,"E393"),sQuery(id+"F5.wireOp",EDGE,"E394"),sQuery(id+"F5.wireOp",EDGE,"E395"),sQuery(id+"F5.wireOp",EDGE,"E396"),sQuery(id+"F5.wireOp",EDGE,"E397"),sQuery(id+"F5.wireOp",EDGE,"E398"),sQuery(id+"F5.wireOp",EDGE,"E399"),sQuery(id+"F5.wireOp",EDGE,"E400"),sQuery(id+"F5.wireOp",EDGE,"E401"),sQuery(id+"F5.wireOp",EDGE,"E402"),sQuery(id+"F5.wireOp",EDGE,"E403"),sQuery(id+"F5.wireOp",EDGE,"E404"),sQuery(id+"F5.wireOp",EDGE,"E405"),sQuery(id+"F5.wireOp",EDGE,"E406"),sQuery(id+"F5.wireOp",EDGE,"E407"),sQuery(id+"F5.wireOp",EDGE,"E408"),sQuery(id+"F5.wireOp",EDGE,"e50b2a73-dbe0-49af-9818-043bc4b770b7"),sQuery(id+"F5.wireOp",EDGE,"3192dacf-c9b0-4add-b2ff-622d529d5276"),sQuery(id+"F5.wireOp",EDGE,"a760f7f5-50d2-4069-ae61-9f0150eb622a"),sQuery(id+"F5.wireOp",EDGE,"d05da671-36ba-480b-904f-18b828d8df16"),sQuery(id+"F5.wireOp",EDGE,"d0b5e2ac-79a7-496a-b9f2-9dfbf1994a6f"),sQuery(id+"F5.wireOp",EDGE,"3a1f5ba6-4bce-4adf-998b-58defe025cf1"),sQuery(id+"F5.wireOp",EDGE,"ba13a567-bd32-4ef4-b231-7c56e5c57941"),sQuery(id+"F5.wireOp",EDGE,"0198fe89-c9a9-47a4-b185-d3abcece0f94"),sQuery(id+"F5.wireOp",EDGE,"62c83cdd-3dc5-49e2-99f9-1ed18822ed02"),sQuery(id+"F5.wireOp",EDGE,"acd3ff7e-07b6-4d54-997f-62a762deb219"),sQuery(id+"F5.wireOp",EDGE,"13a34783-7e1d-490d-b916-87a67d3fd954"),sQuery(id+"F5.wireOp",EDGE,"6ebb1572-8034-4072-906c-c71277f5e59a"),sQuery(id+"F5.wireOp",EDGE,"817ea8ae-e84e-4a8f-b329-5e22f82cee5a"),sQuery(id+"F5.wireOp",EDGE,"42886714-01b2-419c-b494-14529d30c41e"),sQuery(id+"F5.wireOp",EDGE,"4dcc7670-04c6-434d-b86c-f27882d895c3"),sQuery(id+"F5.wireOp",EDGE,"3d8ed91e-de4b-4d74-8176-05fcae770f02"),sQuery(id+"F5.wireOp",EDGE,"380bd52f-33fc-4b1c-a6b0-4bd83269a229"),sQuery(id+"F5.wireOp",EDGE,"e7332b0b-daa6-4e9a-b51f-bbc013796d4e"),sQuery(id+"F5.wireOp",EDGE,"e21cb6cd-36b7-4b29-94f0-ceb19284b4f5"),sQuery(id+"F5.wireOp",EDGE,"3cf1f7aa-3fdb-4252-8b30-5e8a0345f4d3"),sQuery(id+"F5.wireOp",EDGE,"09dfff20-bcf4-4078-8b74-fbfc5d79eb5b"),sQuery(id+"F5.wireOp",EDGE,"e086dc9a-a9a8-4b14-854a-63db3c9ebaf3"),sQuery(id+"F5.wireOp",EDGE,"e6c18d36-9ed7-4690-84b3-10dc0461318e"),sQuery(id+"F5.wireOp",EDGE,"7df3fe8e-a2ce-4515-b6b4-940f7e797c20"),sQuery(id+"F5.wireOp",EDGE,"bbddd8dc-8a74-46dd-8fec-f63904305fb5"),sQuery(id+"F5.wireOp",EDGE,"666fe711-c8de-4d17-a90c-1a399eb6898c"),sQuery(id+"F5.wireOp",EDGE,"bf586407-e0c2-435f-ae6a-b2bc0af8acfd"),sQuery(id+"F5.wireOp",EDGE,"2d8d1cca-c7ac-4746-b572-240114e492ab"),sQuery(id+"F5.wireOp",EDGE,"94b1e6fd-2ec0-4a9e-b14b-cebb508a6714"),sQuery(id+"F5.wireOp",EDGE,"c4ea384a-893d-45ef-be2d-407a46ff1111"),sQuery(id+"F5.wireOp",EDGE,"6a33e5ae-5c29-4e6e-a6bf-bd9fe5d83104"),sQuery(id+"F5.wireOp",EDGE,"c8dd5164-f215-4f0a-85e5-5609beb0ede9"),sQuery(id+"F5.wireOp",EDGE,"E409"),sQuery(id+"F5.wireOp",EDGE,"E410"),sQuery(id+"F5.wireOp",EDGE,"E411"),sQuery(id+"F5.wireOp",EDGE,"E412"),sQuery(id+"F5.wireOp",EDGE,"E413"),sQuery(id+"F5.wireOp",EDGE,"E414"),sQuery(id+"F5.wireOp",EDGE,"E415"),sQuery(id+"F5.wireOp",EDGE,"E416"),sQuery(id+"F5.wireOp",EDGE,"E417"),sQuery(id+"F5.wireOp",EDGE,"E418"),sQuery(id+"F5.wireOp",EDGE,"E419"),sQuery(id+"F5.wireOp",EDGE,"E420"),sQuery(id+"F5.wireOp",EDGE,"1fe392f8-9b3e-4e2c-9996-48b16560636a"),sQuery(id+"F5.wireOp",EDGE,"ef7ba69b-8ca8-4572-81f3-a12e7aff0595"),sQuery(id+"F5.wireOp",EDGE,"e8ce3515-a2b3-4f5f-bd7d-ee4f2af88406"),sQuery(id+"F5.wireOp",EDGE,"d5eae4e2-6b3b-49ef-a972-befd102791e8"),sQuery(id+"F5.wireOp",EDGE,"0849ed6a-df34-4231-953f-35d8dc0011db"),sQuery(id+"F5.wireOp",EDGE,"3b89c9dc-2e36-4f69-83a2-e85360ca1f2c"),sQuery(id+"F5.wireOp",EDGE,"50e9ef4e-f1aa-407a-b32d-1340cb301130"),sQuery(id+"F5.wireOp",EDGE,"c815e510-fda9-4f62-afd5-5fc1f8908a17"),sQuery(id+"F5.wireOp",EDGE,"00af066a-186f-4b82-8764-7f91a23bf5d4"),sQuery(id+"F5.wireOp",EDGE,"1d6790fe-b63f-4626-902b-5ea6eb9eb72c"),sQuery(id+"F5.wireOp",EDGE,"5bcf9030-a7b3-4255-96a1-a1f9c1615fb9"),sQuery(id+"F5.wireOp",EDGE,"e281f879-60ae-41a7-ae77-92c89c21cd21"),sQuery(id+"F5.wireOp",EDGE,"f7f4f653-0b19-4bd6-ba1a-f24c9e95cf77"),sQuery(id+"F5.wireOp",EDGE,"f1d6f7fb-3ee2-4b46-87f4-5199b51ffce5"),sQuery(id+"F5.wireOp",EDGE,"6330ee19-06cf-497d-aaa6-8dd45a29ed05"),sQuery(id+"F5.wireOp",EDGE,"4ac48fb5-4c3f-461a-94a7-1aa3195e5f97"),sQuery(id+"F5.wireOp",EDGE,"9a757004-aee6-4056-b86e-9182a5a83851"),sQuery(id+"F5.wireOp",EDGE,"6ed777de-34d5-4967-81d0-37eac91d8910"),sQuery(id+"F5.wireOp",EDGE,"fb87d8c2-56fd-4bb1-a8c1-2aff75fbc24c"),sQuery(id+"F5.wireOp",EDGE,"b8d94ff1-50c6-471b-a876-031f0ebf4ae8"),sQuery(id+"F5.wireOp",EDGE,"ec6fabe4-981f-48b7-848e-ff0087499815"),sQuery(id+"F5.wireOp",EDGE,"dc428fa9-39a3-4c67-b193-5fafe66c24df"),sQuery(id+"F5.wireOp",EDGE,"6c31f29d-a243-4a52-87c1-bfe703c05162"),sQuery(id+"F5.wireOp",EDGE,"d55dee49-7e43-40ea-a81a-000c203fc6f9"),sQuery(id+"F5.wireOp",EDGE,"d301c3a3-067e-49cc-8bc3-42fc10f245fa"),sQuery(id+"F5.wireOp",EDGE,"c4b11f69-0fe4-4c06-85a2-65470cf08ff6"),sQuery(id+"F5.wireOp",EDGE,"e836d4f6-7a29-455a-a89f-3de545624932"),sQuery(id+"F5.wireOp",EDGE,"416a4f66-4cc9-4d54-a7c0-af95c77bf425"),sQuery(id+"F5.wireOp",EDGE,"eec94f5d-137c-4251-ad97-b63f297286fb"),sQuery(id+"F5.wireOp",EDGE,"fe71e6e2-1142-4679-b3ec-063d39d49c3d"),sQuery(id+"F5.wireOp",EDGE,"3328311c-98bd-4e47-a220-126c0ee391c2"),sQuery(id+"F5.wireOp",EDGE,"bea1705f-58b1-4a32-9463-f32aca27fe9d"),sQuery(id+"F5.wireOp",EDGE,"c1e52493-3cf1-486b-b0f6-ee77ffbcd6f8"),sQuery(id+"F5.wireOp",EDGE,"b54752de-259c-463d-b50e-b3472af1198a"),sQuery(id+"F5.wireOp",EDGE,"cd850257-8063-4059-a207-1c32c2c22f56"),sQuery(id+"F5.wireOp",EDGE,"0ae43893-f971-435f-bbd9-48caaec76fb1"),sQuery(id+"F5.wireOp",EDGE,"3678f8be-e80e-4c4f-96d9-5f953822b96b"),sQuery(id+"F5.wireOp",EDGE,"E421"),sQuery(id+"F5.wireOp",EDGE,"E422"),sQuery(id+"F5.wireOp",EDGE,"E423"),sQuery(id+"F5.wireOp",EDGE,"E424"),sQuery(id+"F5.wireOp",EDGE,"E425"),sQuery(id+"F5.wireOp",EDGE,"E426"),sQuery(id+"F5.wireOp",EDGE,"E427"),sQuery(id+"F5.wireOp",EDGE,"E428"),sQuery(id+"F5.wireOp",EDGE,"E437"),sQuery(id+"F5.wireOp",EDGE,"E438"),sQuery(id+"F5.wireOp",EDGE,"E439"),sQuery(id+"F5.wireOp",EDGE,"E440"),sQuery(id+"F5.wireOp",EDGE,"E441"),sQuery(id+"F5.wireOp",EDGE,"E442"),sQuery(id+"F5.wireOp",EDGE,"E443"),sQuery(id+"F5.wireOp",EDGE,"E444"),sQuery(id+"F5.wireOp",EDGE,"E445"),sQuery(id+"F5.wireOp",EDGE,"E446"),sQuery(id+"F5.wireOp",EDGE,"E447"),sQuery(id+"F5.wireOp",EDGE,"E448"),sQuery(id+"F5.wireOp",EDGE,"E449"),sQuery(id+"F5.wireOp",EDGE,"E450"),sQuery(id+"F5.wireOp",EDGE,"E451"),sQuery(id+"F5.wireOp",EDGE,"E452"),sQuery(id+"F5.wireOp",EDGE,"E453"),sQuery(id+"F5.wireOp",EDGE,"E454"),sQuery(id+"F5.wireOp",EDGE,"E455"),sQuery(id+"F5.wireOp",EDGE,"E456"),sQuery(id+"F5.wireOp",EDGE,"E457"),sQuery(id+"F5.wireOp",EDGE,"E458"),sQuery(id+"F5.wireOp",EDGE,"E459"),sQuery(id+"F5.wireOp",EDGE,"E460"),sQuery(id+"F5.wireOp",EDGE,"E461"),sQuery(id+"F5.wireOp",EDGE,"E462"),sQuery(id+"F5.wireOp",EDGE,"E463"),sQuery(id+"F5.wireOp",EDGE,"E464"),sQuery(id+"F5.wireOp",EDGE,"E465"),sQuery(id+"F5.wireOp",EDGE,"E466"),sQuery(id+"F5.wireOp",EDGE,"E467"),sQuery(id+"F5.wireOp",EDGE,"E468"),sQuery(id+"F5.wireOp",EDGE,"E469"),sQuery(id+"F5.wireOp",EDGE,"E470"),sQuery(id+"F5.wireOp",EDGE,"E471"),sQuery(id+"F5.wireOp",EDGE,"E472"),sQuery(id+"F5.wireOp",EDGE,"E473"),sQuery(id+"F5.wireOp",EDGE,"E474"),sQuery(id+"F5.wireOp",EDGE,"E475"),sQuery(id+"F5.wireOp",EDGE,"E476"),sQuery(id+"F5.wireOp",EDGE,"E477"),sQuery(id+"F5.wireOp",EDGE,"E478"),sQuery(id+"F5.wireOp",EDGE,"E479"),sQuery(id+"F5.wireOp",EDGE,"E480"),sQuery(id+"F5.wireOp",EDGE,"E481"),sQuery(id+"F5.wireOp",EDGE,"E482"),sQuery(id+"F5.wireOp",EDGE,"E483"),sQuery(id+"F5.wireOp",EDGE,"E484"),sQuery(id+"F5.wireOp",EDGE,"E485"),sQuery(id+"F5.wireOp",EDGE,"E486"),sQuery(id+"F5.wireOp",EDGE,"E487"),sQuery(id+"F5.wireOp",EDGE,"E488"),sQuery(id+"F5.wireOp",EDGE,"E489"),sQuery(id+"F5.wireOp",EDGE,"E490"),sQuery(id+"F5.wireOp",EDGE,"E702"),sQuery(id+"F5.wireOp",EDGE,"E703"),sQuery(id+"F5.wireOp",EDGE,"E704"),sQuery(id+"F5.wireOp",EDGE,"E705"),sQuery(id+"F5.wireOp",EDGE,"E706"),sQuery(id+"F5.wireOp",EDGE,"E707"),sQuery(id+"F5.wireOp",EDGE,"E708"),sQuery(id+"F5.wireOp",EDGE,"E709"),sQuery(id+"F5.wireOp",EDGE,"E710"),sQuery(id+"F5.wireOp",EDGE,"E818"),sQuery(id+"F5.wireOp",EDGE,"E819"),sQuery(id+"F5.wireOp",EDGE,"E820"),sQuery(id+"F5.wireOp",EDGE,"E821"),sQuery(id+"F5.wireOp",EDGE,"E822"),sQuery(id+"F5.wireOp",EDGE,"E823"),sQuery(id+"F5.wireOp",EDGE,"E824"),sQuery(id+"F5.wireOp",EDGE,"E825"),sQuery(id+"F5.wireOp",EDGE,"E826"),sQuery(id+"F5.wireOp",EDGE,"E827"),sQuery(id+"F5.wireOp",EDGE,"E828"),sQuery(id+"F5.wireOp",EDGE,"E829"),sQuery(id+"F5.wireOp",EDGE,"E830"),sQuery(id+"F5.wireOp",EDGE,"E831"),sQuery(id+"F5.wireOp",EDGE,"E832"),sQuery(id+"F5.wireOp",EDGE,"E833"),sQuery(id+"F5.wireOp",EDGE,"E834"),sQuery(id+"F5.wireOp",EDGE,"E835"),sQuery(id+"F5.wireOp",EDGE,"E836"),sQuery(id+"F5.wireOp",EDGE,"E837"),sQuery(id+"F5.wireOp",EDGE,"78064346-bcd2-4b21-a179-3d3965e1aea7"),sQuery(id+"F5.wireOp",EDGE,"f1191037-d949-496c-8a80-5dba232b8bf4"),sQuery(id+"F5.wireOp",EDGE,"792e79ff-0bf5-41bd-bab8-273c9246d57b"),sQuery(id+"F5.wireOp",EDGE,"b8d4e551-6d98-4ba8-87a2-e3d4ab5b5389"),sQuery(id+"F5.wireOp",EDGE,"2def0819-5b42-4630-b59b-4bbe010f2271"),sQuery(id+"F5.wireOp",EDGE,"c879f7bd-644d-4771-a872-e7d7c6dfa277"),sQuery(id+"F5.wireOp",EDGE,"ae9617b8-c085-4dc9-a5ba-58cc1937d47b"),sQuery(id+"F5.wireOp",EDGE,"64dd56c9-d90d-43e3-b2e8-4613116b9765"),sQuery(id+"F5.wireOp",EDGE,"d81e2062-aece-432c-a45f-c198f37e4e4a"),sQuery(id+"F5.wireOp",EDGE,"b8c4b4c2-01a5-4d0a-b8e4-d404a4cec525"),sQuery(id+"F5.wireOp",EDGE,"941377f1-f141-4ea7-88e4-c7391afa82d5"),sQuery(id+"F5.wireOp",EDGE,"2bfe8565-9ecb-4f17-b6c2-31899a670241"),sQuery(id+"F5.wireOp",EDGE,"6f8d0698-54cc-4541-ac33-962df0bff909"),sQuery(id+"F5.wireOp",EDGE,"fa1d52f0-8f20-4d40-833f-bdd5e04ad82b"),sQuery(id+"F5.wireOp",EDGE,"67c819c6-9747-4516-851f-5398fdd6c6d2"),sQuery(id+"F5.wireOp",EDGE,"8c675f47-a023-4cc4-b15e-3fc8c0ed79e8"),sQuery(id+"F5.wireOp",EDGE,"166bdb07-2d3a-4fed-9111-14d2e2ee3d23"),sQuery(id+"F5.wireOp",EDGE,"6cf3b431-1849-4e4c-a149-efd4c7f47024"),sQuery(id+"F5.wireOp",EDGE,"2c80058c-2c09-40ad-bf6d-f64d61246a07"),sQuery(id+"F5.wireOp",EDGE,"710578c6-1140-4f06-9cd2-382697344c03"),sQuery(id+"F5.wireOp",EDGE,"4ed06e1a-6da8-44ba-9bb6-439f14f794c5"),sQuery(id+"F5.wireOp",EDGE,"31a56190-78e2-4511-b54c-6489413b5c8e"),sQuery(id+"F5.wireOp",EDGE,"535a82a2-6dea-4d6a-ba58-9968d4c6b170"),sQuery(id+"F5.wireOp",EDGE,"5dac4d6c-f9d8-4925-812e-01abbbb76501"),sQuery(id+"F5.wireOp",EDGE,"b0ed199d-5e92-4aa1-a867-d4806d1a978e"),sQuery(id+"F5.wireOp",EDGE,"5240232b-bc28-4f0f-86c6-cb1c7d1d51e7"),sQuery(id+"F5.wireOp",EDGE,"83101b58-7ef3-4a95-bb59-4dc3cfcd9e2d"),sQuery(id+"F5.wireOp",EDGE,"727b43bc-82d9-4e8d-83ae-f4852c7a5858"),sQuery(id+"F5.wireOp",EDGE,"a2148597-2235-4ca7-af5d-08e407f1823e"),sQuery(id+"F5.wireOp",EDGE,"E838"),sQuery(id+"F5.wireOp",EDGE,"E839"),sQuery(id+"F5.wireOp",EDGE,"E840"),sQuery(id+"F5.wireOp",EDGE,"E841"),sQuery(id+"F5.wireOp",EDGE,"E842"),sQuery(id+"F5.wireOp",EDGE,"E843"),sQuery(id+"F5.wireOp",EDGE,"E844"),sQuery(id+"F5.wireOp",EDGE,"E845"),sQuery(id+"F5.wireOp",EDGE,"E846"),sQuery(id+"F5.wireOp",EDGE,"E847"),sQuery(id+"F5.wireOp",EDGE,"aa42a33b-246c-4542-8e35-18c338a4df4d"),sQuery(id+"F5.wireOp",EDGE,"34631624-348c-4d38-b39f-58fc8ba3eac5"),sQuery(id+"F5.wireOp",EDGE,"0f92a1be-e357-4d45-a338-aa34f6e6679a"),sQuery(id+"F5.wireOp",EDGE,"16cdfaf2-baf5-43c1-a814-b6545847e338"),sQuery(id+"F5.wireOp",EDGE,"e52912fe-6980-4dc3-a0ff-939361b4d1dd"),sQuery(id+"F5.wireOp",EDGE,"b70ee90e-cd90-44a8-a2e6-e80a98b656ce"),sQuery(id+"F5.wireOp",EDGE,"9e08e6f3-189d-400b-8087-30cda962dabd"),sQuery(id+"F5.wireOp",EDGE,"15b42662-2228-417b-8e33-5e454e363ee3"),sQuery(id+"F5.wireOp",EDGE,"9a1d9512-af59-44a4-8e09-ebf1d3037821"),sQuery(id+"F5.wireOp",EDGE,"fe4a2ad1-ef52-42b4-8322-38f5125e4d93"),sQuery(id+"F5.wireOp",EDGE,"338abb94-5da4-499a-8c70-d88d6e14d76f"),sQuery(id+"F5.wireOp",EDGE,"E848"),sQuery(id+"F5.wireOp",EDGE,"E849"),sQuery(id+"F5.wireOp",EDGE,"E850"),sQuery(id+"F5.wireOp",EDGE,"E851"),sQuery(id+"F5.wireOp",EDGE,"E852"),sQuery(id+"F5.wireOp",EDGE,"E853"),sQuery(id+"F5.wireOp",EDGE,"E854"),sQuery(id+"F5.wireOp",EDGE,"E855"),sQuery(id+"F5.wireOp",EDGE,"E856"),sQuery(id+"F5.wireOp",EDGE,"E857"),sQuery(id+"F5.wireOp",EDGE,"E858"),sQuery(id+"F5.wireOp",EDGE,"4cd7c0e4-11ed-430c-8391-d0ac0c08fe21"),sQuery(id+"F5.wireOp",EDGE,"36dae108-10bf-4f55-a77a-b4e1cb613be9"),sQuery(id+"F5.wireOp",EDGE,"5c5735d7-794b-4b60-99b6-d692ba9b9937"),sQuery(id+"F5.wireOp",EDGE,"71944f44-181b-4564-a5d9-b638db8e7424"),sQuery(id+"F5.wireOp",EDGE,"458910d0-be99-410f-8a4c-3f1fc20eddfb"),sQuery(id+"F5.wireOp",EDGE,"E859"),sQuery(id+"F5.wireOp",EDGE,"E860"),sQuery(id+"F5.wireOp",EDGE,"5bf707a4-a57c-4534-b332-36607f9424be"),sQuery(id+"F5.wireOp",EDGE,"2ecd74b3-1389-4b50-8dad-589e61a6d625"),sQuery(id+"F5.wireOp",EDGE,"d16606de-7a0a-4e41-ba1a-35fc5d0d79fc"),sQuery(id+"F5.wireOp",EDGE,"d6078512-8877-4560-9675-16010213d3a1"),sQuery(id+"F5.wireOp",EDGE,"26044d8a-ca63-4323-9e95-0a06a4b16b21"),sQuery(id+"F5.wireOp",EDGE,"799c72da-5ff2-498d-b8ce-b2b43eeb844e"),sQuery(id+"F5.wireOp",EDGE,"00f790d4-f5db-4858-8917-bc27a7f367ce"),sQuery(id+"F5.wireOp",EDGE,"fde288f1-8825-4256-86fb-bd354416b416"),sQuery(id+"F5.wireOp",EDGE,"a228d7b3-5cdb-4b9c-b478-b0355fb537ce"),sQuery(id+"F5.wireOp",EDGE,"E861"),sQuery(id+"F5.wireOp",EDGE,"E862"),sQuery(id+"F5.wireOp",EDGE,"E863"),sQuery(id+"F5.wireOp",EDGE,"E864"),sQuery(id+"F5.wireOp",EDGE,"E865"),sQuery(id+"F5.wireOp",EDGE,"E866"),sQuery(id+"F5.wireOp",EDGE,"E867"),sQuery(id+"F5.wireOp",EDGE,"E868"),sQuery(id+"F5.wireOp",EDGE,"E869"),sQuery(id+"F5.wireOp",EDGE,"E870"),sQuery(id+"F5.wireOp",EDGE,"E871"),sQuery(id+"F5.wireOp",EDGE,"E872"),sQuery(id+"F5.wireOp",EDGE,"E873"),sQuery(id+"F5.wireOp",EDGE,"E874"),sQuery(id+"F5.wireOp",EDGE,"E875"),sQuery(id+"F5.wireOp",EDGE,"E876"),sQuery(id+"F5.wireOp",EDGE,"E877"),sQuery(id+"F5.wireOp",EDGE,"E878"),sQuery(id+"F5.wireOp",EDGE,"E879"),sQuery(id+"F5.wireOp",EDGE,"E880"),sQuery(id+"F5.wireOp",EDGE,"E881"),sQuery(id+"F5.wireOp",EDGE,"E882"),sQuery(id+"F5.wireOp",EDGE,"E883"),sQuery(id+"F5.wireOp",EDGE,"E884"),sQuery(id+"F5.wireOp",EDGE,"E885"),sQuery(id+"F5.wireOp",EDGE,"E886"),sQuery(id+"F5.wireOp",EDGE,"E887"),sQuery(id+"F5.wireOp",EDGE,"E888"),sQuery(id+"F5.wireOp",EDGE,"E889"),sQuery(id+"F5.wireOp",EDGE,"E890"),sQuery(id+"F5.wireOp",EDGE,"E891"),sQuery(id+"F5.wireOp",EDGE,"E892"),sQuery(id+"F5.wireOp",EDGE,"E893"),sQuery(id+"F5.wireOp",EDGE,"E894"),sQuery(id+"F5.wireOp",EDGE,"E895"),sQuery(id+"F5.wireOp",EDGE,"E896"),sQuery(id+"F5.wireOp",EDGE,"E897"),sQuery(id+"F5.wireOp",EDGE,"75f79cd2-38ea-416c-828c-d4ab9eb250a2"),sQuery(id+"F5.wireOp",EDGE,"E899"),sQuery(id+"F5.wireOp",EDGE,"E900"),sQuery(id+"F5.wireOp",EDGE,"E901"),sQuery(id+"F5.wireOp",EDGE,"E902"),sQuery(id+"F5.wireOp",EDGE,"E903"),sQuery(id+"F5.wireOp",EDGE,"E904"),sQuery(id+"F5.wireOp",EDGE,"E905"),sQuery(id+"F5.wireOp",EDGE,"E906"),sQuery(id+"F5.wireOp",EDGE,"E907"),sQuery(id+"F5.wireOp",EDGE,"E908"),sQuery(id+"F5.wireOp",EDGE,"E909"),sQuery(id+"F5.wireOp",EDGE,"E910"),sQuery(id+"F5.wireOp",EDGE,"E911"),sQuery(id+"F5.wireOp",EDGE,"E912"),sQuery(id+"F5.wireOp",EDGE,"E913"),sQuery(id+"F5.wireOp",EDGE,"E914"),sQuery(id+"F5.wireOp",EDGE,"E915"),sQuery(id+"F5.wireOp",EDGE,"E916"),sQuery(id+"F5.wireOp",EDGE,"E917"),sQuery(id+"F5.wireOp",EDGE,"E918"),sQuery(id+"F5.wireOp",EDGE,"E919"),sQuery(id+"F5.wireOp",EDGE,"0d0c95db-cda7-4078-9913-b0d35e0ba85e"),sQuery(id+"F5.wireOp",EDGE,"c9856e0c-9be3-4a58-95df-031c7ab28f76"),sQuery(id+"F5.wireOp",EDGE,"56ab6970-854d-4e00-92fc-f3982c0b219c"),sQuery(id+"F5.wireOp",EDGE,"f14bf8b6-f0ae-46c9-9dc4-aa46568fad42"),sQuery(id+"F5.wireOp",EDGE,"0f74f727-8c43-40f6-b22e-53e5d2b784a1"),sQuery(id+"F5.wireOp",EDGE,"635ab6ec-dd13-426e-a63e-433c89b71b8e"),sQuery(id+"F5.wireOp",EDGE,"4fc4dac9-4a3d-438f-af98-c10b4f00dff1"),sQuery(id+"F5.wireOp",EDGE,"cc9ef70d-8b81-424a-b7b9-14f3cfa5c023"),sQuery(id+"F5.wireOp",EDGE,"d59cf5d4-3d32-4079-94c8-ce51966af5ac"),sQuery(id+"F5.wireOp",EDGE,"ab79ecb9-d815-483e-9a0f-a5c5d07b6b72"),sQuery(id+"F5.wireOp",EDGE,"d16283d7-f645-4632-b454-a74f6fc6c62b"),sQuery(id+"F5.wireOp",EDGE,"6066a84c-2912-46d0-b8a0-babaaa2d1bfc"),sQuery(id+"F5.wireOp",EDGE,"9fa6ff5f-709e-4aca-9ca5-16ed0de0ed87"),sQuery(id+"F5.wireOp",EDGE,"d429519d-be4f-4ecd-ba31-ec7e3c6ac8af"),sQuery(id+"F5.wireOp",EDGE,"9d4632a8-59e9-4c56-a8c1-94d09cea5101"),sQuery(id+"F5.wireOp",EDGE,"1ee47f2a-f9f7-4eff-896a-b2af78655b07"),sQuery(id+"F5.wireOp",EDGE,"E920"),sQuery(id+"F5.wireOp",EDGE,"E921"),sQuery(id+"F5.wireOp",EDGE,"E922"),sQuery(id+"F5.wireOp",EDGE,"E923"),sQuery(id+"F5.wireOp",EDGE,"E924"),sQuery(id+"F5.wireOp",EDGE,"E925"),sQuery(id+"F5.wireOp",EDGE,"E926"),sQuery(id+"F5.wireOp",EDGE,"E927"),sQuery(id+"F5.wireOp",EDGE,"E928"),sQuery(id+"F5.wireOp",EDGE,"E929"),sQuery(id+"F5.wireOp",EDGE,"E930"),sQuery(id+"F5.wireOp",EDGE,"E931"),sQuery(id+"F5.wireOp",EDGE,"E932"),sQuery(id+"F5.wireOp",EDGE,"E933"),sQuery(id+"F5.wireOp",EDGE,"E934"),sQuery(id+"F5.wireOp",EDGE,"E935"),sQuery(id+"F5.wireOp",EDGE,"E936"),sQuery(id+"F5.wireOp",EDGE,"68042cb4-c667-4de0-8887-00a79389dd59"),sQuery(id+"F5.wireOp",EDGE,"8b20b442-4081-4d24-8105-ed4063a1d694"),sQuery(id+"F5.wireOp",EDGE,"727e5bff-038d-491e-85a1-d2aeefa88c42"),sQuery(id+"F5.wireOp",EDGE,"30ffcc43-6827-47fb-a204-e79a5e3f3b15"),sQuery(id+"F5.wireOp",EDGE,"4ff6ee03-4bc0-4529-b31d-fc3a52d8fcf5"),sQuery(id+"F5.wireOp",EDGE,"6a0daa51-027b-4dc6-b10f-b04089bf63e2"),sQuery(id+"F5.wireOp",EDGE,"6d36ecf3-af23-44ba-8358-5fe0254ffe58"),sQuery(id+"F5.wireOp",EDGE,"d1b2aa4d-62af-47b6-aa20-8021a251f396"),sQuery(id+"F5.wireOp",EDGE,"209ca080-4e10-44f6-a13c-2a6f2f51dff5"),sQuery(id+"F5.wireOp",EDGE,"26ec6aa1-64f8-43ee-a927-c2b08ea9dbea"),sQuery(id+"F5.wireOp",EDGE,"82b0bd8f-7ca4-47a5-b9cc-12312776f551"),sQuery(id+"F5.wireOp",EDGE,"0817266c-b656-4a8a-a49d-f9e90360854d"),sQuery(id+"F5.wireOp",EDGE,"a2d39030-61e3-4071-bb87-fb6568d1b1aa"),sQuery(id+"F5.wireOp",EDGE,"429a2066-a121-4644-a533-8cf63eb9db20"),sQuery(id+"F5.wireOp",EDGE,"f73d2678-3049-4982-abfc-fb602dfe0eee"),sQuery(id+"F5.wireOp",EDGE,"b38f713b-e37f-4f8b-8927-742130862c94"),sQuery(id+"F5.wireOp",EDGE,"66c7b75e-39ff-44e9-94fa-90d5ac9984f1"),sQuery(id+"F5.wireOp",EDGE,"ab1bf793-9792-4634-b31a-beb572f20701"),sQuery(id+"F5.wireOp",EDGE,"ba70fce2-17fe-48d8-87b5-fcbc7ba4d7b4"),sQuery(id+"F5.wireOp",EDGE,"031cfe2f-b627-40e7-aa0b-80b2501f9e0c"),sQuery(id+"F5.wireOp",EDGE,"22440ee4-9ee6-46f2-8d1f-a6d68a20d353"),sQuery(id+"F5.wireOp",EDGE,"a6be5563-5290-43f5-a6c1-ecf37d9fd1cc"),sQuery(id+"F5.wireOp",EDGE,"a5ccb78a-c543-490c-b0b8-988fe9b797ab"),sQuery(id+"F5.wireOp",EDGE,"722fba6d-f534-4abf-bb6b-744739a4851d"),sQuery(id+"F5.wireOp",EDGE,"2a8a5afa-cbd2-4247-a1ff-3cec5c8476d3"),sQuery(id+"F5.wireOp",EDGE,"1e4bf437-5d4d-4012-9dea-92b04afdf5d8"),sQuery(id+"F5.wireOp",EDGE,"36d3eb0c-ba9e-407e-8aa8-900d3aa23a9d"),sQuery(id+"F5.wireOp",EDGE,"cdcef0b0-a9ab-4587-9003-dc8d7632a209"),sQuery(id+"F5.wireOp",EDGE,"1f467671-57fd-4e5f-9532-4ed3c67f3de4"),sQuery(id+"F5.wireOp",EDGE,"dbe625c1-3718-45b7-952e-e1ba61a40f35"),sQuery(id+"F5.wireOp",EDGE,"9451bd94-afee-4d58-9358-7fe44aa3f52e"),sQuery(id+"F5.wireOp",EDGE,"4b36d359-15a9-4d33-ae4d-e2c0242eba96"),sQuery(id+"F5.wireOp",EDGE,"d2ea5af9-3367-47c9-863e-329d621e8b6c"),sQuery(id+"F5.wireOp",EDGE,"63fe0a5a-94df-4713-b4f4-44d1cf42b2ab"),sQuery(id+"F5.wireOp",EDGE,"351cd200-02c2-408f-b0df-082bd75c0e78"),sQuery(id+"F5.wireOp",EDGE,"7c4ebc4f-8123-4ce8-bc91-2ad4f85c526d"),sQuery(id+"F5.wireOp",EDGE,"d57fdf87-6af9-4fa6-8657-d523150e9d83"),sQuery(id+"F5.wireOp",EDGE,"a33a6e29-6ac6-4efa-bb84-f0c4b00f3175"),sQuery(id+"F5.wireOp",EDGE,"b5017328-4601-44bb-b209-27e8f4db5470"),sQuery(id+"F5.wireOp",EDGE,"d12deec6-c134-422a-9f3b-435d7fff0fc6"),sQuery(id+"F5.wireOp",EDGE,"ce93c21b-d376-4ea5-96fe-4dd733bb41e4"),sQuery(id+"F5.wireOp",EDGE,"e693d1c2-30ef-4db4-841d-6caab1dee21b"),sQuery(id+"F5.wireOp",EDGE,"a1dae1e8-7c2a-43ec-be96-bde59322924c"),sQuery(id+"F5.wireOp",EDGE,"63ff5bda-24f6-485b-b0f1-dcaa3263f149"),sQuery(id+"F5.wireOp",EDGE,"8146a261-2c4e-43c5-92da-606e0f4cc9b8"),sQuery(id+"F5.wireOp",EDGE,"0fffab68-8fee-4322-8111-016aa2ba3915"),sQuery(id+"F5.wireOp",EDGE,"f3ecc831-25b0-4d1e-a388-64852277b1f1"),sQuery(id+"F5.wireOp",EDGE,"81a7874a-9802-4b85-9308-b64d1ce36c1f"),sQuery(id+"F5.wireOp",EDGE,"c3538c96-a3cd-43ee-9237-a93af6e2df44"),sQuery(id+"F5.wireOp",EDGE,"2517adcd-0d53-4b4b-9473-e2a9a6ef5ff8"),sQuery(id+"F5.wireOp",EDGE,"028387ea-b4b4-4e1d-970c-32dc6e6629fd"),sQuery(id+"F5.wireOp",EDGE,"f85f96c0-b4a4-49e6-a85a-6ffbc13c4311"),sQuery(id+"F5.wireOp",EDGE,"ca2f368a-e81b-4108-81d6-8e2aa8ee675a"),sQuery(id+"F5.wireOp",EDGE,"1df49e63-d7df-466c-8a99-794b8af999bd"),sQuery(id+"F5.wireOp",EDGE,"b897553e-46b2-4374-9e1d-a740f745d568"),sQuery(id+"F5.wireOp",EDGE,"a1756127-f412-44ec-a967-d5e1eddc00a1"),sQuery(id+"F5.wireOp",EDGE,"4457c5bb-3ad4-4b0e-bcb4-56d15a89cbae"),sQuery(id+"F5.wireOp",EDGE,"cb6cb63e-4ecd-49a8-a5e2-a2eb6416363c"),sQuery(id+"F5.wireOp",EDGE,"4f55984e-9d7f-4c8b-bcc1-26180860f893"),sQuery(id+"F5.wireOp",EDGE,"e3503de7-8306-4bc2-9706-7d38cc9b68dc"),sQuery(id+"F5.wireOp",EDGE,"209dce3b-b4aa-4c09-b4bf-88510148ab9f"),sQuery(id+"F5.wireOp",EDGE,"0bafb03a-72b7-4571-86b0-b20b96e535fe"),sQuery(id+"F5.wireOp",EDGE,"e85dff79-297a-487e-a99d-b8575eb27d5c"),sQuery(id+"F5.wireOp",EDGE,"6bc89dae-ebc8-4dab-9986-daf332bdde7b"),sQuery(id+"F5.wireOp",EDGE,"E946"),sQuery(id+"F5.wireOp",EDGE,"E947"),sQuery(id+"F5.wireOp",EDGE,"E948"),sQuery(id+"F5.wireOp",EDGE,"E949"),sQuery(id+"F5.wireOp",EDGE,"E950"),sQuery(id+"F5.wireOp",EDGE,"E951"),sQuery(id+"F5.wireOp",EDGE,"E952"),sQuery(id+"F5.wireOp",EDGE,"E953"),sQuery(id+"F5.wireOp",EDGE,"E954"),sQuery(id+"F5.wireOp",EDGE,"E955"),sQuery(id+"F5.wireOp",EDGE,"E956"),sQuery(id+"F5.wireOp",EDGE,"E957"),sQuery(id+"F5.wireOp",EDGE,"E958"),sQuery(id+"F5.wireOp",EDGE,"E959"),sQuery(id+"F5.wireOp",EDGE,"E960"),sQuery(id+"F5.wireOp",EDGE,"E961"),sQuery(id+"F5.wireOp",EDGE,"E962"),sQuery(id+"F5.wireOp",EDGE,"E963"),sQuery(id+"F5.wireOp",EDGE,"E964"),sQuery(id+"F5.wireOp",EDGE,"E965"),sQuery(id+"F5.wireOp",EDGE,"E966"),sQuery(id+"F5.wireOp",EDGE,"E967"),sQuery(id+"F5.wireOp",EDGE,"E968"),sQuery(id+"F5.wireOp",EDGE,"E969"),sQuery(id+"F5.wireOp",EDGE,"E970"),sQuery(id+"F5.wireOp",EDGE,"E971"),sQuery(id+"F5.wireOp",EDGE,"E972"),sQuery(id+"F5.wireOp",EDGE,"E973"),sQuery(id+"F5.wireOp",EDGE,"E974")])]});
            var Q1;
            Q1=makeQuery(id+"F6.opExtrude","SWEPT_BODY",BODY,{"disambiguationData":[OSD([sQuery(id+"F5.wireOp",EDGE,"E731"),sQuery(id+"F5.wireOp",EDGE,"E732"),sQuery(id+"F5.wireOp",EDGE,"E733"),sQuery(id+"F5.wireOp",EDGE,"E734"),sQuery(id+"F5.wireOp",EDGE,"E735"),sQuery(id+"F5.wireOp",EDGE,"E736"),sQuery(id+"F5.wireOp",EDGE,"E737"),sQuery(id+"F5.wireOp",EDGE,"E738"),sQuery(id+"F5.wireOp",EDGE,"E739"),sQuery(id+"F5.wireOp",EDGE,"E740"),sQuery(id+"F5.wireOp",EDGE,"E741"),sQuery(id+"F5.wireOp",EDGE,"E742"),sQuery(id+"F5.wireOp",EDGE,"E743"),sQuery(id+"F5.wireOp",EDGE,"E744"),sQuery(id+"F5.wireOp",EDGE,"E745"),sQuery(id+"F5.wireOp",EDGE,"E746"),sQuery(id+"F5.wireOp",EDGE,"E747"),sQuery(id+"F5.wireOp",EDGE,"E748"),sQuery(id+"F5.wireOp",EDGE,"E749"),sQuery(id+"F5.wireOp",EDGE,"E750"),sQuery(id+"F5.wireOp",EDGE,"E751"),sQuery(id+"F5.wireOp",EDGE,"E752"),sQuery(id+"F5.wireOp",EDGE,"E753"),sQuery(id+"F5.wireOp",EDGE,"E754"),sQuery(id+"F5.wireOp",EDGE,"E755"),sQuery(id+"F5.wireOp",EDGE,"E756"),sQuery(id+"F5.wireOp",EDGE,"E757"),sQuery(id+"F5.wireOp",EDGE,"E758"),sQuery(id+"F5.wireOp",EDGE,"E759"),sQuery(id+"F5.wireOp",EDGE,"E760"),sQuery(id+"F5.wireOp",EDGE,"E761"),sQuery(id+"F5.wireOp",EDGE,"E762"),sQuery(id+"F5.wireOp",EDGE,"E763"),sQuery(id+"F5.wireOp",EDGE,"E764"),sQuery(id+"F5.wireOp",EDGE,"E765"),sQuery(id+"F5.wireOp",EDGE,"E766"),sQuery(id+"F5.wireOp",EDGE,"E767"),sQuery(id+"F5.wireOp",EDGE,"E768"),sQuery(id+"F5.wireOp",EDGE,"6fad5ba0-ad24-4659-9c25-0a35bc094989"),sQuery(id+"F5.wireOp",EDGE,"25f03aa2-7501-49cc-a9d2-033c35681b98"),sQuery(id+"F5.wireOp",EDGE,"f61bcbb6-cb81-4407-8cf5-22900fd0148d"),sQuery(id+"F5.wireOp",EDGE,"ae7b1d1d-96ce-47a4-be26-75929f430f11"),sQuery(id+"F5.wireOp",EDGE,"0f0e79a2-3506-4f25-b267-4f4d111b1ec0"),sQuery(id+"F5.wireOp",EDGE,"88526c3f-4019-4532-84f4-41c64478b8fb"),sQuery(id+"F5.wireOp",EDGE,"aae81ac4-aa43-4671-81b6-3b845fa11e5e"),sQuery(id+"F5.wireOp",EDGE,"b24ff494-832f-44f4-8ee6-818e5d37226d"),sQuery(id+"F5.wireOp",EDGE,"0862685d-433f-4023-bc7f-3e05fcc96e85"),sQuery(id+"F5.wireOp",EDGE,"8b575a2f-21f7-4bfa-82c8-78b3498d887a"),sQuery(id+"F5.wireOp",EDGE,"da0efb62-485e-4908-97bf-9ddf20e8763b"),sQuery(id+"F5.wireOp",EDGE,"d12fad51-9231-4155-abd0-e93f1253ba00"),sQuery(id+"F5.wireOp",EDGE,"694741db-bfc0-43e6-9901-73395cc468a6")])]});
            var Q2;
            Q2=makeQuery(id+"F6.opExtrude","SWEPT_BODY",BODY,{"disambiguationData":[OSD([sQuery(id+"F5.wireOp",EDGE,"E769"),sQuery(id+"F5.wireOp",EDGE,"E770"),sQuery(id+"F5.wireOp",EDGE,"E771"),sQuery(id+"F5.wireOp",EDGE,"E772"),sQuery(id+"F5.wireOp",EDGE,"E773"),sQuery(id+"F5.wireOp",EDGE,"E774"),sQuery(id+"F5.wireOp",EDGE,"E775"),sQuery(id+"F5.wireOp",EDGE,"E776"),sQuery(id+"F5.wireOp",EDGE,"E777"),sQuery(id+"F5.wireOp",EDGE,"E778"),sQuery(id+"F5.wireOp",EDGE,"E779"),sQuery(id+"F5.wireOp",EDGE,"E780"),sQuery(id+"F5.wireOp",EDGE,"E781"),sQuery(id+"F5.wireOp",EDGE,"E782"),sQuery(id+"F5.wireOp",EDGE,"E783"),sQuery(id+"F5.wireOp",EDGE,"E784"),sQuery(id+"F5.wireOp",EDGE,"E785"),sQuery(id+"F5.wireOp",EDGE,"E786"),sQuery(id+"F5.wireOp",EDGE,"E787"),sQuery(id+"F5.wireOp",EDGE,"E788"),sQuery(id+"F5.wireOp",EDGE,"E789"),sQuery(id+"F5.wireOp",EDGE,"E790"),sQuery(id+"F5.wireOp",EDGE,"E791"),sQuery(id+"F5.wireOp",EDGE,"E792"),sQuery(id+"F5.wireOp",EDGE,"E793"),sQuery(id+"F5.wireOp",EDGE,"E794"),sQuery(id+"F5.wireOp",EDGE,"E795"),sQuery(id+"F5.wireOp",EDGE,"E796"),sQuery(id+"F5.wireOp",EDGE,"E797"),sQuery(id+"F5.wireOp",EDGE,"E798"),sQuery(id+"F5.wireOp",EDGE,"E799"),sQuery(id+"F5.wireOp",EDGE,"E800"),sQuery(id+"F5.wireOp",EDGE,"E801"),sQuery(id+"F5.wireOp",EDGE,"E802"),sQuery(id+"F5.wireOp",EDGE,"E803"),sQuery(id+"F5.wireOp",EDGE,"E804"),sQuery(id+"F5.wireOp",EDGE,"E805"),sQuery(id+"F5.wireOp",EDGE,"E806"),sQuery(id+"F5.wireOp",EDGE,"E807"),sQuery(id+"F5.wireOp",EDGE,"E808"),sQuery(id+"F5.wireOp",EDGE,"E809"),sQuery(id+"F5.wireOp",EDGE,"E810"),sQuery(id+"F5.wireOp",EDGE,"E811"),sQuery(id+"F5.wireOp",EDGE,"E812"),sQuery(id+"F5.wireOp",EDGE,"E813"),sQuery(id+"F5.wireOp",EDGE,"E814"),sQuery(id+"F5.wireOp",EDGE,"E815"),sQuery(id+"F5.wireOp",EDGE,"E816"),sQuery(id+"F5.wireOp",EDGE,"E817"),sQuery(id+"F5.wireOp",EDGE,"79105ba2-21b4-46e3-96eb-3a8645dd36c9"),sQuery(id+"F5.wireOp",EDGE,"e5191a9d-33f3-467f-b154-c8be79b7ac37"),sQuery(id+"F5.wireOp",EDGE,"81db5623-bfb3-4806-8cab-54c420783076")])]});
            var Q3;
            Q3=makeQuery(id+"F6.opExtrude","SWEPT_BODY",BODY,{"disambiguationData":[OSD([sQuery(id+"F5.wireOp",EDGE,"E1005"),sQuery(id+"F5.wireOp",EDGE,"E1006"),sQuery(id+"F5.wireOp",EDGE,"E1007"),sQuery(id+"F5.wireOp",EDGE,"E1008")])]});
            var Q4;
            Q4=makeQuery(id+"F6.opExtrude","SWEPT_BODY",BODY,{"disambiguationData":[OSD([sQuery(id+"F5.wireOp",EDGE,"E1001.0"),sQuery(id+"F5.wireOp",EDGE,"E1001.1"),sQuery(id+"F5.wireOp",EDGE,"E1001.2"),sQuery(id+"F5.wireOp",EDGE,"E1003.0"),sQuery(id+"F5.wireOp",EDGE,"E1003.1"),sQuery(id+"F5.wireOp",EDGE,"E1003.2")])]});
            var Q5;
            Q5=makeQuery(id+"F6.opExtrude","SWEPT_BODY",BODY,{"disambiguationData":[OSD([sQuery(id+"F5.wireOp",EDGE,"E1013.sketch_text.stroke-0"),sQuery(id+"F5.wireOp",EDGE,"E1013.sketch_text.stroke-1"),sQuery(id+"F5.wireOp",EDGE,"E1013.sketch_text.stroke-2"),sQuery(id+"F5.wireOp",EDGE,"E1013.sketch_text.stroke-3"),sQuery(id+"F5.wireOp",EDGE,"E1013.sketch_text.stroke-4"),sQuery(id+"F5.wireOp",EDGE,"E1013.sketch_text.stroke-5"),sQuery(id+"F5.wireOp",EDGE,"E1013.sketch_text.stroke-6"),sQuery(id+"F5.wireOp",EDGE,"E1013.sketch_text.stroke-7"),sQuery(id+"F5.wireOp",EDGE,"E1013.sketch_text.stroke-8"),sQuery(id+"F5.wireOp",EDGE,"E1013.sketch_text.stroke-9"),sQuery(id+"F5.wireOp",EDGE,"E1013.sketch_text.stroke-10"),sQuery(id+"F5.wireOp",EDGE,"E1013.sketch_text.stroke-11"),sQuery(id+"F5.wireOp",EDGE,"E1013.sketch_text.stroke-12"),sQuery(id+"F5.wireOp",EDGE,"E1013.sketch_text.stroke-13"),sQuery(id+"F5.wireOp",EDGE,"E1013.sketch_text.stroke-14")])]});
            var Q6;
            Q6=makeQuery(id+"F6.opExtrude","SWEPT_BODY",BODY,{"disambiguationData":[OSD([sQuery(id+"F5.wireOp",EDGE,"E1013.sketch_text.stroke-15"),sQuery(id+"F5.wireOp",EDGE,"E1013.sketch_text.stroke-16"),sQuery(id+"F5.wireOp",EDGE,"E1013.sketch_text.stroke-17"),sQuery(id+"F5.wireOp",EDGE,"E1013.sketch_text.stroke-18"),sQuery(id+"F5.wireOp",EDGE,"E1013.sketch_text.stroke-19"),sQuery(id+"F5.wireOp",EDGE,"E1013.sketch_text.stroke-20"),sQuery(id+"F5.wireOp",EDGE,"E1013.sketch_text.stroke-21"),sQuery(id+"F5.wireOp",EDGE,"E1013.sketch_text.stroke-22"),sQuery(id+"F5.wireOp",EDGE,"E1013.sketch_text.stroke-23"),sQuery(id+"F5.wireOp",EDGE,"E1013.sketch_text.stroke-24"),sQuery(id+"F5.wireOp",EDGE,"E1013.sketch_text.stroke-25"),sQuery(id+"F5.wireOp",EDGE,"E1013.sketch_text.stroke-26"),sQuery(id+"F5.wireOp",EDGE,"E1013.sketch_text.stroke-27"),sQuery(id+"F5.wireOp",EDGE,"E1013.sketch_text.stroke-28"),sQuery(id+"F5.wireOp",EDGE,"E1013.sketch_text.stroke-29"),sQuery(id+"F5.wireOp",EDGE,"E1013.sketch_text.stroke-30"),sQuery(id+"F5.wireOp",EDGE,"E1013.sketch_text.stroke-31"),sQuery(id+"F5.wireOp",EDGE,"E1013.sketch_text.stroke-32")])]});
            var Q7;
            Q7=makeQuery(id+"F6.opExtrude","SWEPT_BODY",BODY,{"disambiguationData":[OSD([sQuery(id+"F5.wireOp",EDGE,"E1009"),sQuery(id+"F5.wireOp",EDGE,"E1010"),sQuery(id+"F5.wireOp",EDGE,"E1011"),sQuery(id+"F5.wireOp",EDGE,"E1012")])]});
            var Q8;
            Q8=makeQuery(id+"F6.opExtrude","SWEPT_BODY",BODY,{"disambiguationData":[OSD([sQuery(id+"F5.wireOp",EDGE,"E1002.0"),sQuery(id+"F5.wireOp",EDGE,"E1002.1"),sQuery(id+"F5.wireOp",EDGE,"E1002.2"),sQuery(id+"F5.wireOp",EDGE,"E1002.3"),sQuery(id+"F5.wireOp",EDGE,"E1004.0"),sQuery(id+"F5.wireOp",EDGE,"E1004.1"),sQuery(id+"F5.wireOp",EDGE,"E1004.2"),sQuery(id+"F5.wireOp",EDGE,"E1004.3")])]});
            var Q9;
            Q9=makeQuery(id+"F1.opExtrude","CAP_EDGE",EDGE,{"disambiguationData":[OSD([sQuery(id+"F0.wireOp",EDGE,"E0")])],"isStart":true});
            transform(context, id + "F7", {"entities" : qUnion([Q0, Q1, Q2, Q3, Q4, Q5, Q6, Q7, Q8]), "transformType" : TransformType.ROTATION, "transformAxis" : qUnion([Q9]), "angle" : 180 * degree, "oppositeDirection" : true, "makeCopy" : false});
        }
    });
